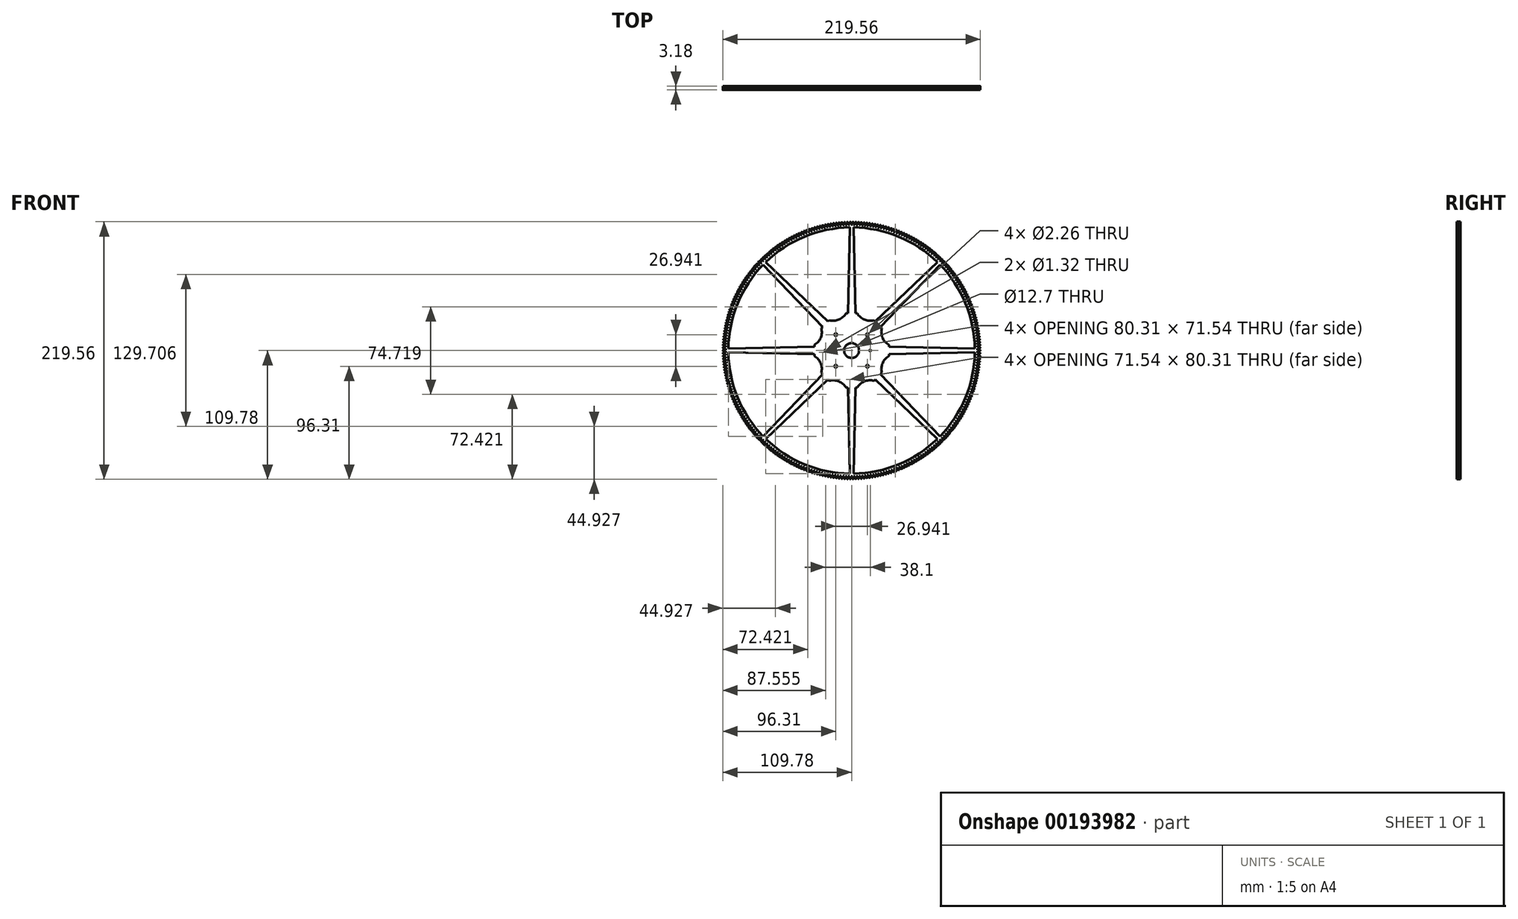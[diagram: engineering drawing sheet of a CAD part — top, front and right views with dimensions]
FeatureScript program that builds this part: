
annotation { "Feature Type Name" : "Feature", "Feature Type Description" : "" }
export const myFeature = defineFeature(function(context is Context, id is Id, definition is map)
    precondition{}
    {
        {
            var Q0;
            Q0=qCreatedBy(makeId("Front.planeOp"),FACE);
            var sketch = newSketch(context, id + "F0", { "sketchPlane" : qUnion([Q0])});
            skLineSegment(sketch, "E0", {"start": v(0, 0) * mm, "end": v(0, 109.78) * mm, "construction": true});
            skLineSegment(sketch, "E1", {"start": v(1.59, 105.01) * mm, "end": v(3.18, 31.75) * mm});
            skCircle(sketch, "E2.cCircle", {"center": v(0, 0) * mm, "radius": 31.75 * mm, "construction": true});
            skLineSegment(sketch, "E2.0", {"start": v(19.08, 25.82) * mm, "end": v(20.2, 24.7) * mm});
            skLineSegment(sketch, "E2.1", {"start": v(31.75, 4.76) * mm, "end": v(31.75, 3.18) * mm});
            skLineSegment(sketch, "E2.2", {"start": v(25.82, -19.08) * mm, "end": v(24.7, -20.2) * mm});
            skLineSegment(sketch, "E2.3", {"start": v(4.76, -31.75) * mm, "end": v(3.18, -31.75) * mm});
            skLineSegment(sketch, "E2.4", {"start": v(-19.08, -25.82) * mm, "end": v(-20.2, -24.7) * mm});
            skLineSegment(sketch, "E2.5", {"start": v(-31.75, -4.76) * mm, "end": v(-31.75, -3.18) * mm});
            skLineSegment(sketch, "E2.6", {"start": v(-25.82, 19.08) * mm, "end": v(-24.7, 20.2) * mm});
            skLineSegment(sketch, "E2.7", {"start": v(-4.76, 31.75) * mm, "end": v(-3.18, 31.75) * mm});
            skLineSegment(sketch, "E3", {"start": v(-1.59, 105.01) * mm, "end": v(-3.18, 31.75) * mm});
            skLineSegment(sketch, "E4", {"start": v(-1.59, 105.01) * mm, "end": v(1.59, 105.01) * mm, "construction": true});
            skLineSegment(sketch, "E5.1.0", {"start": v(73.13, 75.38) * mm, "end": v(75.38, 73.13) * mm, "construction": true});
            skLineSegment(sketch, "E5.1.1", {"start": v(73.13, 75.38) * mm, "end": v(20.2, 24.7) * mm});
            skLineSegment(sketch, "E5.1.2", {"start": v(0, 0) * mm, "end": v(74.25, 74.25) * mm, "construction": true});
            skLineSegment(sketch, "E5.1.3", {"start": v(75.38, 73.13) * mm, "end": v(24.7, 20.2) * mm});
            skLineSegment(sketch, "E5.2.0", {"start": v(105.01, 1.59) * mm, "end": v(105.01, -1.59) * mm, "construction": true});
            skLineSegment(sketch, "E5.2.1", {"start": v(105.01, 1.59) * mm, "end": v(31.75, 3.18) * mm});
            skLineSegment(sketch, "E5.2.2", {"start": v(0, 0) * mm, "end": v(105.01, 0) * mm, "construction": true});
            skLineSegment(sketch, "E5.2.3", {"start": v(105.01, -1.59) * mm, "end": v(31.75, -3.18) * mm});
            skLineSegment(sketch, "E5.3.0", {"start": v(75.38, -73.13) * mm, "end": v(73.13, -75.38) * mm, "construction": true});
            skLineSegment(sketch, "E5.3.1", {"start": v(75.38, -73.13) * mm, "end": v(24.7, -20.2) * mm});
            skLineSegment(sketch, "E5.3.2", {"start": v(0, 0) * mm, "end": v(74.25, -74.25) * mm, "construction": true});
            skLineSegment(sketch, "E5.3.3", {"start": v(73.13, -75.38) * mm, "end": v(20.2, -24.7) * mm});
            skLineSegment(sketch, "E5.4.0", {"start": v(1.59, -105.01) * mm, "end": v(-1.59, -105.01) * mm, "construction": true});
            skLineSegment(sketch, "E5.4.1", {"start": v(1.59, -105.01) * mm, "end": v(3.18, -31.75) * mm});
            skLineSegment(sketch, "E5.4.2", {"start": v(0, 0) * mm, "end": v(0, -105.01) * mm, "construction": true});
            skLineSegment(sketch, "E5.4.3", {"start": v(-1.59, -105.01) * mm, "end": v(-3.18, -31.75) * mm});
            skLineSegment(sketch, "E5.5.0", {"start": v(-73.13, -75.38) * mm, "end": v(-75.38, -73.13) * mm, "construction": true});
            skLineSegment(sketch, "E5.5.1", {"start": v(-73.13, -75.38) * mm, "end": v(-20.2, -24.7) * mm});
            skLineSegment(sketch, "E5.5.2", {"start": v(0, 0) * mm, "end": v(-74.25, -74.25) * mm, "construction": true});
            skLineSegment(sketch, "E5.5.3", {"start": v(-75.38, -73.13) * mm, "end": v(-24.7, -20.2) * mm});
            skLineSegment(sketch, "E5.6.0", {"start": v(-105.01, -1.59) * mm, "end": v(-105.01, 1.59) * mm, "construction": true});
            skLineSegment(sketch, "E5.6.1", {"start": v(-105.01, -1.59) * mm, "end": v(-31.75, -3.18) * mm});
            skLineSegment(sketch, "E5.6.2", {"start": v(0, 0) * mm, "end": v(-105.01, 0) * mm, "construction": true});
            skLineSegment(sketch, "E5.6.3", {"start": v(-105.01, 1.59) * mm, "end": v(-31.75, 3.18) * mm});
            skLineSegment(sketch, "E5.7.0", {"start": v(-75.38, 73.13) * mm, "end": v(-73.13, 75.38) * mm, "construction": true});
            skLineSegment(sketch, "E5.7.1", {"start": v(-75.38, 73.13) * mm, "end": v(-24.7, 20.2) * mm});
            skLineSegment(sketch, "E5.7.2", {"start": v(0, 0) * mm, "end": v(-74.25, 74.25) * mm, "construction": true});
            skLineSegment(sketch, "E5.7.3", {"start": v(-73.13, 75.38) * mm, "end": v(-20.2, 24.7) * mm});
            skArc(sketch, "E6", {"start": v(-31.75, 4.76) * mm, "mid": v(-26.35, 10.91) * mm, "end": v(-25.82, 19.08) * mm});
            skArc(sketch, "E7", {"start": v(-19.08, 25.82) * mm, "mid": v(-10.91, 26.35) * mm, "end": v(-4.76, 31.75) * mm});
            skArc(sketch, "E8", {"start": v(4.76, 31.75) * mm, "mid": v(10.91, 26.35) * mm, "end": v(19.08, 25.82) * mm});
            skArc(sketch, "E9", {"start": v(25.82, 19.08) * mm, "mid": v(26.35, 10.91) * mm, "end": v(31.75, 4.76) * mm});
            skArc(sketch, "E10", {"start": v(31.75, -4.76) * mm, "mid": v(26.35, -10.91) * mm, "end": v(25.82, -19.08) * mm});
            skArc(sketch, "E11", {"start": v(19.08, -25.82) * mm, "mid": v(10.91, -26.35) * mm, "end": v(4.76, -31.75) * mm});
            skArc(sketch, "E12", {"start": v(-4.76, -31.75) * mm, "mid": v(-10.91, -26.35) * mm, "end": v(-19.08, -25.82) * mm});
            skArc(sketch, "E13", {"start": v(-25.82, -19.08) * mm, "mid": v(-26.35, -10.91) * mm, "end": v(-31.75, -4.76) * mm});
            skArc(sketch, "E14", {"start": v(-105.01, -1.59) * mm, "mid": v(-97.03, -40.2) * mm, "end": v(-75.38, -73.13) * mm});
            skArc(sketch, "E15.trimOffspring", {"start": v(1.59, -105.01) * mm, "mid": v(40.2, -97.03) * mm, "end": v(73.13, -75.38) * mm});
            skArc(sketch, "E16.trimOffspring", {"start": v(-73.13, -75.38) * mm, "mid": v(-40.2, -97.03) * mm, "end": v(-1.59, -105.01) * mm});
            skArc(sketch, "E17.trimOffspring", {"start": v(75.38, -73.13) * mm, "mid": v(97.03, -40.2) * mm, "end": v(105.01, -1.59) * mm});
            skArc(sketch, "E18.trimOffspring", {"start": v(105.01, 1.59) * mm, "mid": v(97.03, 40.2) * mm, "end": v(75.38, 73.13) * mm});
            skArc(sketch, "E19.trimOffspring", {"start": v(73.13, 75.38) * mm, "mid": v(40.2, 97.03) * mm, "end": v(1.59, 105.01) * mm});
            skArc(sketch, "E20.trimOffspring", {"start": v(-1.59, 105.01) * mm, "mid": v(-40.2, 97.03) * mm, "end": v(-73.13, 75.38) * mm});
            skArc(sketch, "E21.trimOffspring", {"start": v(-75.38, 73.13) * mm, "mid": v(-97.03, 40.2) * mm, "end": v(-105.01, 1.59) * mm});
            skLineSegment(sketch, "E22.trimOffspring", {"start": v(3.18, 31.75) * mm, "end": v(4.76, 31.75) * mm});
            skLineSegment(sketch, "E23.trimOffspring", {"start": v(-20.2, 24.7) * mm, "end": v(-19.08, 25.82) * mm});
            skLineSegment(sketch, "E24.trimOffspring", {"start": v(-31.75, 3.18) * mm, "end": v(-31.75, 4.76) * mm});
            skLineSegment(sketch, "E25.trimOffspring", {"start": v(-24.7, -20.2) * mm, "end": v(-25.82, -19.08) * mm});
            skLineSegment(sketch, "E26.trimOffspring", {"start": v(-3.18, -31.75) * mm, "end": v(-4.76, -31.75) * mm});
            skLineSegment(sketch, "E27.trimOffspring", {"start": v(20.2, -24.7) * mm, "end": v(19.08, -25.82) * mm});
            skLineSegment(sketch, "E28.trimOffspring", {"start": v(31.75, -3.18) * mm, "end": v(31.75, -4.76) * mm});
            skLineSegment(sketch, "E29.trimOffspring", {"start": v(24.7, 20.2) * mm, "end": v(25.82, 19.08) * mm});
            skPoint(sketch, "E30", {"position": v(22.45, 22.45) * mm});
            skLineSegment(sketch, "E31", {"start": v(20.2, 24.7) * mm, "end": v(24.7, 20.2) * mm, "construction": true});
            skLineSegment(sketch, "E32", {"start": v(31.75, 3.18) * mm, "end": v(31.75, -3.18) * mm, "construction": true});
            skPoint(sketch, "E33", {"position": v(31.75, 0) * mm});
            skLineSegment(sketch, "E34", {"start": v(-3.18, 31.75) * mm, "end": v(3.18, 31.75) * mm, "construction": true});
            skPoint(sketch, "E35", {"position": v(0, 31.75) * mm});
            skLineSegment(sketch, "E36", {"start": v(20.2, -24.7) * mm, "end": v(24.7, -20.2) * mm, "construction": true});
            skPoint(sketch, "E37", {"position": v(22.45, -22.45) * mm});
            skLineSegment(sketch, "E38", {"start": v(-3.18, -31.75) * mm, "end": v(3.18, -31.75) * mm, "construction": true});
            skPoint(sketch, "E39", {"position": v(0, -31.75) * mm});
            skLineSegment(sketch, "E40", {"start": v(-24.7, -20.2) * mm, "end": v(-20.2, -24.7) * mm, "construction": true});
            skPoint(sketch, "E41", {"position": v(-22.45, -22.45) * mm});
            skLineSegment(sketch, "E42", {"start": v(-31.75, 3.18) * mm, "end": v(-31.75, -3.18) * mm, "construction": true});
            skPoint(sketch, "E43", {"position": v(-31.75, 0) * mm});
            skLineSegment(sketch, "E44", {"start": v(-24.7, 20.2) * mm, "end": v(-20.2, 24.7) * mm, "construction": true});
            skPoint(sketch, "E45", {"position": v(-22.45, 22.45) * mm});
            skCircle(sketch, "E46", {"center": v(0, 0) * mm, "radius": 6.35 * mm});
            skCircle(sketch, "E47", {"center": v(0, 0) * mm, "radius": 19.05 * mm, "construction": true});
            skCircle(sketch, "E48", {"center": v(-13.47, 13.47) * mm, "radius": 1.13 * mm});
            skCircle(sketch, "E49.1.0", {"center": v(-13.47, -13.47) * mm, "radius": 1.13 * mm});
            skCircle(sketch, "E49.2.0", {"center": v(13.47, -13.47) * mm, "radius": 1.13 * mm});
            skCircle(sketch, "E50.1.3.0", {"center": v(13.47, 13.47) * mm, "radius": 1.13 * mm});
            skCircle(sketch, "E51", {"center": v(0, 0) * mm, "radius": 107.25 * mm, "construction": true});
            skCircle(sketch, "E52", {"center": v(0, 0) * mm, "radius": 109.78 * mm, "construction": true});
            skCircle(sketch, "E53", {"center": v(0, 0) * mm, "radius": 108.75 * mm, "construction": true});
            skLineSegment(sketch, "E54", {"start": v(0, 0) * mm, "end": v(2.38, 109.76) * mm, "construction": true});
            skLineSegment(sketch, "E55", {"start": v(1.19, 109.78) * mm, "end": v(0, 0) * mm, "construction": true});
            skPoint(sketch, "E56.orphan", {"position": v(0, 105.01) * mm});
            skLineSegment(sketch, "E57", {"start": v(0.63, 107.25) * mm, "end": v(0.58, 108.55) * mm});
            skLineSegment(sketch, "E58", {"start": v(1.7, 107.24) * mm, "end": v(1.77, 108.54) * mm});
            skArc(sketch, "E59", {"start": v(1.19, 109.78) * mm, "mid": v(0.73, 109.24) * mm, "end": v(0.58, 108.55) * mm});
            skArc(sketch, "E60", {"start": v(1.77, 108.54) * mm, "mid": v(1.64, 109.23) * mm, "end": v(1.19, 109.78) * mm});
            skLineSegment(sketch, "E61", {"start": v(0.59, 108.75) * mm, "end": v(1.77, 108.74) * mm, "construction": true});
            skPoint(sketch, "E62", {"position": v(1.18, 108.74) * mm});
            skLineSegment(sketch, "E63", {"start": v(0.63, 107.25) * mm, "end": v(1.7, 107.24) * mm, "construction": true});
            skPoint(sketch, "E64", {"position": v(1.16, 107.24) * mm});
            skLineSegment(sketch, "E65.1.0", {"start": v(-1.7, 107.24) * mm, "end": v(-1.77, 108.54) * mm});
            skArc(sketch, "E65.1.1", {"start": v(-1.19, 109.78) * mm, "mid": v(-1.64, 109.23) * mm, "end": v(-1.77, 108.54) * mm});
            skArc(sketch, "E65.1.2", {"start": v(-0.58, 108.55) * mm, "mid": v(-0.73, 109.24) * mm, "end": v(-1.19, 109.78) * mm});
            skLineSegment(sketch, "E65.1.3", {"start": v(-0.63, 107.25) * mm, "end": v(-0.58, 108.55) * mm});
            skLineSegment(sketch, "E65.2.0", {"start": v(-4.02, 107.17) * mm, "end": v(-4.12, 108.47) * mm});
            skArc(sketch, "E65.2.1", {"start": v(-3.57, 109.73) * mm, "mid": v(-4, 109.17) * mm, "end": v(-4.12, 108.47) * mm});
            skArc(sketch, "E65.2.2", {"start": v(-2.93, 108.51) * mm, "mid": v(-3.1, 109.2) * mm, "end": v(-3.57, 109.73) * mm});
            skLineSegment(sketch, "E65.2.3", {"start": v(-2.95, 107.2) * mm, "end": v(-2.93, 108.51) * mm});
            skLineSegment(sketch, "E66.1.3.0", {"start": v(-6.34, 107.06) * mm, "end": v(-6.47, 108.36) * mm});
            skArc(sketch, "E66.3.3.0", {"start": v(-5.94, 109.62) * mm, "mid": v(-6.37, 109.06) * mm, "end": v(-6.47, 108.36) * mm});
            skArc(sketch, "E66.7.3.0", {"start": v(-5.28, 108.42) * mm, "mid": v(-5.46, 109.1) * mm, "end": v(-5.94, 109.62) * mm});
            skLineSegment(sketch, "E66.11.3.0", {"start": v(-5.27, 107.12) * mm, "end": v(-5.28, 108.42) * mm});
            skLineSegment(sketch, "E66.1.4.0", {"start": v(-8.66, 106.9) * mm, "end": v(-8.82, 108.2) * mm});
            skArc(sketch, "E66.3.4.0", {"start": v(-8.32, 109.47) * mm, "mid": v(-8.73, 108.9) * mm, "end": v(-8.82, 108.2) * mm});
            skArc(sketch, "E66.7.4.0", {"start": v(-7.63, 108.28) * mm, "mid": v(-7.83, 108.96) * mm, "end": v(-8.32, 109.47) * mm});
            skLineSegment(sketch, "E66.11.4.0", {"start": v(-7.6, 106.98) * mm, "end": v(-7.63, 108.28) * mm});
            skLineSegment(sketch, "E66.1.5.0", {"start": v(-10.97, 106.69) * mm, "end": v(-11.16, 107.98) * mm});
            skArc(sketch, "E66.3.5.0", {"start": v(-10.69, 109.26) * mm, "mid": v(-11.08, 108.68) * mm, "end": v(-11.16, 107.98) * mm});
            skArc(sketch, "E66.7.5.0", {"start": v(-9.98, 108.1) * mm, "mid": v(-10.18, 108.77) * mm, "end": v(-10.69, 109.26) * mm});
            skLineSegment(sketch, "E66.11.5.0", {"start": v(-9.9, 106.8) * mm, "end": v(-9.98, 108.1) * mm});
            skLineSegment(sketch, "E66.1.6.0", {"start": v(-13.28, 106.42) * mm, "end": v(-13.5, 107.7) * mm});
            skArc(sketch, "E66.3.6.0", {"start": v(-13.05, 109) * mm, "mid": v(-13.44, 108.41) * mm, "end": v(-13.5, 107.7) * mm});
            skArc(sketch, "E66.7.6.0", {"start": v(-12.32, 107.85) * mm, "mid": v(-12.54, 108.52) * mm, "end": v(-13.05, 109) * mm});
            skLineSegment(sketch, "E66.11.6.0", {"start": v(-12.22, 106.55) * mm, "end": v(-12.32, 107.85) * mm});
            skLineSegment(sketch, "E66.1.7.0", {"start": v(-15.58, 106.11) * mm, "end": v(-15.82, 107.4) * mm});
            skArc(sketch, "E66.3.7.0", {"start": v(-15.4, 108.7) * mm, "mid": v(-15.78, 108.1) * mm, "end": v(-15.82, 107.4) * mm});
            skArc(sketch, "E66.7.7.0", {"start": v(-14.65, 107.56) * mm, "mid": v(-14.89, 108.22) * mm, "end": v(-15.4, 108.7) * mm});
            skLineSegment(sketch, "E66.11.7.0", {"start": v(-14.53, 106.26) * mm, "end": v(-14.65, 107.56) * mm});
            skLineSegment(sketch, "E66.1.8.0", {"start": v(-17.88, 105.75) * mm, "end": v(-18.15, 107.02) * mm});
            skArc(sketch, "E66.3.8.0", {"start": v(-17.76, 108.34) * mm, "mid": v(-18.12, 107.73) * mm, "end": v(-18.15, 107.02) * mm});
            skArc(sketch, "E66.7.8.0", {"start": v(-16.98, 107.22) * mm, "mid": v(-17.23, 107.88) * mm, "end": v(-17.76, 108.34) * mm});
            skLineSegment(sketch, "E66.11.8.0", {"start": v(-16.82, 105.92) * mm, "end": v(-16.98, 107.22) * mm});
            skLineSegment(sketch, "E66.1.9.0", {"start": v(-20.16, 105.34) * mm, "end": v(-20.46, 106.6) * mm});
            skArc(sketch, "E66.3.9.0", {"start": v(-20.1, 107.93) * mm, "mid": v(-20.45, 107.31) * mm, "end": v(-20.46, 106.6) * mm});
            skArc(sketch, "E66.7.9.0", {"start": v(-19.3, 106.82) * mm, "mid": v(-19.56, 107.48) * mm, "end": v(-20.1, 107.93) * mm});
            skLineSegment(sketch, "E66.11.9.0", {"start": v(-19.11, 105.53) * mm, "end": v(-19.3, 106.82) * mm});
            skLineSegment(sketch, "E66.1.10.0", {"start": v(-22.44, 104.88) * mm, "end": v(-22.77, 106.14) * mm});
            skArc(sketch, "E66.3.10.0", {"start": v(-22.44, 107.47) * mm, "mid": v(-22.77, 106.84) * mm, "end": v(-22.77, 106.14) * mm});
            skArc(sketch, "E66.7.10.0", {"start": v(-21.6, 106.38) * mm, "mid": v(-21.88, 107.03) * mm, "end": v(-22.44, 107.47) * mm});
            skLineSegment(sketch, "E66.11.10.0", {"start": v(-21.4, 105.1) * mm, "end": v(-21.6, 106.38) * mm});
            skLineSegment(sketch, "E66.1.11.0", {"start": v(-24.7, 104.36) * mm, "end": v(-25.06, 105.62) * mm});
            skArc(sketch, "E66.3.11.0", {"start": v(-24.76, 106.96) * mm, "mid": v(-25.08, 106.33) * mm, "end": v(-25.06, 105.62) * mm});
            skArc(sketch, "E66.7.11.0", {"start": v(-23.9, 105.89) * mm, "mid": v(-24.2, 106.53) * mm, "end": v(-24.76, 106.96) * mm});
            skLineSegment(sketch, "E66.11.11.0", {"start": v(-23.67, 104.6) * mm, "end": v(-23.9, 105.89) * mm});
            skLineSegment(sketch, "E66.1.12.0", {"start": v(-26.96, 103.8) * mm, "end": v(-27.34, 105.05) * mm});
            skArc(sketch, "E66.3.12.0", {"start": v(-27.07, 106.4) * mm, "mid": v(-27.38, 105.76) * mm, "end": v(-27.34, 105.05) * mm});
            skArc(sketch, "E66.7.12.0", {"start": v(-26.2, 105.34) * mm, "mid": v(-26.5, 105.98) * mm, "end": v(-27.07, 106.4) * mm});
            skLineSegment(sketch, "E66.11.12.0", {"start": v(-25.93, 104.07) * mm, "end": v(-26.2, 105.34) * mm});
            skLineSegment(sketch, "E66.1.13.0", {"start": v(-29.2, 103.2) * mm, "end": v(-29.61, 104.43) * mm});
            skArc(sketch, "E66.3.13.0", {"start": v(-29.37, 105.78) * mm, "mid": v(-29.66, 105.14) * mm, "end": v(-29.61, 104.43) * mm});
            skArc(sketch, "E66.7.13.0", {"start": v(-28.47, 104.75) * mm, "mid": v(-28.79, 105.38) * mm, "end": v(-29.37, 105.78) * mm});
            skLineSegment(sketch, "E66.11.13.0", {"start": v(-28.18, 103.48) * mm, "end": v(-28.47, 104.75) * mm});
            skLineSegment(sketch, "E66.1.14.0", {"start": v(-31.44, 102.54) * mm, "end": v(-31.87, 103.77) * mm});
            skArc(sketch, "E66.3.14.0", {"start": v(-31.66, 105.12) * mm, "mid": v(-31.93, 104.47) * mm, "end": v(-31.87, 103.77) * mm});
            skArc(sketch, "E66.7.14.0", {"start": v(-30.73, 104.1) * mm, "mid": v(-31.07, 104.73) * mm, "end": v(-31.66, 105.12) * mm});
            skLineSegment(sketch, "E66.11.14.0", {"start": v(-30.41, 102.85) * mm, "end": v(-30.73, 104.1) * mm});
            skLineSegment(sketch, "E66.1.15.0", {"start": v(-33.65, 101.83) * mm, "end": v(-34.1, 103.05) * mm});
            skArc(sketch, "E66.3.15.0", {"start": v(-33.93, 104.41) * mm, "mid": v(-34.19, 103.76) * mm, "end": v(-34.1, 103.05) * mm});
            skArc(sketch, "E66.7.15.0", {"start": v(-32.98, 103.42) * mm, "mid": v(-33.33, 104.03) * mm, "end": v(-33.93, 104.41) * mm});
            skLineSegment(sketch, "E66.11.15.0", {"start": v(-32.63, 102.16) * mm, "end": v(-32.98, 103.42) * mm});
            skLineSegment(sketch, "E66.1.16.0", {"start": v(-35.85, 101.08) * mm, "end": v(-36.33, 102.29) * mm});
            skArc(sketch, "E66.3.16.0", {"start": v(-36.18, 103.65) * mm, "mid": v(-36.43, 103) * mm, "end": v(-36.33, 102.29) * mm});
            skArc(sketch, "E66.7.16.0", {"start": v(-35.21, 102.68) * mm, "mid": v(-35.57, 103.29) * mm, "end": v(-36.18, 103.65) * mm});
            skLineSegment(sketch, "E66.11.16.0", {"start": v(-34.84, 101.43) * mm, "end": v(-35.21, 102.68) * mm});
            skLineSegment(sketch, "E66.1.17.0", {"start": v(-38.03, 100.28) * mm, "end": v(-38.54, 101.48) * mm});
            skArc(sketch, "E66.3.17.0", {"start": v(-38.42, 102.84) * mm, "mid": v(-38.65, 102.18) * mm, "end": v(-38.54, 101.48) * mm});
            skArc(sketch, "E66.7.17.0", {"start": v(-37.43, 101.9) * mm, "mid": v(-37.8, 102.5) * mm, "end": v(-38.42, 102.84) * mm});
            skLineSegment(sketch, "E66.11.17.0", {"start": v(-37.03, 100.65) * mm, "end": v(-37.43, 101.9) * mm});
            skLineSegment(sketch, "E66.1.18.0", {"start": v(-40.2, 99.43) * mm, "end": v(-40.73, 100.62) * mm});
            skArc(sketch, "E66.3.18.0", {"start": v(-40.64, 101.99) * mm, "mid": v(-40.85, 101.32) * mm, "end": v(-40.73, 100.62) * mm});
            skArc(sketch, "E66.7.18.0", {"start": v(-39.63, 101.06) * mm, "mid": v(-40.01, 101.65) * mm, "end": v(-40.64, 101.99) * mm});
            skLineSegment(sketch, "E66.11.18.0", {"start": v(-39.2, 99.83) * mm, "end": v(-39.63, 101.06) * mm});
            skLineSegment(sketch, "E66.1.19.0", {"start": v(-42.34, 98.54) * mm, "end": v(-42.9, 99.71) * mm});
            skArc(sketch, "E66.3.19.0", {"start": v(-42.84, 101.08) * mm, "mid": v(-43.04, 100.4) * mm, "end": v(-42.9, 99.71) * mm});
            skArc(sketch, "E66.7.19.0", {"start": v(-41.8, 100.18) * mm, "mid": v(-42.2, 100.76) * mm, "end": v(-42.84, 101.08) * mm});
            skLineSegment(sketch, "E66.11.19.0", {"start": v(-41.35, 98.96) * mm, "end": v(-41.8, 100.18) * mm});
            skLineSegment(sketch, "E66.1.20.0", {"start": v(-44.46, 97.6) * mm, "end": v(-45.05, 98.76) * mm});
            skArc(sketch, "E66.3.20.0", {"start": v(-45.02, 100.13) * mm, "mid": v(-45.2, 99.45) * mm, "end": v(-45.05, 98.76) * mm});
            skArc(sketch, "E66.7.20.0", {"start": v(-43.97, 99.25) * mm, "mid": v(-44.38, 99.82) * mm, "end": v(-45.02, 100.13) * mm});
            skLineSegment(sketch, "E66.11.20.0", {"start": v(-43.49, 98.04) * mm, "end": v(-43.97, 99.25) * mm});
            skLineSegment(sketch, "E66.1.21.0", {"start": v(-46.57, 96.61) * mm, "end": v(-47.18, 97.76) * mm});
            skArc(sketch, "E66.3.21.0", {"start": v(-47.17, 99.13) * mm, "mid": v(-47.35, 98.45) * mm, "end": v(-47.18, 97.76) * mm});
            skArc(sketch, "E66.7.21.0", {"start": v(-46.1, 98.27) * mm, "mid": v(-46.53, 98.84) * mm, "end": v(-47.17, 99.13) * mm});
            skLineSegment(sketch, "E66.11.21.0", {"start": v(-45.6, 97.07) * mm, "end": v(-46.1, 98.27) * mm});
            skLineSegment(sketch, "E66.1.22.0", {"start": v(-48.65, 95.58) * mm, "end": v(-49.29, 96.72) * mm});
            skArc(sketch, "E66.3.22.0", {"start": v(-49.31, 98.09) * mm, "mid": v(-49.47, 97.4) * mm, "end": v(-49.29, 96.72) * mm});
            skArc(sketch, "E66.7.22.0", {"start": v(-48.23, 97.25) * mm, "mid": v(-48.66, 97.8) * mm, "end": v(-49.31, 98.09) * mm});
            skLineSegment(sketch, "E66.11.22.0", {"start": v(-47.7, 96.06) * mm, "end": v(-48.23, 97.25) * mm});
            skLineSegment(sketch, "E66.1.23.0", {"start": v(-50.7, 94.5) * mm, "end": v(-51.37, 95.63) * mm});
            skArc(sketch, "E66.3.23.0", {"start": v(-51.42, 97) * mm, "mid": v(-51.57, 96.3) * mm, "end": v(-51.37, 95.63) * mm});
            skArc(sketch, "E66.7.23.0", {"start": v(-50.32, 96.18) * mm, "mid": v(-50.77, 96.73) * mm, "end": v(-51.42, 97) * mm});
            skLineSegment(sketch, "E66.11.23.0", {"start": v(-49.76, 95) * mm, "end": v(-50.32, 96.18) * mm});
            skLineSegment(sketch, "E66.1.24.0", {"start": v(-52.74, 93.38) * mm, "end": v(-53.43, 94.5) * mm});
            skArc(sketch, "E66.3.24.0", {"start": v(-53.51, 95.86) * mm, "mid": v(-53.64, 95.16) * mm, "end": v(-53.43, 94.5) * mm});
            skArc(sketch, "E66.7.24.0", {"start": v(-52.4, 95.07) * mm, "mid": v(-52.85, 95.6) * mm, "end": v(-53.51, 95.86) * mm});
            skLineSegment(sketch, "E66.11.24.0", {"start": v(-51.81, 93.9) * mm, "end": v(-52.4, 95.07) * mm});
            skLineSegment(sketch, "E66.1.25.0", {"start": v(-54.75, 92.22) * mm, "end": v(-55.46, 93.31) * mm});
            skArc(sketch, "E66.3.25.0", {"start": v(-55.58, 94.68) * mm, "mid": v(-55.7, 93.98) * mm, "end": v(-55.46, 93.31) * mm});
            skArc(sketch, "E66.7.25.0", {"start": v(-54.44, 93.91) * mm, "mid": v(-54.91, 94.44) * mm, "end": v(-55.58, 94.68) * mm});
            skLineSegment(sketch, "E66.11.25.0", {"start": v(-53.83, 92.76) * mm, "end": v(-54.44, 93.91) * mm});
            skLineSegment(sketch, "E66.1.26.0", {"start": v(-56.74, 91.01) * mm, "end": v(-57.47, 92.09) * mm});
            skArc(sketch, "E66.3.26.0", {"start": v(-57.62, 93.45) * mm, "mid": v(-57.72, 92.75) * mm, "end": v(-57.47, 92.09) * mm});
            skArc(sketch, "E66.7.26.0", {"start": v(-56.46, 92.71) * mm, "mid": v(-56.95, 93.23) * mm, "end": v(-57.62, 93.45) * mm});
            skLineSegment(sketch, "E66.11.26.0", {"start": v(-55.83, 91.57) * mm, "end": v(-56.46, 92.71) * mm});
            skLineSegment(sketch, "E66.1.27.0", {"start": v(-58.7, 89.76) * mm, "end": v(-59.45, 90.82) * mm});
            skArc(sketch, "E66.3.27.0", {"start": v(-59.63, 92.18) * mm, "mid": v(-59.71, 91.48) * mm, "end": v(-59.45, 90.82) * mm});
            skArc(sketch, "E66.7.27.0", {"start": v(-58.46, 91.47) * mm, "mid": v(-58.95, 91.97) * mm, "end": v(-59.63, 92.18) * mm});
            skLineSegment(sketch, "E66.11.27.0", {"start": v(-57.8, 90.34) * mm, "end": v(-58.46, 91.47) * mm});
            skLineSegment(sketch, "E66.1.28.0", {"start": v(-60.63, 88.47) * mm, "end": v(-61.4, 89.51) * mm});
            skArc(sketch, "E66.3.28.0", {"start": v(-61.6, 90.87) * mm, "mid": v(-61.68, 90.16) * mm, "end": v(-61.4, 89.51) * mm});
            skArc(sketch, "E66.7.28.0", {"start": v(-60.43, 90.18) * mm, "mid": v(-60.93, 90.67) * mm, "end": v(-61.6, 90.87) * mm});
            skLineSegment(sketch, "E66.11.28.0", {"start": v(-59.74, 89.07) * mm, "end": v(-60.43, 90.18) * mm});
            skLineSegment(sketch, "E66.1.29.0", {"start": v(-62.53, 87.13) * mm, "end": v(-63.33, 88.16) * mm});
            skArc(sketch, "E66.3.29.0", {"start": v(-63.56, 89.51) * mm, "mid": v(-63.62, 88.8) * mm, "end": v(-63.33, 88.16) * mm});
            skArc(sketch, "E66.7.29.0", {"start": v(-62.36, 88.85) * mm, "mid": v(-62.88, 89.33) * mm, "end": v(-63.56, 89.51) * mm});
            skLineSegment(sketch, "E66.11.29.0", {"start": v(-61.66, 87.75) * mm, "end": v(-62.36, 88.85) * mm});
            skLineSegment(sketch, "E66.1.30.0", {"start": v(-64.4, 85.76) * mm, "end": v(-65.23, 86.77) * mm});
            skArc(sketch, "E66.3.30.0", {"start": v(-65.49, 88.11) * mm, "mid": v(-65.53, 87.4) * mm, "end": v(-65.23, 86.77) * mm});
            skArc(sketch, "E66.7.30.0", {"start": v(-64.27, 87.48) * mm, "mid": v(-64.8, 87.95) * mm, "end": v(-65.49, 88.11) * mm});
            skLineSegment(sketch, "E66.11.30.0", {"start": v(-63.55, 86.4) * mm, "end": v(-64.27, 87.48) * mm});
            skLineSegment(sketch, "E66.1.31.0", {"start": v(-66.25, 84.34) * mm, "end": v(-67.1, 85.33) * mm});
            skArc(sketch, "E66.3.31.0", {"start": v(-67.38, 86.67) * mm, "mid": v(-67.4, 85.97) * mm, "end": v(-67.1, 85.33) * mm});
            skArc(sketch, "E66.7.31.0", {"start": v(-66.15, 86.06) * mm, "mid": v(-66.7, 86.52) * mm, "end": v(-67.38, 86.67) * mm});
            skLineSegment(sketch, "E66.11.31.0", {"start": v(-65.4, 85) * mm, "end": v(-66.15, 86.06) * mm});
            skLineSegment(sketch, "E66.1.32.0", {"start": v(-68.06, 82.89) * mm, "end": v(-68.92, 83.86) * mm});
            skArc(sketch, "E66.3.32.0", {"start": v(-69.24, 85.2) * mm, "mid": v(-69.25, 84.49) * mm, "end": v(-68.92, 83.86) * mm});
            skArc(sketch, "E66.7.32.0", {"start": v(-68, 84.6) * mm, "mid": v(-68.55, 85.06) * mm, "end": v(-69.24, 85.2) * mm});
            skLineSegment(sketch, "E66.11.32.0", {"start": v(-67.23, 83.56) * mm, "end": v(-68, 84.6) * mm});
            skLineSegment(sketch, "E66.1.33.0", {"start": v(-69.84, 81.4) * mm, "end": v(-70.73, 82.35) * mm});
            skArc(sketch, "E66.3.33.0", {"start": v(-71.07, 83.67) * mm, "mid": v(-71.07, 82.97) * mm, "end": v(-70.73, 82.35) * mm});
            skArc(sketch, "E66.7.33.0", {"start": v(-69.82, 83.12) * mm, "mid": v(-70.38, 83.55) * mm, "end": v(-71.07, 83.67) * mm});
            skLineSegment(sketch, "E66.11.33.0", {"start": v(-69.02, 82.09) * mm, "end": v(-69.82, 83.12) * mm});
            skLineSegment(sketch, "E66.1.34.0", {"start": v(-71.59, 79.86) * mm, "end": v(-72.5, 80.8) * mm});
            skArc(sketch, "E66.3.34.0", {"start": v(-72.87, 82.11) * mm, "mid": v(-72.85, 81.4) * mm, "end": v(-72.5, 80.8) * mm});
            skArc(sketch, "E66.7.34.0", {"start": v(-71.6, 81.58) * mm, "mid": v(-72.17, 82) * mm, "end": v(-72.87, 82.11) * mm});
            skLineSegment(sketch, "E66.11.34.0", {"start": v(-70.79, 80.57) * mm, "end": v(-71.6, 81.58) * mm});
            skLineSegment(sketch, "E66.1.35.0", {"start": v(-73.3, 78.3) * mm, "end": v(-74.23, 79.2) * mm});
            skArc(sketch, "E66.3.35.0", {"start": v(-74.63, 80.52) * mm, "mid": v(-74.6, 79.81) * mm, "end": v(-74.23, 79.2) * mm});
            skArc(sketch, "E66.7.35.0", {"start": v(-73.36, 80.01) * mm, "mid": v(-73.93, 80.43) * mm, "end": v(-74.63, 80.52) * mm});
            skLineSegment(sketch, "E66.11.35.0", {"start": v(-72.52, 79.02) * mm, "end": v(-73.36, 80.01) * mm});
            skLineSegment(sketch, "E66.1.36.0", {"start": v(-74.98, 76.69) * mm, "end": v(-75.92, 77.58) * mm});
            skArc(sketch, "E66.3.36.0", {"start": v(-76.36, 78.88) * mm, "mid": v(-76.3, 78.18) * mm, "end": v(-75.92, 77.58) * mm});
            skArc(sketch, "E66.7.36.0", {"start": v(-75.07, 78.4) * mm, "mid": v(-75.66, 78.8) * mm, "end": v(-76.36, 78.88) * mm});
            skLineSegment(sketch, "E66.11.36.0", {"start": v(-74.21, 77.43) * mm, "end": v(-75.07, 78.4) * mm});
            skLineSegment(sketch, "E66.1.37.0", {"start": v(-76.62, 75.04) * mm, "end": v(-77.59, 75.92) * mm});
            skArc(sketch, "E66.3.37.0", {"start": v(-78.05, 77.2) * mm, "mid": v(-77.98, 76.5) * mm, "end": v(-77.59, 75.92) * mm});
            skArc(sketch, "E66.7.37.0", {"start": v(-76.75, 76.76) * mm, "mid": v(-77.34, 77.15) * mm, "end": v(-78.05, 77.2) * mm});
            skLineSegment(sketch, "E66.11.37.0", {"start": v(-75.87, 75.8) * mm, "end": v(-76.75, 76.76) * mm});
            skLineSegment(sketch, "E66.1.38.0", {"start": v(-78.23, 73.37) * mm, "end": v(-79.21, 74.22) * mm});
            skArc(sketch, "E66.3.38.0", {"start": v(-79.7, 75.5) * mm, "mid": v(-79.62, 74.8) * mm, "end": v(-79.21, 74.22) * mm});
            skArc(sketch, "E66.7.38.0", {"start": v(-78.4, 75.08) * mm, "mid": v(-79, 75.45) * mm, "end": v(-79.7, 75.5) * mm});
            skLineSegment(sketch, "E66.11.38.0", {"start": v(-77.5, 74.14) * mm, "end": v(-78.4, 75.08) * mm});
            skLineSegment(sketch, "E66.1.39.0", {"start": v(-79.8, 71.66) * mm, "end": v(-80.8, 72.48) * mm});
            skArc(sketch, "E66.3.39.0", {"start": v(-81.32, 73.75) * mm, "mid": v(-81.22, 73.05) * mm, "end": v(-80.8, 72.48) * mm});
            skArc(sketch, "E66.7.39.0", {"start": v(-80, 73.36) * mm, "mid": v(-80.61, 73.72) * mm, "end": v(-81.32, 73.75) * mm});
            skLineSegment(sketch, "E66.11.39.0", {"start": v(-79.08, 72.45) * mm, "end": v(-80, 73.36) * mm});
            skLineSegment(sketch, "E66.1.40.0", {"start": v(-81.33, 69.9) * mm, "end": v(-82.35, 70.72) * mm});
            skArc(sketch, "E66.3.40.0", {"start": v(-82.9, 71.98) * mm, "mid": v(-82.79, 71.28) * mm, "end": v(-82.35, 70.72) * mm});
            skArc(sketch, "E66.7.40.0", {"start": v(-81.58, 71.61) * mm, "mid": v(-82.2, 71.96) * mm, "end": v(-82.9, 71.98) * mm});
            skLineSegment(sketch, "E66.11.40.0", {"start": v(-80.63, 70.72) * mm, "end": v(-81.58, 71.61) * mm});
            skLineSegment(sketch, "E66.1.41.0", {"start": v(-82.83, 68.13) * mm, "end": v(-83.87, 68.92) * mm});
            skArc(sketch, "E66.3.41.0", {"start": v(-84.44, 70.16) * mm, "mid": v(-84.31, 69.47) * mm, "end": v(-83.87, 68.92) * mm});
            skArc(sketch, "E66.7.41.0", {"start": v(-83.1, 69.83) * mm, "mid": v(-83.73, 70.16) * mm, "end": v(-84.44, 70.16) * mm});
            skLineSegment(sketch, "E66.11.41.0", {"start": v(-82.15, 68.95) * mm, "end": v(-83.1, 69.83) * mm});
            skLineSegment(sketch, "E66.1.42.0", {"start": v(-84.29, 66.32) * mm, "end": v(-85.34, 67.08) * mm});
            skArc(sketch, "E66.3.42.0", {"start": v(-85.94, 68.32) * mm, "mid": v(-85.8, 67.62) * mm, "end": v(-85.34, 67.08) * mm});
            skArc(sketch, "E66.7.42.0", {"start": v(-84.6, 68.01) * mm, "mid": v(-85.23, 68.33) * mm, "end": v(-85.94, 68.32) * mm});
            skLineSegment(sketch, "E66.11.42.0", {"start": v(-83.62, 67.16) * mm, "end": v(-84.6, 68.01) * mm});
            skLineSegment(sketch, "E66.1.43.0", {"start": v(-85.7, 64.48) * mm, "end": v(-86.77, 65.22) * mm});
            skArc(sketch, "E66.3.43.0", {"start": v(-87.4, 66.44) * mm, "mid": v(-87.24, 65.75) * mm, "end": v(-86.77, 65.22) * mm});
            skArc(sketch, "E66.7.43.0", {"start": v(-86.06, 66.16) * mm, "mid": v(-86.7, 66.47) * mm, "end": v(-87.4, 66.44) * mm});
            skLineSegment(sketch, "E66.11.43.0", {"start": v(-85.06, 65.33) * mm, "end": v(-86.06, 66.16) * mm});
            skLineSegment(sketch, "E66.1.44.0", {"start": v(-87.08, 62.6) * mm, "end": v(-88.17, 63.32) * mm});
            skArc(sketch, "E66.3.44.0", {"start": v(-88.82, 64.53) * mm, "mid": v(-88.64, 63.84) * mm, "end": v(-88.17, 63.32) * mm});
            skArc(sketch, "E66.7.44.0", {"start": v(-87.47, 64.28) * mm, "mid": v(-88.11, 64.58) * mm, "end": v(-88.82, 64.53) * mm});
            skLineSegment(sketch, "E66.11.44.0", {"start": v(-86.45, 63.47) * mm, "end": v(-87.47, 64.28) * mm});
            skLineSegment(sketch, "E66.1.45.0", {"start": v(-88.42, 60.7) * mm, "end": v(-89.52, 61.4) * mm});
            skArc(sketch, "E66.3.45.0", {"start": v(-90.2, 62.6) * mm, "mid": v(-90, 61.9) * mm, "end": v(-89.52, 61.4) * mm});
            skArc(sketch, "E66.7.45.0", {"start": v(-88.84, 62.37) * mm, "mid": v(-89.5, 62.65) * mm, "end": v(-90.2, 62.6) * mm});
            skLineSegment(sketch, "E66.11.45.0", {"start": v(-87.8, 61.58) * mm, "end": v(-88.84, 62.37) * mm});
            skLineSegment(sketch, "E66.1.46.0", {"start": v(-89.71, 58.78) * mm, "end": v(-90.83, 59.44) * mm});
            skArc(sketch, "E66.3.46.0", {"start": v(-91.53, 60.62) * mm, "mid": v(-91.33, 59.94) * mm, "end": v(-90.83, 59.44) * mm});
            skArc(sketch, "E66.7.46.0", {"start": v(-90.17, 60.43) * mm, "mid": v(-90.83, 60.7) * mm, "end": v(-91.53, 60.62) * mm});
            skLineSegment(sketch, "E66.11.46.0", {"start": v(-89.12, 59.67) * mm, "end": v(-90.17, 60.43) * mm});
            skLineSegment(sketch, "E66.1.47.0", {"start": v(-90.96, 56.82) * mm, "end": v(-92.1, 57.46) * mm});
            skArc(sketch, "E66.3.47.0", {"start": v(-92.82, 58.62) * mm, "mid": v(-92.6, 57.95) * mm, "end": v(-92.1, 57.46) * mm});
            skArc(sketch, "E66.7.47.0", {"start": v(-91.46, 58.47) * mm, "mid": v(-92.12, 58.72) * mm, "end": v(-92.82, 58.62) * mm});
            skLineSegment(sketch, "E66.11.47.0", {"start": v(-90.4, 57.72) * mm, "end": v(-91.46, 58.47) * mm});
            skLineSegment(sketch, "E66.1.48.0", {"start": v(-92.17, 54.84) * mm, "end": v(-93.32, 55.45) * mm});
            skArc(sketch, "E66.3.48.0", {"start": v(-94.07, 56.6) * mm, "mid": v(-93.84, 55.93) * mm, "end": v(-93.32, 55.45) * mm});
            skArc(sketch, "E66.7.48.0", {"start": v(-92.7, 56.47) * mm, "mid": v(-93.37, 56.7) * mm, "end": v(-94.07, 56.6) * mm});
            skLineSegment(sketch, "E66.11.48.0", {"start": v(-91.62, 55.75) * mm, "end": v(-92.7, 56.47) * mm});
            skLineSegment(sketch, "E66.1.49.0", {"start": v(-93.34, 52.83) * mm, "end": v(-94.5, 53.42) * mm});
            skArc(sketch, "E66.3.49.0", {"start": v(-95.27, 54.55) * mm, "mid": v(-95.03, 53.89) * mm, "end": v(-94.5, 53.42) * mm});
            skArc(sketch, "E66.7.49.0", {"start": v(-93.9, 54.45) * mm, "mid": v(-94.58, 54.67) * mm, "end": v(-95.27, 54.55) * mm});
            skLineSegment(sketch, "E66.11.49.0", {"start": v(-92.8, 53.75) * mm, "end": v(-93.9, 54.45) * mm});
            skLineSegment(sketch, "E66.1.50.0", {"start": v(-94.46, 50.8) * mm, "end": v(-95.63, 51.36) * mm});
            skArc(sketch, "E66.3.50.0", {"start": v(-96.43, 52.47) * mm, "mid": v(-96.17, 51.82) * mm, "end": v(-95.63, 51.36) * mm});
            skArc(sketch, "E66.7.50.0", {"start": v(-95.06, 52.4) * mm, "mid": v(-95.74, 52.6) * mm, "end": v(-96.43, 52.47) * mm});
            skLineSegment(sketch, "E66.11.50.0", {"start": v(-93.95, 51.73) * mm, "end": v(-95.06, 52.4) * mm});
            skLineSegment(sketch, "E66.1.51.0", {"start": v(-95.54, 48.73) * mm, "end": v(-96.72, 49.28) * mm});
            skArc(sketch, "E66.3.51.0", {"start": v(-97.55, 50.37) * mm, "mid": v(-97.27, 49.72) * mm, "end": v(-96.72, 49.28) * mm});
            skArc(sketch, "E66.7.51.0", {"start": v(-96.18, 50.33) * mm, "mid": v(-96.86, 50.52) * mm, "end": v(-97.55, 50.37) * mm});
            skLineSegment(sketch, "E66.11.51.0", {"start": v(-95.05, 49.68) * mm, "end": v(-96.18, 50.33) * mm});
            skLineSegment(sketch, "E66.1.52.0", {"start": v(-96.57, 46.65) * mm, "end": v(-97.77, 47.17) * mm});
            skArc(sketch, "E66.3.52.0", {"start": v(-98.62, 48.25) * mm, "mid": v(-98.33, 47.6) * mm, "end": v(-97.77, 47.17) * mm});
            skArc(sketch, "E66.7.52.0", {"start": v(-97.25, 48.24) * mm, "mid": v(-97.93, 48.41) * mm, "end": v(-98.62, 48.25) * mm});
            skLineSegment(sketch, "E66.11.52.0", {"start": v(-96.1, 47.61) * mm, "end": v(-97.25, 48.24) * mm});
            skLineSegment(sketch, "E66.1.53.0", {"start": v(-97.56, 44.55) * mm, "end": v(-98.77, 45.04) * mm});
            skArc(sketch, "E66.3.53.0", {"start": v(-99.64, 46.1) * mm, "mid": v(-99.34, 45.46) * mm, "end": v(-98.77, 45.04) * mm});
            skArc(sketch, "E66.7.53.0", {"start": v(-98.27, 46.12) * mm, "mid": v(-98.96, 46.28) * mm, "end": v(-99.64, 46.1) * mm});
            skLineSegment(sketch, "E66.11.53.0", {"start": v(-97.11, 45.52) * mm, "end": v(-98.27, 46.12) * mm});
            skLineSegment(sketch, "E66.1.54.0", {"start": v(-98.5, 42.42) * mm, "end": v(-99.72, 42.89) * mm});
            skArc(sketch, "E66.3.54.0", {"start": v(-100.61, 43.93) * mm, "mid": v(-100.3, 43.3) * mm, "end": v(-99.72, 42.89) * mm});
            skArc(sketch, "E66.7.54.0", {"start": v(-99.24, 43.98) * mm, "mid": v(-99.93, 44.13) * mm, "end": v(-100.61, 43.93) * mm});
            skLineSegment(sketch, "E66.11.54.0", {"start": v(-98.08, 43.4) * mm, "end": v(-99.24, 43.98) * mm});
            skLineSegment(sketch, "E66.1.55.0", {"start": v(-99.4, 40.28) * mm, "end": v(-100.62, 40.72) * mm});
            skArc(sketch, "E66.3.55.0", {"start": v(-101.54, 41.74) * mm, "mid": v(-101.21, 41.11) * mm, "end": v(-100.62, 40.72) * mm});
            skArc(sketch, "E66.7.55.0", {"start": v(-100.17, 41.82) * mm, "mid": v(-100.87, 41.95) * mm, "end": v(-101.54, 41.74) * mm});
            skLineSegment(sketch, "E66.11.55.0", {"start": v(-99, 41.27) * mm, "end": v(-100.17, 41.82) * mm});
            skLineSegment(sketch, "E66.1.56.0", {"start": v(-100.25, 38.12) * mm, "end": v(-101.48, 38.53) * mm});
            skArc(sketch, "E66.3.56.0", {"start": v(-102.42, 39.53) * mm, "mid": v(-102.08, 38.91) * mm, "end": v(-101.48, 38.53) * mm});
            skArc(sketch, "E66.7.56.0", {"start": v(-101.06, 39.64) * mm, "mid": v(-101.75, 39.75) * mm, "end": v(-102.42, 39.53) * mm});
            skLineSegment(sketch, "E66.11.56.0", {"start": v(-99.86, 39.11) * mm, "end": v(-101.06, 39.64) * mm});
            skLineSegment(sketch, "E66.1.57.0", {"start": v(-101.05, 35.94) * mm, "end": v(-102.3, 36.32) * mm});
            skArc(sketch, "E66.3.57.0", {"start": v(-103.25, 37.3) * mm, "mid": v(-102.9, 36.7) * mm, "end": v(-102.3, 36.32) * mm});
            skArc(sketch, "E66.7.57.0", {"start": v(-101.9, 37.44) * mm, "mid": v(-102.59, 37.54) * mm, "end": v(-103.25, 37.3) * mm});
            skLineSegment(sketch, "E66.11.57.0", {"start": v(-100.69, 36.94) * mm, "end": v(-101.9, 37.44) * mm});
            skLineSegment(sketch, "E66.1.58.0", {"start": v(-101.8, 33.74) * mm, "end": v(-103.06, 34.1) * mm});
            skArc(sketch, "E66.3.58.0", {"start": v(-104.04, 35.05) * mm, "mid": v(-103.67, 34.45) * mm, "end": v(-103.06, 34.1) * mm});
            skArc(sketch, "E66.7.58.0", {"start": v(-102.68, 35.22) * mm, "mid": v(-103.38, 35.3) * mm, "end": v(-104.04, 35.05) * mm});
            skLineSegment(sketch, "E66.11.58.0", {"start": v(-101.46, 34.75) * mm, "end": v(-102.68, 35.22) * mm});
            skLineSegment(sketch, "E66.1.59.0", {"start": v(-102.51, 31.53) * mm, "end": v(-103.77, 31.86) * mm});
            skArc(sketch, "E66.3.59.0", {"start": v(-104.77, 32.8) * mm, "mid": v(-104.39, 32.2) * mm, "end": v(-103.77, 31.86) * mm});
            skArc(sketch, "E66.7.59.0", {"start": v(-103.42, 32.99) * mm, "mid": v(-104.12, 33.06) * mm, "end": v(-104.77, 32.8) * mm});
            skLineSegment(sketch, "E66.11.59.0", {"start": v(-102.2, 32.54) * mm, "end": v(-103.42, 32.99) * mm});
            skLineSegment(sketch, "E66.1.60.0", {"start": v(-103.17, 29.3) * mm, "end": v(-104.44, 29.6) * mm});
            skArc(sketch, "E66.3.60.0", {"start": v(-105.46, 30.51) * mm, "mid": v(-105.06, 29.93) * mm, "end": v(-104.44, 29.6) * mm});
            skArc(sketch, "E66.7.60.0", {"start": v(-104.1, 30.74) * mm, "mid": v(-104.81, 30.8) * mm, "end": v(-105.46, 30.51) * mm});
            skLineSegment(sketch, "E66.11.60.0", {"start": v(-102.87, 30.32) * mm, "end": v(-104.1, 30.74) * mm});
            skLineSegment(sketch, "E66.1.61.0", {"start": v(-103.78, 27.06) * mm, "end": v(-105.05, 27.33) * mm});
            skArc(sketch, "E66.3.61.0", {"start": v(-106.1, 28.22) * mm, "mid": v(-105.69, 27.65) * mm, "end": v(-105.05, 27.33) * mm});
            skArc(sketch, "E66.7.61.0", {"start": v(-104.75, 28.48) * mm, "mid": v(-105.45, 28.52) * mm, "end": v(-106.1, 28.22) * mm});
            skLineSegment(sketch, "E66.11.61.0", {"start": v(-103.5, 28.09) * mm, "end": v(-104.75, 28.48) * mm});
            skLineSegment(sketch, "E66.1.62.0", {"start": v(-104.34, 24.8) * mm, "end": v(-105.62, 25.05) * mm});
            skArc(sketch, "E66.3.62.0", {"start": v(-106.68, 25.92) * mm, "mid": v(-106.26, 25.35) * mm, "end": v(-105.62, 25.05) * mm});
            skArc(sketch, "E66.7.62.0", {"start": v(-105.34, 26.2) * mm, "mid": v(-106.05, 26.23) * mm, "end": v(-106.68, 25.92) * mm});
            skLineSegment(sketch, "E66.11.62.0", {"start": v(-104.1, 25.84) * mm, "end": v(-105.34, 26.2) * mm});
            skLineSegment(sketch, "E66.1.63.0", {"start": v(-104.86, 22.53) * mm, "end": v(-106.14, 22.76) * mm});
            skArc(sketch, "E66.3.63.0", {"start": v(-107.22, 23.6) * mm, "mid": v(-106.78, 23.04) * mm, "end": v(-106.14, 22.76) * mm});
            skArc(sketch, "E66.7.63.0", {"start": v(-105.88, 23.91) * mm, "mid": v(-106.6, 23.93) * mm, "end": v(-107.22, 23.6) * mm});
            skLineSegment(sketch, "E66.11.63.0", {"start": v(-104.63, 23.58) * mm, "end": v(-105.88, 23.91) * mm});
            skLineSegment(sketch, "E66.1.64.0", {"start": v(-105.32, 20.26) * mm, "end": v(-106.6, 20.45) * mm});
            skArc(sketch, "E66.3.64.0", {"start": v(-107.7, 21.27) * mm, "mid": v(-107.26, 20.72) * mm, "end": v(-106.6, 20.45) * mm});
            skArc(sketch, "E66.7.64.0", {"start": v(-106.38, 21.61) * mm, "mid": v(-107.08, 21.61) * mm, "end": v(-107.7, 21.27) * mm});
            skLineSegment(sketch, "E66.11.64.0", {"start": v(-105.11, 21.3) * mm, "end": v(-106.38, 21.61) * mm});
            skLineSegment(sketch, "E66.1.65.0", {"start": v(-105.73, 17.97) * mm, "end": v(-107.02, 18.14) * mm});
            skArc(sketch, "E66.3.65.0", {"start": v(-108.14, 18.93) * mm, "mid": v(-107.68, 18.4) * mm, "end": v(-107.02, 18.14) * mm});
            skArc(sketch, "E66.7.65.0", {"start": v(-106.82, 19.3) * mm, "mid": v(-107.53, 19.29) * mm, "end": v(-108.14, 18.93) * mm});
            skLineSegment(sketch, "E66.11.65.0", {"start": v(-105.55, 19.02) * mm, "end": v(-106.82, 19.3) * mm});
            skLineSegment(sketch, "E66.1.66.0", {"start": v(-106.1, 15.68) * mm, "end": v(-107.4, 15.81) * mm});
            skArc(sketch, "E66.3.66.0", {"start": v(-108.52, 16.59) * mm, "mid": v(-108.06, 16.06) * mm, "end": v(-107.4, 15.81) * mm});
            skArc(sketch, "E66.7.66.0", {"start": v(-107.21, 16.99) * mm, "mid": v(-107.92, 16.95) * mm, "end": v(-108.52, 16.59) * mm});
            skLineSegment(sketch, "E66.11.66.0", {"start": v(-105.94, 16.73) * mm, "end": v(-107.21, 16.99) * mm});
            skLineSegment(sketch, "E66.1.67.0", {"start": v(-106.41, 13.37) * mm, "end": v(-107.71, 13.48) * mm});
            skArc(sketch, "E66.3.67.0", {"start": v(-108.86, 14.23) * mm, "mid": v(-108.38, 13.71) * mm, "end": v(-107.71, 13.48) * mm});
            skArc(sketch, "E66.7.67.0", {"start": v(-107.56, 14.66) * mm, "mid": v(-108.26, 14.6) * mm, "end": v(-108.86, 14.23) * mm});
            skLineSegment(sketch, "E66.11.67.0", {"start": v(-106.27, 14.43) * mm, "end": v(-107.56, 14.66) * mm});
            skLineSegment(sketch, "E66.1.68.0", {"start": v(-106.68, 11.06) * mm, "end": v(-107.98, 11.15) * mm});
            skArc(sketch, "E66.3.68.0", {"start": v(-109.14, 11.87) * mm, "mid": v(-108.65, 11.36) * mm, "end": v(-107.98, 11.15) * mm});
            skArc(sketch, "E66.7.68.0", {"start": v(-107.85, 12.33) * mm, "mid": v(-108.55, 12.26) * mm, "end": v(-109.14, 11.87) * mm});
            skLineSegment(sketch, "E66.11.68.0", {"start": v(-106.56, 12.13) * mm, "end": v(-107.85, 12.33) * mm});
            skLineSegment(sketch, "E66.1.69.0", {"start": v(-106.9, 8.75) * mm, "end": v(-108.2, 8.8) * mm});
            skArc(sketch, "E66.3.69.0", {"start": v(-109.37, 9.5) * mm, "mid": v(-108.87, 9) * mm, "end": v(-108.2, 8.8) * mm});
            skArc(sketch, "E66.7.69.0", {"start": v(-108.1, 9.99) * mm, "mid": v(-108.8, 9.9) * mm, "end": v(-109.37, 9.5) * mm});
            skLineSegment(sketch, "E66.11.69.0", {"start": v(-106.8, 9.81) * mm, "end": v(-108.1, 9.99) * mm});
            skLineSegment(sketch, "E66.1.70.0", {"start": v(-107.06, 6.43) * mm, "end": v(-108.36, 6.46) * mm});
            skArc(sketch, "E66.3.70.0", {"start": v(-109.55, 7.13) * mm, "mid": v(-109.04, 6.64) * mm, "end": v(-108.36, 6.46) * mm});
            skArc(sketch, "E66.7.70.0", {"start": v(-108.28, 7.64) * mm, "mid": v(-108.98, 7.55) * mm, "end": v(-109.55, 7.13) * mm});
            skLineSegment(sketch, "E66.11.70.0", {"start": v(-106.99, 7.5) * mm, "end": v(-108.28, 7.64) * mm});
            skLineSegment(sketch, "E66.1.71.0", {"start": v(-107.17, 4.11) * mm, "end": v(-108.47, 4.1) * mm});
            skArc(sketch, "E66.3.71.0", {"start": v(-109.68, 4.76) * mm, "mid": v(-109.16, 4.28) * mm, "end": v(-108.47, 4.1) * mm});
            skArc(sketch, "E66.7.71.0", {"start": v(-108.42, 5.3) * mm, "mid": v(-109.12, 5.18) * mm, "end": v(-109.68, 4.76) * mm});
            skLineSegment(sketch, "E66.11.71.0", {"start": v(-107.12, 5.18) * mm, "end": v(-108.42, 5.3) * mm});
            skLineSegment(sketch, "E66.1.72.0", {"start": v(-107.24, 1.79) * mm, "end": v(-108.54, 1.76) * mm});
            skArc(sketch, "E66.3.72.0", {"start": v(-109.76, 2.38) * mm, "mid": v(-109.23, 1.91) * mm, "end": v(-108.54, 1.76) * mm});
            skArc(sketch, "E66.7.72.0", {"start": v(-108.51, 2.94) * mm, "mid": v(-109.2, 2.82) * mm, "end": v(-109.76, 2.38) * mm});
            skLineSegment(sketch, "E66.11.72.0", {"start": v(-107.21, 2.86) * mm, "end": v(-108.51, 2.94) * mm});
            skLineSegment(sketch, "E66.1.73.0", {"start": v(-107.25, -0.53) * mm, "end": v(-108.55, -0.6) * mm});
            skArc(sketch, "E66.3.73.0", {"start": v(-109.78, 0) * mm, "mid": v(-109.24, -0.45) * mm, "end": v(-108.55, -0.6) * mm});
            skArc(sketch, "E66.7.73.0", {"start": v(-108.55, 0.6) * mm, "mid": v(-109.24, 0.45) * mm, "end": v(-109.79, 0) * mm});
            skLineSegment(sketch, "E66.11.73.0", {"start": v(-107.25, 0.53) * mm, "end": v(-108.55, 0.6) * mm});
            skLineSegment(sketch, "E66.1.74.0", {"start": v(-107.21, -2.86) * mm, "end": v(-108.51, -2.94) * mm});
            skArc(sketch, "E66.3.74.0", {"start": v(-109.76, -2.38) * mm, "mid": v(-109.2, -2.82) * mm, "end": v(-108.51, -2.94) * mm});
            skArc(sketch, "E66.7.74.0", {"start": v(-108.54, -1.76) * mm, "mid": v(-109.23, -1.91) * mm, "end": v(-109.76, -2.38) * mm});
            skLineSegment(sketch, "E66.11.74.0", {"start": v(-107.24, -1.79) * mm, "end": v(-108.54, -1.76) * mm});
            skLineSegment(sketch, "E66.1.75.0", {"start": v(-107.12, -5.18) * mm, "end": v(-108.42, -5.3) * mm});
            skArc(sketch, "E66.3.75.0", {"start": v(-109.68, -4.76) * mm, "mid": v(-109.12, -5.18) * mm, "end": v(-108.42, -5.3) * mm});
            skArc(sketch, "E66.7.75.0", {"start": v(-108.47, -4.1) * mm, "mid": v(-109.16, -4.28) * mm, "end": v(-109.68, -4.76) * mm});
            skLineSegment(sketch, "E66.11.75.0", {"start": v(-107.17, -4.11) * mm, "end": v(-108.47, -4.1) * mm});
            skLineSegment(sketch, "E66.1.76.0", {"start": v(-106.99, -7.5) * mm, "end": v(-108.28, -7.64) * mm});
            skArc(sketch, "E66.3.76.0", {"start": v(-109.55, -7.13) * mm, "mid": v(-108.98, -7.55) * mm, "end": v(-108.28, -7.64) * mm});
            skArc(sketch, "E66.7.76.0", {"start": v(-108.36, -6.46) * mm, "mid": v(-109.04, -6.64) * mm, "end": v(-109.55, -7.13) * mm});
            skLineSegment(sketch, "E66.11.76.0", {"start": v(-107.06, -6.43) * mm, "end": v(-108.36, -6.46) * mm});
            skLineSegment(sketch, "E66.1.77.0", {"start": v(-106.8, -9.81) * mm, "end": v(-108.1, -9.99) * mm});
            skArc(sketch, "E66.3.77.0", {"start": v(-109.37, -9.5) * mm, "mid": v(-108.8, -9.9) * mm, "end": v(-108.1, -9.99) * mm});
            skArc(sketch, "E66.7.77.0", {"start": v(-108.2, -8.8) * mm, "mid": v(-108.87, -9) * mm, "end": v(-109.37, -9.5) * mm});
            skLineSegment(sketch, "E66.11.77.0", {"start": v(-106.9, -8.75) * mm, "end": v(-108.2, -8.8) * mm});
            skLineSegment(sketch, "E66.1.78.0", {"start": v(-106.56, -12.13) * mm, "end": v(-107.85, -12.33) * mm});
            skArc(sketch, "E66.3.78.0", {"start": v(-109.14, -11.87) * mm, "mid": v(-108.55, -12.26) * mm, "end": v(-107.85, -12.33) * mm});
            skArc(sketch, "E66.7.78.0", {"start": v(-107.98, -11.15) * mm, "mid": v(-108.65, -11.36) * mm, "end": v(-109.14, -11.87) * mm});
            skLineSegment(sketch, "E66.11.78.0", {"start": v(-106.68, -11.06) * mm, "end": v(-107.98, -11.15) * mm});
            skLineSegment(sketch, "E66.1.79.0", {"start": v(-106.27, -14.43) * mm, "end": v(-107.56, -14.66) * mm});
            skArc(sketch, "E66.3.79.0", {"start": v(-108.86, -14.23) * mm, "mid": v(-108.26, -14.6) * mm, "end": v(-107.56, -14.66) * mm});
            skArc(sketch, "E66.7.79.0", {"start": v(-107.71, -13.48) * mm, "mid": v(-108.38, -13.71) * mm, "end": v(-108.86, -14.23) * mm});
            skLineSegment(sketch, "E66.11.79.0", {"start": v(-106.41, -13.37) * mm, "end": v(-107.71, -13.48) * mm});
            skLineSegment(sketch, "E66.1.80.0", {"start": v(-105.94, -16.73) * mm, "end": v(-107.21, -16.99) * mm});
            skArc(sketch, "E66.3.80.0", {"start": v(-108.52, -16.59) * mm, "mid": v(-107.92, -16.95) * mm, "end": v(-107.21, -16.99) * mm});
            skArc(sketch, "E66.7.80.0", {"start": v(-107.4, -15.81) * mm, "mid": v(-108.06, -16.06) * mm, "end": v(-108.52, -16.59) * mm});
            skLineSegment(sketch, "E66.11.80.0", {"start": v(-106.1, -15.68) * mm, "end": v(-107.4, -15.81) * mm});
            skLineSegment(sketch, "E66.1.81.0", {"start": v(-105.55, -19.02) * mm, "end": v(-106.82, -19.3) * mm});
            skArc(sketch, "E66.3.81.0", {"start": v(-108.14, -18.93) * mm, "mid": v(-107.53, -19.29) * mm, "end": v(-106.82, -19.3) * mm});
            skArc(sketch, "E66.7.81.0", {"start": v(-107.02, -18.14) * mm, "mid": v(-107.68, -18.4) * mm, "end": v(-108.14, -18.93) * mm});
            skLineSegment(sketch, "E66.11.81.0", {"start": v(-105.73, -17.97) * mm, "end": v(-107.02, -18.14) * mm});
            skLineSegment(sketch, "E66.1.82.0", {"start": v(-105.11, -21.3) * mm, "end": v(-106.38, -21.61) * mm});
            skArc(sketch, "E66.3.82.0", {"start": v(-107.7, -21.27) * mm, "mid": v(-107.08, -21.61) * mm, "end": v(-106.38, -21.61) * mm});
            skArc(sketch, "E66.7.82.0", {"start": v(-106.6, -20.45) * mm, "mid": v(-107.26, -20.72) * mm, "end": v(-107.7, -21.27) * mm});
            skLineSegment(sketch, "E66.11.82.0", {"start": v(-105.32, -20.26) * mm, "end": v(-106.6, -20.45) * mm});
            skLineSegment(sketch, "E66.1.83.0", {"start": v(-104.63, -23.58) * mm, "end": v(-105.88, -23.91) * mm});
            skArc(sketch, "E66.3.83.0", {"start": v(-107.22, -23.6) * mm, "mid": v(-106.6, -23.93) * mm, "end": v(-105.88, -23.91) * mm});
            skArc(sketch, "E66.7.83.0", {"start": v(-106.14, -22.76) * mm, "mid": v(-106.78, -23.04) * mm, "end": v(-107.22, -23.6) * mm});
            skLineSegment(sketch, "E66.11.83.0", {"start": v(-104.86, -22.53) * mm, "end": v(-106.14, -22.76) * mm});
            skLineSegment(sketch, "E66.1.84.0", {"start": v(-104.1, -25.84) * mm, "end": v(-105.34, -26.2) * mm});
            skArc(sketch, "E66.3.84.0", {"start": v(-106.68, -25.92) * mm, "mid": v(-106.05, -26.23) * mm, "end": v(-105.34, -26.2) * mm});
            skArc(sketch, "E66.7.84.0", {"start": v(-105.62, -25.05) * mm, "mid": v(-106.26, -25.35) * mm, "end": v(-106.68, -25.92) * mm});
            skLineSegment(sketch, "E66.11.84.0", {"start": v(-104.34, -24.8) * mm, "end": v(-105.62, -25.05) * mm});
            skLineSegment(sketch, "E66.1.85.0", {"start": v(-103.5, -28.09) * mm, "end": v(-104.75, -28.48) * mm});
            skArc(sketch, "E66.3.85.0", {"start": v(-106.1, -28.22) * mm, "mid": v(-105.45, -28.52) * mm, "end": v(-104.75, -28.48) * mm});
            skArc(sketch, "E66.7.85.0", {"start": v(-105.05, -27.33) * mm, "mid": v(-105.69, -27.65) * mm, "end": v(-106.1, -28.22) * mm});
            skLineSegment(sketch, "E66.11.85.0", {"start": v(-103.78, -27.06) * mm, "end": v(-105.05, -27.33) * mm});
            skLineSegment(sketch, "E66.1.86.0", {"start": v(-102.87, -30.32) * mm, "end": v(-104.1, -30.74) * mm});
            skArc(sketch, "E66.3.86.0", {"start": v(-105.46, -30.51) * mm, "mid": v(-104.81, -30.8) * mm, "end": v(-104.1, -30.74) * mm});
            skArc(sketch, "E66.7.86.0", {"start": v(-104.44, -29.6) * mm, "mid": v(-105.06, -29.93) * mm, "end": v(-105.46, -30.51) * mm});
            skLineSegment(sketch, "E66.11.86.0", {"start": v(-103.17, -29.3) * mm, "end": v(-104.44, -29.6) * mm});
            skLineSegment(sketch, "E66.1.87.0", {"start": v(-102.2, -32.54) * mm, "end": v(-103.42, -32.99) * mm});
            skArc(sketch, "E66.3.87.0", {"start": v(-104.77, -32.8) * mm, "mid": v(-104.12, -33.06) * mm, "end": v(-103.42, -32.99) * mm});
            skArc(sketch, "E66.7.87.0", {"start": v(-103.77, -31.86) * mm, "mid": v(-104.39, -32.2) * mm, "end": v(-104.77, -32.8) * mm});
            skLineSegment(sketch, "E66.11.87.0", {"start": v(-102.51, -31.53) * mm, "end": v(-103.77, -31.86) * mm});
            skLineSegment(sketch, "E66.1.88.0", {"start": v(-101.46, -34.75) * mm, "end": v(-102.68, -35.22) * mm});
            skArc(sketch, "E66.3.88.0", {"start": v(-104.04, -35.05) * mm, "mid": v(-103.38, -35.3) * mm, "end": v(-102.68, -35.22) * mm});
            skArc(sketch, "E66.7.88.0", {"start": v(-103.06, -34.1) * mm, "mid": v(-103.67, -34.45) * mm, "end": v(-104.04, -35.05) * mm});
            skLineSegment(sketch, "E66.11.88.0", {"start": v(-101.8, -33.74) * mm, "end": v(-103.06, -34.1) * mm});
            skLineSegment(sketch, "E66.1.89.0", {"start": v(-100.69, -36.94) * mm, "end": v(-101.9, -37.44) * mm});
            skArc(sketch, "E66.3.89.0", {"start": v(-103.25, -37.3) * mm, "mid": v(-102.59, -37.54) * mm, "end": v(-101.9, -37.44) * mm});
            skArc(sketch, "E66.7.89.0", {"start": v(-102.3, -36.32) * mm, "mid": v(-102.9, -36.7) * mm, "end": v(-103.25, -37.3) * mm});
            skLineSegment(sketch, "E66.11.89.0", {"start": v(-101.05, -35.94) * mm, "end": v(-102.3, -36.32) * mm});
            skLineSegment(sketch, "E66.1.90.0", {"start": v(-99.86, -39.11) * mm, "end": v(-101.06, -39.64) * mm});
            skArc(sketch, "E66.3.90.0", {"start": v(-102.42, -39.53) * mm, "mid": v(-101.75, -39.75) * mm, "end": v(-101.06, -39.64) * mm});
            skArc(sketch, "E66.7.90.0", {"start": v(-101.48, -38.53) * mm, "mid": v(-102.08, -38.91) * mm, "end": v(-102.42, -39.53) * mm});
            skLineSegment(sketch, "E66.11.90.0", {"start": v(-100.25, -38.12) * mm, "end": v(-101.48, -38.53) * mm});
            skLineSegment(sketch, "E66.1.91.0", {"start": v(-99, -41.27) * mm, "end": v(-100.17, -41.82) * mm});
            skArc(sketch, "E66.3.91.0", {"start": v(-101.54, -41.74) * mm, "mid": v(-100.87, -41.95) * mm, "end": v(-100.17, -41.82) * mm});
            skArc(sketch, "E66.7.91.0", {"start": v(-100.62, -40.72) * mm, "mid": v(-101.21, -41.11) * mm, "end": v(-101.54, -41.74) * mm});
            skLineSegment(sketch, "E66.11.91.0", {"start": v(-99.4, -40.28) * mm, "end": v(-100.62, -40.72) * mm});
            skLineSegment(sketch, "E66.1.92.0", {"start": v(-98.08, -43.4) * mm, "end": v(-99.24, -43.98) * mm});
            skArc(sketch, "E66.3.92.0", {"start": v(-100.61, -43.93) * mm, "mid": v(-99.93, -44.13) * mm, "end": v(-99.24, -43.98) * mm});
            skArc(sketch, "E66.7.92.0", {"start": v(-99.72, -42.89) * mm, "mid": v(-100.3, -43.3) * mm, "end": v(-100.61, -43.93) * mm});
            skLineSegment(sketch, "E66.11.92.0", {"start": v(-98.5, -42.42) * mm, "end": v(-99.72, -42.89) * mm});
            skLineSegment(sketch, "E66.1.93.0", {"start": v(-97.11, -45.52) * mm, "end": v(-98.27, -46.12) * mm});
            skArc(sketch, "E66.3.93.0", {"start": v(-99.64, -46.1) * mm, "mid": v(-98.96, -46.28) * mm, "end": v(-98.27, -46.12) * mm});
            skArc(sketch, "E66.7.93.0", {"start": v(-98.77, -45.04) * mm, "mid": v(-99.34, -45.46) * mm, "end": v(-99.64, -46.1) * mm});
            skLineSegment(sketch, "E66.11.93.0", {"start": v(-97.56, -44.55) * mm, "end": v(-98.77, -45.04) * mm});
            skLineSegment(sketch, "E66.1.94.0", {"start": v(-96.1, -47.61) * mm, "end": v(-97.25, -48.24) * mm});
            skArc(sketch, "E66.3.94.0", {"start": v(-98.62, -48.25) * mm, "mid": v(-97.93, -48.41) * mm, "end": v(-97.25, -48.24) * mm});
            skArc(sketch, "E66.7.94.0", {"start": v(-97.77, -47.17) * mm, "mid": v(-98.33, -47.6) * mm, "end": v(-98.62, -48.25) * mm});
            skLineSegment(sketch, "E66.11.94.0", {"start": v(-96.57, -46.65) * mm, "end": v(-97.77, -47.17) * mm});
            skLineSegment(sketch, "E66.1.95.0", {"start": v(-95.05, -49.68) * mm, "end": v(-96.18, -50.33) * mm});
            skArc(sketch, "E66.3.95.0", {"start": v(-97.55, -50.37) * mm, "mid": v(-96.86, -50.52) * mm, "end": v(-96.18, -50.33) * mm});
            skArc(sketch, "E66.7.95.0", {"start": v(-96.72, -49.28) * mm, "mid": v(-97.27, -49.72) * mm, "end": v(-97.55, -50.37) * mm});
            skLineSegment(sketch, "E66.11.95.0", {"start": v(-95.54, -48.73) * mm, "end": v(-96.72, -49.28) * mm});
            skLineSegment(sketch, "E66.1.96.0", {"start": v(-93.95, -51.73) * mm, "end": v(-95.06, -52.4) * mm});
            skArc(sketch, "E66.3.96.0", {"start": v(-96.43, -52.47) * mm, "mid": v(-95.74, -52.6) * mm, "end": v(-95.06, -52.4) * mm});
            skArc(sketch, "E66.7.96.0", {"start": v(-95.63, -51.36) * mm, "mid": v(-96.17, -51.82) * mm, "end": v(-96.43, -52.47) * mm});
            skLineSegment(sketch, "E66.11.96.0", {"start": v(-94.46, -50.8) * mm, "end": v(-95.63, -51.36) * mm});
            skLineSegment(sketch, "E66.1.97.0", {"start": v(-92.8, -53.75) * mm, "end": v(-93.9, -54.45) * mm});
            skArc(sketch, "E66.3.97.0", {"start": v(-95.27, -54.55) * mm, "mid": v(-94.58, -54.67) * mm, "end": v(-93.9, -54.45) * mm});
            skArc(sketch, "E66.7.97.0", {"start": v(-94.5, -53.42) * mm, "mid": v(-95.03, -53.89) * mm, "end": v(-95.27, -54.55) * mm});
            skLineSegment(sketch, "E66.11.97.0", {"start": v(-93.34, -52.83) * mm, "end": v(-94.5, -53.42) * mm});
            skLineSegment(sketch, "E66.1.98.0", {"start": v(-91.62, -55.75) * mm, "end": v(-92.7, -56.47) * mm});
            skArc(sketch, "E66.3.98.0", {"start": v(-94.07, -56.6) * mm, "mid": v(-93.37, -56.7) * mm, "end": v(-92.7, -56.47) * mm});
            skArc(sketch, "E66.7.98.0", {"start": v(-93.32, -55.45) * mm, "mid": v(-93.84, -55.93) * mm, "end": v(-94.07, -56.6) * mm});
            skLineSegment(sketch, "E66.11.98.0", {"start": v(-92.17, -54.84) * mm, "end": v(-93.32, -55.45) * mm});
            skLineSegment(sketch, "E66.1.99.0", {"start": v(-90.4, -57.72) * mm, "end": v(-91.46, -58.47) * mm});
            skArc(sketch, "E66.3.99.0", {"start": v(-92.82, -58.62) * mm, "mid": v(-92.12, -58.72) * mm, "end": v(-91.46, -58.47) * mm});
            skArc(sketch, "E66.7.99.0", {"start": v(-92.1, -57.46) * mm, "mid": v(-92.6, -57.95) * mm, "end": v(-92.82, -58.62) * mm});
            skLineSegment(sketch, "E66.11.99.0", {"start": v(-90.96, -56.82) * mm, "end": v(-92.1, -57.46) * mm});
            skLineSegment(sketch, "E66.1.100.0", {"start": v(-89.12, -59.67) * mm, "end": v(-90.17, -60.43) * mm});
            skArc(sketch, "E66.3.100.0", {"start": v(-91.53, -60.62) * mm, "mid": v(-90.83, -60.7) * mm, "end": v(-90.17, -60.43) * mm});
            skArc(sketch, "E66.7.100.0", {"start": v(-90.83, -59.44) * mm, "mid": v(-91.33, -59.94) * mm, "end": v(-91.53, -60.62) * mm});
            skLineSegment(sketch, "E66.11.100.0", {"start": v(-89.71, -58.78) * mm, "end": v(-90.83, -59.44) * mm});
            skLineSegment(sketch, "E66.1.101.0", {"start": v(-87.8, -61.58) * mm, "end": v(-88.84, -62.37) * mm});
            skArc(sketch, "E66.3.101.0", {"start": v(-90.2, -62.6) * mm, "mid": v(-89.5, -62.65) * mm, "end": v(-88.84, -62.37) * mm});
            skArc(sketch, "E66.7.101.0", {"start": v(-89.52, -61.4) * mm, "mid": v(-90, -61.9) * mm, "end": v(-90.2, -62.6) * mm});
            skLineSegment(sketch, "E66.11.101.0", {"start": v(-88.42, -60.7) * mm, "end": v(-89.52, -61.4) * mm});
            skLineSegment(sketch, "E66.1.102.0", {"start": v(-86.45, -63.47) * mm, "end": v(-87.47, -64.28) * mm});
            skArc(sketch, "E66.3.102.0", {"start": v(-88.82, -64.53) * mm, "mid": v(-88.11, -64.58) * mm, "end": v(-87.47, -64.28) * mm});
            skArc(sketch, "E66.7.102.0", {"start": v(-88.17, -63.32) * mm, "mid": v(-88.64, -63.84) * mm, "end": v(-88.82, -64.53) * mm});
            skLineSegment(sketch, "E66.11.102.0", {"start": v(-87.08, -62.6) * mm, "end": v(-88.17, -63.32) * mm});
            skLineSegment(sketch, "E66.1.103.0", {"start": v(-85.06, -65.33) * mm, "end": v(-86.06, -66.16) * mm});
            skArc(sketch, "E66.3.103.0", {"start": v(-87.4, -66.44) * mm, "mid": v(-86.7, -66.47) * mm, "end": v(-86.06, -66.16) * mm});
            skArc(sketch, "E66.7.103.0", {"start": v(-86.77, -65.22) * mm, "mid": v(-87.24, -65.75) * mm, "end": v(-87.4, -66.44) * mm});
            skLineSegment(sketch, "E66.11.103.0", {"start": v(-85.7, -64.48) * mm, "end": v(-86.77, -65.22) * mm});
            skLineSegment(sketch, "E66.1.104.0", {"start": v(-83.62, -67.16) * mm, "end": v(-84.6, -68.01) * mm});
            skArc(sketch, "E66.3.104.0", {"start": v(-85.94, -68.32) * mm, "mid": v(-85.23, -68.33) * mm, "end": v(-84.6, -68.01) * mm});
            skArc(sketch, "E66.7.104.0", {"start": v(-85.34, -67.08) * mm, "mid": v(-85.8, -67.62) * mm, "end": v(-85.94, -68.32) * mm});
            skLineSegment(sketch, "E66.11.104.0", {"start": v(-84.29, -66.32) * mm, "end": v(-85.34, -67.08) * mm});
            skLineSegment(sketch, "E66.1.105.0", {"start": v(-82.15, -68.95) * mm, "end": v(-83.1, -69.83) * mm});
            skArc(sketch, "E66.3.105.0", {"start": v(-84.44, -70.16) * mm, "mid": v(-83.73, -70.16) * mm, "end": v(-83.1, -69.83) * mm});
            skArc(sketch, "E66.7.105.0", {"start": v(-83.87, -68.92) * mm, "mid": v(-84.31, -69.47) * mm, "end": v(-84.44, -70.16) * mm});
            skLineSegment(sketch, "E66.11.105.0", {"start": v(-82.83, -68.13) * mm, "end": v(-83.87, -68.92) * mm});
            skLineSegment(sketch, "E66.1.106.0", {"start": v(-80.63, -70.72) * mm, "end": v(-81.58, -71.61) * mm});
            skArc(sketch, "E66.3.106.0", {"start": v(-82.9, -71.98) * mm, "mid": v(-82.2, -71.96) * mm, "end": v(-81.58, -71.61) * mm});
            skArc(sketch, "E66.7.106.0", {"start": v(-82.35, -70.72) * mm, "mid": v(-82.79, -71.28) * mm, "end": v(-82.9, -71.98) * mm});
            skLineSegment(sketch, "E66.11.106.0", {"start": v(-81.33, -69.9) * mm, "end": v(-82.35, -70.72) * mm});
            skLineSegment(sketch, "E66.1.107.0", {"start": v(-79.08, -72.45) * mm, "end": v(-80, -73.36) * mm});
            skArc(sketch, "E66.3.107.0", {"start": v(-81.32, -73.75) * mm, "mid": v(-80.61, -73.72) * mm, "end": v(-80, -73.36) * mm});
            skArc(sketch, "E66.7.107.0", {"start": v(-80.8, -72.48) * mm, "mid": v(-81.22, -73.05) * mm, "end": v(-81.32, -73.75) * mm});
            skLineSegment(sketch, "E66.11.107.0", {"start": v(-79.8, -71.66) * mm, "end": v(-80.8, -72.48) * mm});
            skLineSegment(sketch, "E66.1.108.0", {"start": v(-77.5, -74.14) * mm, "end": v(-78.4, -75.08) * mm});
            skArc(sketch, "E66.3.108.0", {"start": v(-79.7, -75.5) * mm, "mid": v(-79, -75.45) * mm, "end": v(-78.4, -75.08) * mm});
            skArc(sketch, "E66.7.108.0", {"start": v(-79.21, -74.22) * mm, "mid": v(-79.62, -74.8) * mm, "end": v(-79.7, -75.5) * mm});
            skLineSegment(sketch, "E66.11.108.0", {"start": v(-78.23, -73.37) * mm, "end": v(-79.21, -74.22) * mm});
            skLineSegment(sketch, "E66.1.109.0", {"start": v(-75.87, -75.8) * mm, "end": v(-76.75, -76.76) * mm});
            skArc(sketch, "E66.3.109.0", {"start": v(-78.05, -77.2) * mm, "mid": v(-77.34, -77.15) * mm, "end": v(-76.75, -76.76) * mm});
            skArc(sketch, "E66.7.109.0", {"start": v(-77.59, -75.92) * mm, "mid": v(-77.98, -76.5) * mm, "end": v(-78.05, -77.2) * mm});
            skLineSegment(sketch, "E66.11.109.0", {"start": v(-76.62, -75.04) * mm, "end": v(-77.59, -75.92) * mm});
            skLineSegment(sketch, "E66.1.110.0", {"start": v(-74.21, -77.43) * mm, "end": v(-75.07, -78.4) * mm});
            skArc(sketch, "E66.3.110.0", {"start": v(-76.36, -78.88) * mm, "mid": v(-75.66, -78.8) * mm, "end": v(-75.07, -78.4) * mm});
            skArc(sketch, "E66.7.110.0", {"start": v(-75.92, -77.58) * mm, "mid": v(-76.3, -78.18) * mm, "end": v(-76.36, -78.88) * mm});
            skLineSegment(sketch, "E66.11.110.0", {"start": v(-74.98, -76.69) * mm, "end": v(-75.92, -77.58) * mm});
            skLineSegment(sketch, "E66.1.111.0", {"start": v(-72.52, -79.02) * mm, "end": v(-73.36, -80.01) * mm});
            skArc(sketch, "E66.3.111.0", {"start": v(-74.63, -80.52) * mm, "mid": v(-73.93, -80.43) * mm, "end": v(-73.36, -80.01) * mm});
            skArc(sketch, "E66.7.111.0", {"start": v(-74.23, -79.2) * mm, "mid": v(-74.6, -79.81) * mm, "end": v(-74.63, -80.52) * mm});
            skLineSegment(sketch, "E66.11.111.0", {"start": v(-73.3, -78.3) * mm, "end": v(-74.23, -79.2) * mm});
            skLineSegment(sketch, "E66.1.112.0", {"start": v(-70.79, -80.57) * mm, "end": v(-71.6, -81.58) * mm});
            skArc(sketch, "E66.3.112.0", {"start": v(-72.87, -82.11) * mm, "mid": v(-72.17, -82) * mm, "end": v(-71.6, -81.58) * mm});
            skArc(sketch, "E66.7.112.0", {"start": v(-72.5, -80.8) * mm, "mid": v(-72.85, -81.4) * mm, "end": v(-72.87, -82.11) * mm});
            skLineSegment(sketch, "E66.11.112.0", {"start": v(-71.59, -79.86) * mm, "end": v(-72.5, -80.8) * mm});
            skLineSegment(sketch, "E66.1.113.0", {"start": v(-69.02, -82.09) * mm, "end": v(-69.82, -83.12) * mm});
            skArc(sketch, "E66.3.113.0", {"start": v(-71.07, -83.67) * mm, "mid": v(-70.38, -83.55) * mm, "end": v(-69.82, -83.12) * mm});
            skArc(sketch, "E66.7.113.0", {"start": v(-70.73, -82.35) * mm, "mid": v(-71.07, -82.97) * mm, "end": v(-71.07, -83.67) * mm});
            skLineSegment(sketch, "E66.11.113.0", {"start": v(-69.84, -81.4) * mm, "end": v(-70.73, -82.35) * mm});
            skLineSegment(sketch, "E66.1.114.0", {"start": v(-67.23, -83.56) * mm, "end": v(-68, -84.6) * mm});
            skArc(sketch, "E66.3.114.0", {"start": v(-69.24, -85.2) * mm, "mid": v(-68.55, -85.06) * mm, "end": v(-68, -84.6) * mm});
            skArc(sketch, "E66.7.114.0", {"start": v(-68.92, -83.86) * mm, "mid": v(-69.25, -84.49) * mm, "end": v(-69.24, -85.2) * mm});
            skLineSegment(sketch, "E66.11.114.0", {"start": v(-68.06, -82.89) * mm, "end": v(-68.92, -83.86) * mm});
            skLineSegment(sketch, "E66.1.115.0", {"start": v(-65.4, -85) * mm, "end": v(-66.15, -86.06) * mm});
            skArc(sketch, "E66.3.115.0", {"start": v(-67.38, -86.67) * mm, "mid": v(-66.7, -86.52) * mm, "end": v(-66.15, -86.06) * mm});
            skArc(sketch, "E66.7.115.0", {"start": v(-67.1, -85.33) * mm, "mid": v(-67.4, -85.97) * mm, "end": v(-67.38, -86.67) * mm});
            skLineSegment(sketch, "E66.11.115.0", {"start": v(-66.25, -84.34) * mm, "end": v(-67.1, -85.33) * mm});
            skLineSegment(sketch, "E66.1.116.0", {"start": v(-63.55, -86.4) * mm, "end": v(-64.27, -87.48) * mm});
            skArc(sketch, "E66.3.116.0", {"start": v(-65.49, -88.11) * mm, "mid": v(-64.8, -87.95) * mm, "end": v(-64.27, -87.48) * mm});
            skArc(sketch, "E66.7.116.0", {"start": v(-65.23, -86.77) * mm, "mid": v(-65.53, -87.4) * mm, "end": v(-65.49, -88.11) * mm});
            skLineSegment(sketch, "E66.11.116.0", {"start": v(-64.4, -85.76) * mm, "end": v(-65.23, -86.77) * mm});
            skLineSegment(sketch, "E66.1.117.0", {"start": v(-61.66, -87.75) * mm, "end": v(-62.36, -88.85) * mm});
            skArc(sketch, "E66.3.117.0", {"start": v(-63.56, -89.51) * mm, "mid": v(-62.88, -89.33) * mm, "end": v(-62.36, -88.85) * mm});
            skArc(sketch, "E66.7.117.0", {"start": v(-63.33, -88.16) * mm, "mid": v(-63.62, -88.8) * mm, "end": v(-63.56, -89.51) * mm});
            skLineSegment(sketch, "E66.11.117.0", {"start": v(-62.53, -87.13) * mm, "end": v(-63.33, -88.16) * mm});
            skLineSegment(sketch, "E66.1.118.0", {"start": v(-59.74, -89.07) * mm, "end": v(-60.43, -90.18) * mm});
            skArc(sketch, "E66.3.118.0", {"start": v(-61.6, -90.87) * mm, "mid": v(-60.93, -90.67) * mm, "end": v(-60.43, -90.18) * mm});
            skArc(sketch, "E66.7.118.0", {"start": v(-61.4, -89.51) * mm, "mid": v(-61.68, -90.16) * mm, "end": v(-61.6, -90.87) * mm});
            skLineSegment(sketch, "E66.11.118.0", {"start": v(-60.63, -88.47) * mm, "end": v(-61.4, -89.51) * mm});
            skLineSegment(sketch, "E66.1.119.0", {"start": v(-57.8, -90.34) * mm, "end": v(-58.46, -91.47) * mm});
            skArc(sketch, "E66.3.119.0", {"start": v(-59.63, -92.18) * mm, "mid": v(-58.95, -91.97) * mm, "end": v(-58.46, -91.47) * mm});
            skArc(sketch, "E66.7.119.0", {"start": v(-59.45, -90.82) * mm, "mid": v(-59.71, -91.48) * mm, "end": v(-59.63, -92.18) * mm});
            skLineSegment(sketch, "E66.11.119.0", {"start": v(-58.7, -89.76) * mm, "end": v(-59.45, -90.82) * mm});
            skLineSegment(sketch, "E66.1.120.0", {"start": v(-55.83, -91.57) * mm, "end": v(-56.46, -92.71) * mm});
            skArc(sketch, "E66.3.120.0", {"start": v(-57.62, -93.45) * mm, "mid": v(-56.95, -93.23) * mm, "end": v(-56.46, -92.71) * mm});
            skArc(sketch, "E66.7.120.0", {"start": v(-57.47, -92.09) * mm, "mid": v(-57.72, -92.75) * mm, "end": v(-57.62, -93.45) * mm});
            skLineSegment(sketch, "E66.11.120.0", {"start": v(-56.74, -91.01) * mm, "end": v(-57.47, -92.09) * mm});
            skLineSegment(sketch, "E66.1.121.0", {"start": v(-53.83, -92.76) * mm, "end": v(-54.44, -93.91) * mm});
            skArc(sketch, "E66.3.121.0", {"start": v(-55.58, -94.68) * mm, "mid": v(-54.91, -94.44) * mm, "end": v(-54.44, -93.91) * mm});
            skArc(sketch, "E66.7.121.0", {"start": v(-55.46, -93.31) * mm, "mid": v(-55.7, -93.98) * mm, "end": v(-55.58, -94.68) * mm});
            skLineSegment(sketch, "E66.11.121.0", {"start": v(-54.75, -92.22) * mm, "end": v(-55.46, -93.31) * mm});
            skLineSegment(sketch, "E66.1.122.0", {"start": v(-51.81, -93.9) * mm, "end": v(-52.4, -95.07) * mm});
            skArc(sketch, "E66.3.122.0", {"start": v(-53.51, -95.86) * mm, "mid": v(-52.85, -95.6) * mm, "end": v(-52.4, -95.07) * mm});
            skArc(sketch, "E66.7.122.0", {"start": v(-53.43, -94.5) * mm, "mid": v(-53.64, -95.16) * mm, "end": v(-53.51, -95.86) * mm});
            skLineSegment(sketch, "E66.11.122.0", {"start": v(-52.74, -93.38) * mm, "end": v(-53.43, -94.5) * mm});
            skLineSegment(sketch, "E66.1.123.0", {"start": v(-49.76, -95) * mm, "end": v(-50.32, -96.18) * mm});
            skArc(sketch, "E66.3.123.0", {"start": v(-51.42, -97) * mm, "mid": v(-50.77, -96.73) * mm, "end": v(-50.32, -96.18) * mm});
            skArc(sketch, "E66.7.123.0", {"start": v(-51.37, -95.63) * mm, "mid": v(-51.57, -96.3) * mm, "end": v(-51.42, -97) * mm});
            skLineSegment(sketch, "E66.11.123.0", {"start": v(-50.7, -94.5) * mm, "end": v(-51.37, -95.63) * mm});
            skLineSegment(sketch, "E66.1.124.0", {"start": v(-47.7, -96.06) * mm, "end": v(-48.23, -97.25) * mm});
            skArc(sketch, "E66.3.124.0", {"start": v(-49.31, -98.09) * mm, "mid": v(-48.66, -97.8) * mm, "end": v(-48.23, -97.25) * mm});
            skArc(sketch, "E66.7.124.0", {"start": v(-49.29, -96.72) * mm, "mid": v(-49.47, -97.4) * mm, "end": v(-49.31, -98.09) * mm});
            skLineSegment(sketch, "E66.11.124.0", {"start": v(-48.65, -95.58) * mm, "end": v(-49.29, -96.72) * mm});
            skLineSegment(sketch, "E66.1.125.0", {"start": v(-45.6, -97.07) * mm, "end": v(-46.1, -98.27) * mm});
            skArc(sketch, "E66.3.125.0", {"start": v(-47.17, -99.13) * mm, "mid": v(-46.53, -98.84) * mm, "end": v(-46.1, -98.27) * mm});
            skArc(sketch, "E66.7.125.0", {"start": v(-47.18, -97.76) * mm, "mid": v(-47.35, -98.45) * mm, "end": v(-47.17, -99.13) * mm});
            skLineSegment(sketch, "E66.11.125.0", {"start": v(-46.57, -96.61) * mm, "end": v(-47.18, -97.76) * mm});
            skLineSegment(sketch, "E66.1.126.0", {"start": v(-43.49, -98.04) * mm, "end": v(-43.97, -99.25) * mm});
            skArc(sketch, "E66.3.126.0", {"start": v(-45.02, -100.13) * mm, "mid": v(-44.38, -99.82) * mm, "end": v(-43.97, -99.25) * mm});
            skArc(sketch, "E66.7.126.0", {"start": v(-45.05, -98.76) * mm, "mid": v(-45.2, -99.45) * mm, "end": v(-45.02, -100.13) * mm});
            skLineSegment(sketch, "E66.11.126.0", {"start": v(-44.46, -97.6) * mm, "end": v(-45.05, -98.76) * mm});
            skLineSegment(sketch, "E66.1.127.0", {"start": v(-41.35, -98.96) * mm, "end": v(-41.8, -100.18) * mm});
            skArc(sketch, "E66.3.127.0", {"start": v(-42.84, -101.08) * mm, "mid": v(-42.2, -100.76) * mm, "end": v(-41.8, -100.18) * mm});
            skArc(sketch, "E66.7.127.0", {"start": v(-42.9, -99.71) * mm, "mid": v(-43.04, -100.4) * mm, "end": v(-42.84, -101.08) * mm});
            skLineSegment(sketch, "E66.11.127.0", {"start": v(-42.34, -98.54) * mm, "end": v(-42.9, -99.71) * mm});
            skLineSegment(sketch, "E66.1.128.0", {"start": v(-39.2, -99.83) * mm, "end": v(-39.63, -101.06) * mm});
            skArc(sketch, "E66.3.128.0", {"start": v(-40.64, -101.99) * mm, "mid": v(-40.01, -101.65) * mm, "end": v(-39.63, -101.06) * mm});
            skArc(sketch, "E66.7.128.0", {"start": v(-40.73, -100.62) * mm, "mid": v(-40.85, -101.32) * mm, "end": v(-40.64, -101.99) * mm});
            skLineSegment(sketch, "E66.11.128.0", {"start": v(-40.2, -99.43) * mm, "end": v(-40.73, -100.62) * mm});
            skLineSegment(sketch, "E66.1.129.0", {"start": v(-37.03, -100.65) * mm, "end": v(-37.43, -101.9) * mm});
            skArc(sketch, "E66.3.129.0", {"start": v(-38.42, -102.84) * mm, "mid": v(-37.8, -102.5) * mm, "end": v(-37.43, -101.9) * mm});
            skArc(sketch, "E66.7.129.0", {"start": v(-38.54, -101.48) * mm, "mid": v(-38.65, -102.18) * mm, "end": v(-38.42, -102.84) * mm});
            skLineSegment(sketch, "E66.11.129.0", {"start": v(-38.03, -100.28) * mm, "end": v(-38.54, -101.48) * mm});
            skLineSegment(sketch, "E66.1.130.0", {"start": v(-34.84, -101.43) * mm, "end": v(-35.21, -102.68) * mm});
            skArc(sketch, "E66.3.130.0", {"start": v(-36.18, -103.65) * mm, "mid": v(-35.57, -103.29) * mm, "end": v(-35.21, -102.68) * mm});
            skArc(sketch, "E66.7.130.0", {"start": v(-36.33, -102.29) * mm, "mid": v(-36.43, -103) * mm, "end": v(-36.18, -103.65) * mm});
            skLineSegment(sketch, "E66.11.130.0", {"start": v(-35.85, -101.08) * mm, "end": v(-36.33, -102.29) * mm});
            skLineSegment(sketch, "E66.1.131.0", {"start": v(-32.63, -102.16) * mm, "end": v(-32.98, -103.42) * mm});
            skArc(sketch, "E66.3.131.0", {"start": v(-33.93, -104.41) * mm, "mid": v(-33.33, -104.03) * mm, "end": v(-32.98, -103.42) * mm});
            skArc(sketch, "E66.7.131.0", {"start": v(-34.1, -103.05) * mm, "mid": v(-34.19, -103.76) * mm, "end": v(-33.93, -104.41) * mm});
            skLineSegment(sketch, "E66.11.131.0", {"start": v(-33.65, -101.83) * mm, "end": v(-34.1, -103.05) * mm});
            skLineSegment(sketch, "E66.1.132.0", {"start": v(-30.41, -102.85) * mm, "end": v(-30.73, -104.1) * mm});
            skArc(sketch, "E66.3.132.0", {"start": v(-31.66, -105.12) * mm, "mid": v(-31.07, -104.73) * mm, "end": v(-30.73, -104.1) * mm});
            skArc(sketch, "E66.7.132.0", {"start": v(-31.87, -103.77) * mm, "mid": v(-31.93, -104.47) * mm, "end": v(-31.66, -105.12) * mm});
            skLineSegment(sketch, "E66.11.132.0", {"start": v(-31.44, -102.54) * mm, "end": v(-31.87, -103.77) * mm});
            skLineSegment(sketch, "E66.1.133.0", {"start": v(-28.18, -103.48) * mm, "end": v(-28.47, -104.75) * mm});
            skArc(sketch, "E66.3.133.0", {"start": v(-29.37, -105.78) * mm, "mid": v(-28.79, -105.38) * mm, "end": v(-28.47, -104.75) * mm});
            skArc(sketch, "E66.7.133.0", {"start": v(-29.61, -104.43) * mm, "mid": v(-29.66, -105.14) * mm, "end": v(-29.37, -105.78) * mm});
            skLineSegment(sketch, "E66.11.133.0", {"start": v(-29.2, -103.2) * mm, "end": v(-29.61, -104.43) * mm});
            skLineSegment(sketch, "E66.1.134.0", {"start": v(-25.93, -104.07) * mm, "end": v(-26.2, -105.34) * mm});
            skArc(sketch, "E66.3.134.0", {"start": v(-27.07, -106.4) * mm, "mid": v(-26.5, -105.98) * mm, "end": v(-26.2, -105.34) * mm});
            skArc(sketch, "E66.7.134.0", {"start": v(-27.34, -105.05) * mm, "mid": v(-27.38, -105.76) * mm, "end": v(-27.07, -106.4) * mm});
            skLineSegment(sketch, "E66.11.134.0", {"start": v(-26.96, -103.8) * mm, "end": v(-27.34, -105.05) * mm});
            skLineSegment(sketch, "E66.1.135.0", {"start": v(-23.67, -104.6) * mm, "end": v(-23.9, -105.89) * mm});
            skArc(sketch, "E66.3.135.0", {"start": v(-24.76, -106.96) * mm, "mid": v(-24.2, -106.53) * mm, "end": v(-23.9, -105.89) * mm});
            skArc(sketch, "E66.7.135.0", {"start": v(-25.06, -105.62) * mm, "mid": v(-25.08, -106.33) * mm, "end": v(-24.76, -106.96) * mm});
            skLineSegment(sketch, "E66.11.135.0", {"start": v(-24.7, -104.36) * mm, "end": v(-25.06, -105.62) * mm});
            skLineSegment(sketch, "E66.1.136.0", {"start": v(-21.4, -105.1) * mm, "end": v(-21.6, -106.38) * mm});
            skArc(sketch, "E66.3.136.0", {"start": v(-22.44, -107.47) * mm, "mid": v(-21.88, -107.03) * mm, "end": v(-21.6, -106.38) * mm});
            skArc(sketch, "E66.7.136.0", {"start": v(-22.77, -106.14) * mm, "mid": v(-22.77, -106.84) * mm, "end": v(-22.44, -107.47) * mm});
            skLineSegment(sketch, "E66.11.136.0", {"start": v(-22.44, -104.88) * mm, "end": v(-22.77, -106.14) * mm});
            skLineSegment(sketch, "E66.1.137.0", {"start": v(-19.11, -105.53) * mm, "end": v(-19.3, -106.82) * mm});
            skArc(sketch, "E66.3.137.0", {"start": v(-20.1, -107.93) * mm, "mid": v(-19.56, -107.48) * mm, "end": v(-19.3, -106.82) * mm});
            skArc(sketch, "E66.7.137.0", {"start": v(-20.46, -106.6) * mm, "mid": v(-20.45, -107.31) * mm, "end": v(-20.1, -107.93) * mm});
            skLineSegment(sketch, "E66.11.137.0", {"start": v(-20.16, -105.34) * mm, "end": v(-20.46, -106.6) * mm});
            skLineSegment(sketch, "E66.1.138.0", {"start": v(-16.82, -105.92) * mm, "end": v(-16.98, -107.22) * mm});
            skArc(sketch, "E66.3.138.0", {"start": v(-17.76, -108.34) * mm, "mid": v(-17.23, -107.88) * mm, "end": v(-16.98, -107.22) * mm});
            skArc(sketch, "E66.7.138.0", {"start": v(-18.15, -107.02) * mm, "mid": v(-18.12, -107.73) * mm, "end": v(-17.76, -108.34) * mm});
            skLineSegment(sketch, "E66.11.138.0", {"start": v(-17.88, -105.75) * mm, "end": v(-18.15, -107.02) * mm});
            skLineSegment(sketch, "E66.1.139.0", {"start": v(-14.53, -106.26) * mm, "end": v(-14.65, -107.56) * mm});
            skArc(sketch, "E66.3.139.0", {"start": v(-15.4, -108.7) * mm, "mid": v(-14.89, -108.22) * mm, "end": v(-14.65, -107.56) * mm});
            skArc(sketch, "E66.7.139.0", {"start": v(-15.82, -107.4) * mm, "mid": v(-15.78, -108.1) * mm, "end": v(-15.4, -108.7) * mm});
            skLineSegment(sketch, "E66.11.139.0", {"start": v(-15.58, -106.11) * mm, "end": v(-15.82, -107.4) * mm});
            skLineSegment(sketch, "E66.1.140.0", {"start": v(-12.22, -106.55) * mm, "end": v(-12.32, -107.85) * mm});
            skArc(sketch, "E66.3.140.0", {"start": v(-13.05, -109) * mm, "mid": v(-12.54, -108.52) * mm, "end": v(-12.32, -107.85) * mm});
            skArc(sketch, "E66.7.140.0", {"start": v(-13.5, -107.7) * mm, "mid": v(-13.44, -108.41) * mm, "end": v(-13.05, -109) * mm});
            skLineSegment(sketch, "E66.11.140.0", {"start": v(-13.28, -106.42) * mm, "end": v(-13.5, -107.7) * mm});
            skLineSegment(sketch, "E66.1.141.0", {"start": v(-9.9, -106.8) * mm, "end": v(-9.98, -108.1) * mm});
            skArc(sketch, "E66.3.141.0", {"start": v(-10.69, -109.26) * mm, "mid": v(-10.18, -108.77) * mm, "end": v(-9.98, -108.1) * mm});
            skArc(sketch, "E66.7.141.0", {"start": v(-11.16, -107.98) * mm, "mid": v(-11.08, -108.68) * mm, "end": v(-10.69, -109.26) * mm});
            skLineSegment(sketch, "E66.11.141.0", {"start": v(-10.97, -106.69) * mm, "end": v(-11.16, -107.98) * mm});
            skLineSegment(sketch, "E66.1.142.0", {"start": v(-7.6, -106.98) * mm, "end": v(-7.63, -108.28) * mm});
            skArc(sketch, "E66.3.142.0", {"start": v(-8.32, -109.47) * mm, "mid": v(-7.83, -108.96) * mm, "end": v(-7.63, -108.28) * mm});
            skArc(sketch, "E66.7.142.0", {"start": v(-8.82, -108.2) * mm, "mid": v(-8.73, -108.9) * mm, "end": v(-8.32, -109.47) * mm});
            skLineSegment(sketch, "E66.11.142.0", {"start": v(-8.66, -106.9) * mm, "end": v(-8.82, -108.2) * mm});
            skLineSegment(sketch, "E66.1.143.0", {"start": v(-5.27, -107.12) * mm, "end": v(-5.28, -108.42) * mm});
            skArc(sketch, "E66.3.143.0", {"start": v(-5.94, -109.62) * mm, "mid": v(-5.46, -109.1) * mm, "end": v(-5.28, -108.42) * mm});
            skArc(sketch, "E66.7.143.0", {"start": v(-6.47, -108.36) * mm, "mid": v(-6.37, -109.06) * mm, "end": v(-5.94, -109.62) * mm});
            skLineSegment(sketch, "E66.11.143.0", {"start": v(-6.34, -107.06) * mm, "end": v(-6.47, -108.36) * mm});
            skLineSegment(sketch, "E66.1.144.0", {"start": v(-2.95, -107.2) * mm, "end": v(-2.93, -108.51) * mm});
            skArc(sketch, "E66.3.144.0", {"start": v(-3.57, -109.73) * mm, "mid": v(-3.1, -109.2) * mm, "end": v(-2.93, -108.51) * mm});
            skArc(sketch, "E66.7.144.0", {"start": v(-4.12, -108.47) * mm, "mid": v(-4, -109.17) * mm, "end": v(-3.57, -109.73) * mm});
            skLineSegment(sketch, "E66.11.144.0", {"start": v(-4.02, -107.17) * mm, "end": v(-4.12, -108.47) * mm});
            skLineSegment(sketch, "E66.1.145.0", {"start": v(-0.63, -107.25) * mm, "end": v(-0.58, -108.55) * mm});
            skArc(sketch, "E66.3.145.0", {"start": v(-1.19, -109.78) * mm, "mid": v(-0.73, -109.24) * mm, "end": v(-0.58, -108.55) * mm});
            skArc(sketch, "E66.7.145.0", {"start": v(-1.77, -108.54) * mm, "mid": v(-1.64, -109.23) * mm, "end": v(-1.19, -109.78) * mm});
            skLineSegment(sketch, "E66.11.145.0", {"start": v(-1.7, -107.24) * mm, "end": v(-1.77, -108.54) * mm});
            skLineSegment(sketch, "E66.1.146.0", {"start": v(1.7, -107.24) * mm, "end": v(1.77, -108.54) * mm});
            skArc(sketch, "E66.3.146.0", {"start": v(1.19, -109.78) * mm, "mid": v(1.64, -109.23) * mm, "end": v(1.77, -108.54) * mm});
            skArc(sketch, "E66.7.146.0", {"start": v(0.58, -108.55) * mm, "mid": v(0.73, -109.24) * mm, "end": v(1.19, -109.78) * mm});
            skLineSegment(sketch, "E66.11.146.0", {"start": v(0.63, -107.25) * mm, "end": v(0.58, -108.55) * mm});
            skLineSegment(sketch, "E66.1.147.0", {"start": v(4.02, -107.17) * mm, "end": v(4.12, -108.47) * mm});
            skArc(sketch, "E66.3.147.0", {"start": v(3.57, -109.73) * mm, "mid": v(4, -109.17) * mm, "end": v(4.12, -108.47) * mm});
            skArc(sketch, "E66.7.147.0", {"start": v(2.93, -108.51) * mm, "mid": v(3.1, -109.2) * mm, "end": v(3.57, -109.73) * mm});
            skLineSegment(sketch, "E66.11.147.0", {"start": v(2.95, -107.2) * mm, "end": v(2.93, -108.51) * mm});
            skLineSegment(sketch, "E66.1.148.0", {"start": v(6.34, -107.06) * mm, "end": v(6.47, -108.36) * mm});
            skArc(sketch, "E66.3.148.0", {"start": v(5.94, -109.62) * mm, "mid": v(6.37, -109.06) * mm, "end": v(6.47, -108.36) * mm});
            skArc(sketch, "E66.7.148.0", {"start": v(5.28, -108.42) * mm, "mid": v(5.46, -109.1) * mm, "end": v(5.94, -109.62) * mm});
            skLineSegment(sketch, "E66.11.148.0", {"start": v(5.27, -107.12) * mm, "end": v(5.28, -108.42) * mm});
            skLineSegment(sketch, "E66.1.149.0", {"start": v(8.66, -106.9) * mm, "end": v(8.82, -108.2) * mm});
            skArc(sketch, "E66.3.149.0", {"start": v(8.32, -109.47) * mm, "mid": v(8.73, -108.9) * mm, "end": v(8.82, -108.2) * mm});
            skArc(sketch, "E66.7.149.0", {"start": v(7.63, -108.28) * mm, "mid": v(7.83, -108.96) * mm, "end": v(8.32, -109.47) * mm});
            skLineSegment(sketch, "E66.11.149.0", {"start": v(7.6, -106.98) * mm, "end": v(7.63, -108.28) * mm});
            skLineSegment(sketch, "E66.1.150.0", {"start": v(10.97, -106.69) * mm, "end": v(11.16, -107.98) * mm});
            skArc(sketch, "E66.3.150.0", {"start": v(10.69, -109.26) * mm, "mid": v(11.08, -108.68) * mm, "end": v(11.16, -107.98) * mm});
            skArc(sketch, "E66.7.150.0", {"start": v(9.98, -108.1) * mm, "mid": v(10.18, -108.77) * mm, "end": v(10.69, -109.26) * mm});
            skLineSegment(sketch, "E66.11.150.0", {"start": v(9.9, -106.8) * mm, "end": v(9.98, -108.1) * mm});
            skLineSegment(sketch, "E66.1.151.0", {"start": v(13.28, -106.42) * mm, "end": v(13.5, -107.7) * mm});
            skArc(sketch, "E66.3.151.0", {"start": v(13.05, -109) * mm, "mid": v(13.44, -108.41) * mm, "end": v(13.5, -107.7) * mm});
            skArc(sketch, "E66.7.151.0", {"start": v(12.32, -107.85) * mm, "mid": v(12.54, -108.52) * mm, "end": v(13.05, -109) * mm});
            skLineSegment(sketch, "E66.11.151.0", {"start": v(12.22, -106.55) * mm, "end": v(12.32, -107.85) * mm});
            skLineSegment(sketch, "E66.1.152.0", {"start": v(15.58, -106.11) * mm, "end": v(15.82, -107.4) * mm});
            skArc(sketch, "E66.3.152.0", {"start": v(15.4, -108.7) * mm, "mid": v(15.78, -108.1) * mm, "end": v(15.82, -107.4) * mm});
            skArc(sketch, "E66.7.152.0", {"start": v(14.65, -107.56) * mm, "mid": v(14.89, -108.22) * mm, "end": v(15.4, -108.7) * mm});
            skLineSegment(sketch, "E66.11.152.0", {"start": v(14.53, -106.26) * mm, "end": v(14.65, -107.56) * mm});
            skLineSegment(sketch, "E66.1.153.0", {"start": v(17.88, -105.75) * mm, "end": v(18.15, -107.02) * mm});
            skArc(sketch, "E66.3.153.0", {"start": v(17.76, -108.34) * mm, "mid": v(18.12, -107.73) * mm, "end": v(18.15, -107.02) * mm});
            skArc(sketch, "E66.7.153.0", {"start": v(16.98, -107.22) * mm, "mid": v(17.23, -107.88) * mm, "end": v(17.76, -108.34) * mm});
            skLineSegment(sketch, "E66.11.153.0", {"start": v(16.82, -105.92) * mm, "end": v(16.98, -107.22) * mm});
            skLineSegment(sketch, "E66.1.154.0", {"start": v(20.16, -105.34) * mm, "end": v(20.46, -106.6) * mm});
            skArc(sketch, "E66.3.154.0", {"start": v(20.1, -107.93) * mm, "mid": v(20.45, -107.31) * mm, "end": v(20.46, -106.6) * mm});
            skArc(sketch, "E66.7.154.0", {"start": v(19.3, -106.82) * mm, "mid": v(19.56, -107.48) * mm, "end": v(20.1, -107.93) * mm});
            skLineSegment(sketch, "E66.11.154.0", {"start": v(19.11, -105.53) * mm, "end": v(19.3, -106.82) * mm});
            skLineSegment(sketch, "E66.1.155.0", {"start": v(22.44, -104.88) * mm, "end": v(22.77, -106.14) * mm});
            skArc(sketch, "E66.3.155.0", {"start": v(22.44, -107.47) * mm, "mid": v(22.77, -106.84) * mm, "end": v(22.77, -106.14) * mm});
            skArc(sketch, "E66.7.155.0", {"start": v(21.6, -106.38) * mm, "mid": v(21.88, -107.03) * mm, "end": v(22.44, -107.47) * mm});
            skLineSegment(sketch, "E66.11.155.0", {"start": v(21.4, -105.1) * mm, "end": v(21.6, -106.38) * mm});
            skLineSegment(sketch, "E66.1.156.0", {"start": v(24.7, -104.36) * mm, "end": v(25.06, -105.62) * mm});
            skArc(sketch, "E66.3.156.0", {"start": v(24.76, -106.96) * mm, "mid": v(25.08, -106.33) * mm, "end": v(25.06, -105.62) * mm});
            skArc(sketch, "E66.7.156.0", {"start": v(23.9, -105.89) * mm, "mid": v(24.2, -106.53) * mm, "end": v(24.76, -106.96) * mm});
            skLineSegment(sketch, "E66.11.156.0", {"start": v(23.67, -104.6) * mm, "end": v(23.9, -105.89) * mm});
            skLineSegment(sketch, "E66.1.157.0", {"start": v(26.96, -103.8) * mm, "end": v(27.34, -105.05) * mm});
            skArc(sketch, "E66.3.157.0", {"start": v(27.07, -106.4) * mm, "mid": v(27.38, -105.76) * mm, "end": v(27.34, -105.05) * mm});
            skArc(sketch, "E66.7.157.0", {"start": v(26.2, -105.34) * mm, "mid": v(26.5, -105.98) * mm, "end": v(27.07, -106.4) * mm});
            skLineSegment(sketch, "E66.11.157.0", {"start": v(25.93, -104.07) * mm, "end": v(26.2, -105.34) * mm});
            skLineSegment(sketch, "E66.1.158.0", {"start": v(29.2, -103.2) * mm, "end": v(29.61, -104.43) * mm});
            skArc(sketch, "E66.3.158.0", {"start": v(29.37, -105.78) * mm, "mid": v(29.66, -105.14) * mm, "end": v(29.61, -104.43) * mm});
            skArc(sketch, "E66.7.158.0", {"start": v(28.47, -104.75) * mm, "mid": v(28.79, -105.38) * mm, "end": v(29.37, -105.78) * mm});
            skLineSegment(sketch, "E66.11.158.0", {"start": v(28.18, -103.48) * mm, "end": v(28.47, -104.75) * mm});
            skLineSegment(sketch, "E66.1.159.0", {"start": v(31.44, -102.54) * mm, "end": v(31.87, -103.77) * mm});
            skArc(sketch, "E66.3.159.0", {"start": v(31.66, -105.12) * mm, "mid": v(31.93, -104.47) * mm, "end": v(31.87, -103.77) * mm});
            skArc(sketch, "E66.7.159.0", {"start": v(30.73, -104.1) * mm, "mid": v(31.07, -104.73) * mm, "end": v(31.66, -105.12) * mm});
            skLineSegment(sketch, "E66.11.159.0", {"start": v(30.41, -102.85) * mm, "end": v(30.73, -104.1) * mm});
            skLineSegment(sketch, "E66.1.160.0", {"start": v(33.65, -101.83) * mm, "end": v(34.1, -103.05) * mm});
            skArc(sketch, "E66.3.160.0", {"start": v(33.93, -104.41) * mm, "mid": v(34.19, -103.76) * mm, "end": v(34.1, -103.05) * mm});
            skArc(sketch, "E66.7.160.0", {"start": v(32.98, -103.42) * mm, "mid": v(33.33, -104.03) * mm, "end": v(33.93, -104.41) * mm});
            skLineSegment(sketch, "E66.11.160.0", {"start": v(32.63, -102.16) * mm, "end": v(32.98, -103.42) * mm});
            skLineSegment(sketch, "E66.1.161.0", {"start": v(35.85, -101.08) * mm, "end": v(36.33, -102.29) * mm});
            skArc(sketch, "E66.3.161.0", {"start": v(36.18, -103.65) * mm, "mid": v(36.43, -103) * mm, "end": v(36.33, -102.29) * mm});
            skArc(sketch, "E66.7.161.0", {"start": v(35.21, -102.68) * mm, "mid": v(35.57, -103.29) * mm, "end": v(36.18, -103.65) * mm});
            skLineSegment(sketch, "E66.11.161.0", {"start": v(34.84, -101.43) * mm, "end": v(35.21, -102.68) * mm});
            skLineSegment(sketch, "E66.1.162.0", {"start": v(38.03, -100.28) * mm, "end": v(38.54, -101.48) * mm});
            skArc(sketch, "E66.3.162.0", {"start": v(38.42, -102.84) * mm, "mid": v(38.65, -102.18) * mm, "end": v(38.54, -101.48) * mm});
            skArc(sketch, "E66.7.162.0", {"start": v(37.43, -101.9) * mm, "mid": v(37.8, -102.5) * mm, "end": v(38.42, -102.84) * mm});
            skLineSegment(sketch, "E66.11.162.0", {"start": v(37.03, -100.65) * mm, "end": v(37.43, -101.9) * mm});
            skLineSegment(sketch, "E66.1.163.0", {"start": v(40.2, -99.43) * mm, "end": v(40.73, -100.62) * mm});
            skArc(sketch, "E66.3.163.0", {"start": v(40.64, -101.99) * mm, "mid": v(40.85, -101.32) * mm, "end": v(40.73, -100.62) * mm});
            skArc(sketch, "E66.7.163.0", {"start": v(39.63, -101.06) * mm, "mid": v(40.01, -101.65) * mm, "end": v(40.64, -101.99) * mm});
            skLineSegment(sketch, "E66.11.163.0", {"start": v(39.2, -99.83) * mm, "end": v(39.63, -101.06) * mm});
            skLineSegment(sketch, "E66.1.164.0", {"start": v(42.34, -98.54) * mm, "end": v(42.9, -99.71) * mm});
            skArc(sketch, "E66.3.164.0", {"start": v(42.84, -101.08) * mm, "mid": v(43.04, -100.4) * mm, "end": v(42.9, -99.71) * mm});
            skArc(sketch, "E66.7.164.0", {"start": v(41.8, -100.18) * mm, "mid": v(42.2, -100.76) * mm, "end": v(42.84, -101.08) * mm});
            skLineSegment(sketch, "E66.11.164.0", {"start": v(41.35, -98.96) * mm, "end": v(41.8, -100.18) * mm});
            skLineSegment(sketch, "E66.1.165.0", {"start": v(44.46, -97.6) * mm, "end": v(45.05, -98.76) * mm});
            skArc(sketch, "E66.3.165.0", {"start": v(45.02, -100.13) * mm, "mid": v(45.2, -99.45) * mm, "end": v(45.05, -98.76) * mm});
            skArc(sketch, "E66.7.165.0", {"start": v(43.97, -99.25) * mm, "mid": v(44.38, -99.82) * mm, "end": v(45.02, -100.13) * mm});
            skLineSegment(sketch, "E66.11.165.0", {"start": v(43.49, -98.04) * mm, "end": v(43.97, -99.25) * mm});
            skLineSegment(sketch, "E66.1.166.0", {"start": v(46.57, -96.61) * mm, "end": v(47.18, -97.76) * mm});
            skArc(sketch, "E66.3.166.0", {"start": v(47.17, -99.13) * mm, "mid": v(47.35, -98.45) * mm, "end": v(47.18, -97.76) * mm});
            skArc(sketch, "E66.7.166.0", {"start": v(46.1, -98.27) * mm, "mid": v(46.53, -98.84) * mm, "end": v(47.17, -99.13) * mm});
            skLineSegment(sketch, "E66.11.166.0", {"start": v(45.6, -97.07) * mm, "end": v(46.1, -98.27) * mm});
            skLineSegment(sketch, "E66.1.167.0", {"start": v(48.65, -95.58) * mm, "end": v(49.29, -96.72) * mm});
            skArc(sketch, "E66.3.167.0", {"start": v(49.31, -98.09) * mm, "mid": v(49.47, -97.4) * mm, "end": v(49.29, -96.72) * mm});
            skArc(sketch, "E66.7.167.0", {"start": v(48.23, -97.25) * mm, "mid": v(48.66, -97.8) * mm, "end": v(49.31, -98.09) * mm});
            skLineSegment(sketch, "E66.11.167.0", {"start": v(47.7, -96.06) * mm, "end": v(48.23, -97.25) * mm});
            skLineSegment(sketch, "E66.1.168.0", {"start": v(50.7, -94.5) * mm, "end": v(51.37, -95.63) * mm});
            skArc(sketch, "E66.3.168.0", {"start": v(51.42, -97) * mm, "mid": v(51.57, -96.3) * mm, "end": v(51.37, -95.63) * mm});
            skArc(sketch, "E66.7.168.0", {"start": v(50.32, -96.18) * mm, "mid": v(50.77, -96.73) * mm, "end": v(51.42, -97) * mm});
            skLineSegment(sketch, "E66.11.168.0", {"start": v(49.76, -95) * mm, "end": v(50.32, -96.18) * mm});
            skLineSegment(sketch, "E66.1.169.0", {"start": v(52.74, -93.38) * mm, "end": v(53.43, -94.5) * mm});
            skArc(sketch, "E66.3.169.0", {"start": v(53.51, -95.86) * mm, "mid": v(53.64, -95.16) * mm, "end": v(53.43, -94.5) * mm});
            skArc(sketch, "E66.7.169.0", {"start": v(52.4, -95.07) * mm, "mid": v(52.85, -95.6) * mm, "end": v(53.51, -95.86) * mm});
            skLineSegment(sketch, "E66.11.169.0", {"start": v(51.81, -93.9) * mm, "end": v(52.4, -95.07) * mm});
            skLineSegment(sketch, "E66.1.170.0", {"start": v(54.75, -92.22) * mm, "end": v(55.46, -93.31) * mm});
            skArc(sketch, "E66.3.170.0", {"start": v(55.58, -94.68) * mm, "mid": v(55.7, -93.98) * mm, "end": v(55.46, -93.31) * mm});
            skArc(sketch, "E66.7.170.0", {"start": v(54.44, -93.91) * mm, "mid": v(54.91, -94.44) * mm, "end": v(55.58, -94.68) * mm});
            skLineSegment(sketch, "E66.11.170.0", {"start": v(53.83, -92.76) * mm, "end": v(54.44, -93.91) * mm});
            skLineSegment(sketch, "E66.1.171.0", {"start": v(56.74, -91.01) * mm, "end": v(57.47, -92.09) * mm});
            skArc(sketch, "E66.3.171.0", {"start": v(57.62, -93.45) * mm, "mid": v(57.72, -92.75) * mm, "end": v(57.47, -92.09) * mm});
            skArc(sketch, "E66.7.171.0", {"start": v(56.46, -92.71) * mm, "mid": v(56.95, -93.23) * mm, "end": v(57.62, -93.45) * mm});
            skLineSegment(sketch, "E66.11.171.0", {"start": v(55.83, -91.57) * mm, "end": v(56.46, -92.71) * mm});
            skLineSegment(sketch, "E66.1.172.0", {"start": v(58.7, -89.76) * mm, "end": v(59.45, -90.82) * mm});
            skArc(sketch, "E66.3.172.0", {"start": v(59.63, -92.18) * mm, "mid": v(59.71, -91.48) * mm, "end": v(59.45, -90.82) * mm});
            skArc(sketch, "E66.7.172.0", {"start": v(58.46, -91.47) * mm, "mid": v(58.95, -91.97) * mm, "end": v(59.63, -92.18) * mm});
            skLineSegment(sketch, "E66.11.172.0", {"start": v(57.8, -90.34) * mm, "end": v(58.46, -91.47) * mm});
            skLineSegment(sketch, "E66.1.173.0", {"start": v(60.63, -88.47) * mm, "end": v(61.4, -89.51) * mm});
            skArc(sketch, "E66.3.173.0", {"start": v(61.6, -90.87) * mm, "mid": v(61.68, -90.16) * mm, "end": v(61.4, -89.51) * mm});
            skArc(sketch, "E66.7.173.0", {"start": v(60.43, -90.18) * mm, "mid": v(60.93, -90.67) * mm, "end": v(61.6, -90.87) * mm});
            skLineSegment(sketch, "E66.11.173.0", {"start": v(59.74, -89.07) * mm, "end": v(60.43, -90.18) * mm});
            skLineSegment(sketch, "E66.1.174.0", {"start": v(62.53, -87.13) * mm, "end": v(63.33, -88.16) * mm});
            skArc(sketch, "E66.3.174.0", {"start": v(63.56, -89.51) * mm, "mid": v(63.62, -88.8) * mm, "end": v(63.33, -88.16) * mm});
            skArc(sketch, "E66.7.174.0", {"start": v(62.36, -88.85) * mm, "mid": v(62.88, -89.33) * mm, "end": v(63.56, -89.51) * mm});
            skLineSegment(sketch, "E66.11.174.0", {"start": v(61.66, -87.75) * mm, "end": v(62.36, -88.85) * mm});
            skLineSegment(sketch, "E66.1.175.0", {"start": v(64.4, -85.76) * mm, "end": v(65.23, -86.77) * mm});
            skArc(sketch, "E66.3.175.0", {"start": v(65.49, -88.11) * mm, "mid": v(65.53, -87.4) * mm, "end": v(65.23, -86.77) * mm});
            skArc(sketch, "E66.7.175.0", {"start": v(64.27, -87.48) * mm, "mid": v(64.8, -87.95) * mm, "end": v(65.49, -88.11) * mm});
            skLineSegment(sketch, "E66.11.175.0", {"start": v(63.55, -86.4) * mm, "end": v(64.27, -87.48) * mm});
            skLineSegment(sketch, "E66.1.176.0", {"start": v(66.25, -84.34) * mm, "end": v(67.1, -85.33) * mm});
            skArc(sketch, "E66.3.176.0", {"start": v(67.38, -86.67) * mm, "mid": v(67.4, -85.97) * mm, "end": v(67.1, -85.33) * mm});
            skArc(sketch, "E66.7.176.0", {"start": v(66.15, -86.06) * mm, "mid": v(66.7, -86.52) * mm, "end": v(67.38, -86.67) * mm});
            skLineSegment(sketch, "E66.11.176.0", {"start": v(65.4, -85) * mm, "end": v(66.15, -86.06) * mm});
            skLineSegment(sketch, "E66.1.177.0", {"start": v(68.06, -82.89) * mm, "end": v(68.92, -83.86) * mm});
            skArc(sketch, "E66.3.177.0", {"start": v(69.24, -85.2) * mm, "mid": v(69.25, -84.49) * mm, "end": v(68.92, -83.86) * mm});
            skArc(sketch, "E66.7.177.0", {"start": v(68, -84.6) * mm, "mid": v(68.55, -85.06) * mm, "end": v(69.24, -85.2) * mm});
            skLineSegment(sketch, "E66.11.177.0", {"start": v(67.23, -83.56) * mm, "end": v(68, -84.6) * mm});
            skLineSegment(sketch, "E66.1.178.0", {"start": v(69.84, -81.4) * mm, "end": v(70.73, -82.35) * mm});
            skArc(sketch, "E66.3.178.0", {"start": v(71.07, -83.67) * mm, "mid": v(71.07, -82.97) * mm, "end": v(70.73, -82.35) * mm});
            skArc(sketch, "E66.7.178.0", {"start": v(69.82, -83.12) * mm, "mid": v(70.38, -83.55) * mm, "end": v(71.07, -83.67) * mm});
            skLineSegment(sketch, "E66.11.178.0", {"start": v(69.02, -82.09) * mm, "end": v(69.82, -83.12) * mm});
            skLineSegment(sketch, "E66.1.179.0", {"start": v(71.59, -79.86) * mm, "end": v(72.5, -80.8) * mm});
            skArc(sketch, "E66.3.179.0", {"start": v(72.87, -82.11) * mm, "mid": v(72.85, -81.4) * mm, "end": v(72.5, -80.8) * mm});
            skArc(sketch, "E66.7.179.0", {"start": v(71.6, -81.58) * mm, "mid": v(72.17, -82) * mm, "end": v(72.87, -82.11) * mm});
            skLineSegment(sketch, "E66.11.179.0", {"start": v(70.79, -80.57) * mm, "end": v(71.6, -81.58) * mm});
            skLineSegment(sketch, "E66.1.180.0", {"start": v(73.3, -78.3) * mm, "end": v(74.23, -79.2) * mm});
            skArc(sketch, "E66.3.180.0", {"start": v(74.63, -80.52) * mm, "mid": v(74.6, -79.81) * mm, "end": v(74.23, -79.2) * mm});
            skArc(sketch, "E66.7.180.0", {"start": v(73.36, -80.01) * mm, "mid": v(73.93, -80.43) * mm, "end": v(74.63, -80.52) * mm});
            skLineSegment(sketch, "E66.11.180.0", {"start": v(72.52, -79.02) * mm, "end": v(73.36, -80.01) * mm});
            skLineSegment(sketch, "E66.1.181.0", {"start": v(74.98, -76.69) * mm, "end": v(75.92, -77.58) * mm});
            skArc(sketch, "E66.3.181.0", {"start": v(76.36, -78.88) * mm, "mid": v(76.3, -78.18) * mm, "end": v(75.92, -77.58) * mm});
            skArc(sketch, "E66.7.181.0", {"start": v(75.07, -78.4) * mm, "mid": v(75.66, -78.8) * mm, "end": v(76.36, -78.88) * mm});
            skLineSegment(sketch, "E66.11.181.0", {"start": v(74.21, -77.43) * mm, "end": v(75.07, -78.4) * mm});
            skLineSegment(sketch, "E66.1.182.0", {"start": v(76.62, -75.04) * mm, "end": v(77.59, -75.92) * mm});
            skArc(sketch, "E66.3.182.0", {"start": v(78.05, -77.2) * mm, "mid": v(77.98, -76.5) * mm, "end": v(77.59, -75.92) * mm});
            skArc(sketch, "E66.7.182.0", {"start": v(76.75, -76.76) * mm, "mid": v(77.34, -77.15) * mm, "end": v(78.05, -77.2) * mm});
            skLineSegment(sketch, "E66.11.182.0", {"start": v(75.87, -75.8) * mm, "end": v(76.75, -76.76) * mm});
            skLineSegment(sketch, "E66.1.183.0", {"start": v(78.23, -73.37) * mm, "end": v(79.21, -74.22) * mm});
            skArc(sketch, "E66.3.183.0", {"start": v(79.7, -75.5) * mm, "mid": v(79.62, -74.8) * mm, "end": v(79.21, -74.22) * mm});
            skArc(sketch, "E66.7.183.0", {"start": v(78.4, -75.08) * mm, "mid": v(79, -75.45) * mm, "end": v(79.7, -75.5) * mm});
            skLineSegment(sketch, "E66.11.183.0", {"start": v(77.5, -74.14) * mm, "end": v(78.4, -75.08) * mm});
            skLineSegment(sketch, "E66.1.184.0", {"start": v(79.8, -71.66) * mm, "end": v(80.8, -72.48) * mm});
            skArc(sketch, "E66.3.184.0", {"start": v(81.32, -73.75) * mm, "mid": v(81.22, -73.05) * mm, "end": v(80.8, -72.48) * mm});
            skArc(sketch, "E66.7.184.0", {"start": v(80, -73.36) * mm, "mid": v(80.61, -73.72) * mm, "end": v(81.32, -73.75) * mm});
            skLineSegment(sketch, "E66.11.184.0", {"start": v(79.08, -72.45) * mm, "end": v(80, -73.36) * mm});
            skLineSegment(sketch, "E66.1.185.0", {"start": v(81.33, -69.9) * mm, "end": v(82.35, -70.72) * mm});
            skArc(sketch, "E66.3.185.0", {"start": v(82.9, -71.98) * mm, "mid": v(82.79, -71.28) * mm, "end": v(82.35, -70.72) * mm});
            skArc(sketch, "E66.7.185.0", {"start": v(81.58, -71.61) * mm, "mid": v(82.2, -71.96) * mm, "end": v(82.9, -71.98) * mm});
            skLineSegment(sketch, "E66.11.185.0", {"start": v(80.63, -70.72) * mm, "end": v(81.58, -71.61) * mm});
            skLineSegment(sketch, "E66.1.186.0", {"start": v(82.83, -68.13) * mm, "end": v(83.87, -68.92) * mm});
            skArc(sketch, "E66.3.186.0", {"start": v(84.44, -70.16) * mm, "mid": v(84.31, -69.47) * mm, "end": v(83.87, -68.92) * mm});
            skArc(sketch, "E66.7.186.0", {"start": v(83.1, -69.83) * mm, "mid": v(83.73, -70.16) * mm, "end": v(84.44, -70.16) * mm});
            skLineSegment(sketch, "E66.11.186.0", {"start": v(82.15, -68.95) * mm, "end": v(83.1, -69.83) * mm});
            skLineSegment(sketch, "E66.1.187.0", {"start": v(84.29, -66.32) * mm, "end": v(85.34, -67.08) * mm});
            skArc(sketch, "E66.3.187.0", {"start": v(85.94, -68.32) * mm, "mid": v(85.8, -67.62) * mm, "end": v(85.34, -67.08) * mm});
            skArc(sketch, "E66.7.187.0", {"start": v(84.6, -68.01) * mm, "mid": v(85.23, -68.33) * mm, "end": v(85.94, -68.32) * mm});
            skLineSegment(sketch, "E66.11.187.0", {"start": v(83.62, -67.16) * mm, "end": v(84.6, -68.01) * mm});
            skLineSegment(sketch, "E66.1.188.0", {"start": v(85.7, -64.48) * mm, "end": v(86.77, -65.22) * mm});
            skArc(sketch, "E66.3.188.0", {"start": v(87.4, -66.44) * mm, "mid": v(87.24, -65.75) * mm, "end": v(86.77, -65.22) * mm});
            skArc(sketch, "E66.7.188.0", {"start": v(86.06, -66.16) * mm, "mid": v(86.7, -66.47) * mm, "end": v(87.4, -66.44) * mm});
            skLineSegment(sketch, "E66.11.188.0", {"start": v(85.06, -65.33) * mm, "end": v(86.06, -66.16) * mm});
            skLineSegment(sketch, "E66.1.189.0", {"start": v(87.08, -62.6) * mm, "end": v(88.17, -63.32) * mm});
            skArc(sketch, "E66.3.189.0", {"start": v(88.82, -64.53) * mm, "mid": v(88.64, -63.84) * mm, "end": v(88.17, -63.32) * mm});
            skArc(sketch, "E66.7.189.0", {"start": v(87.47, -64.28) * mm, "mid": v(88.11, -64.58) * mm, "end": v(88.82, -64.53) * mm});
            skLineSegment(sketch, "E66.11.189.0", {"start": v(86.45, -63.47) * mm, "end": v(87.47, -64.28) * mm});
            skLineSegment(sketch, "E66.1.190.0", {"start": v(88.42, -60.7) * mm, "end": v(89.52, -61.4) * mm});
            skArc(sketch, "E66.3.190.0", {"start": v(90.2, -62.6) * mm, "mid": v(90, -61.9) * mm, "end": v(89.52, -61.4) * mm});
            skArc(sketch, "E66.7.190.0", {"start": v(88.84, -62.37) * mm, "mid": v(89.5, -62.65) * mm, "end": v(90.2, -62.6) * mm});
            skLineSegment(sketch, "E66.11.190.0", {"start": v(87.8, -61.58) * mm, "end": v(88.84, -62.37) * mm});
            skLineSegment(sketch, "E66.1.191.0", {"start": v(89.71, -58.78) * mm, "end": v(90.83, -59.44) * mm});
            skArc(sketch, "E66.3.191.0", {"start": v(91.53, -60.62) * mm, "mid": v(91.33, -59.94) * mm, "end": v(90.83, -59.44) * mm});
            skArc(sketch, "E66.7.191.0", {"start": v(90.17, -60.43) * mm, "mid": v(90.83, -60.7) * mm, "end": v(91.53, -60.62) * mm});
            skLineSegment(sketch, "E66.11.191.0", {"start": v(89.12, -59.67) * mm, "end": v(90.17, -60.43) * mm});
            skLineSegment(sketch, "E66.1.192.0", {"start": v(90.96, -56.82) * mm, "end": v(92.1, -57.46) * mm});
            skArc(sketch, "E66.3.192.0", {"start": v(92.82, -58.62) * mm, "mid": v(92.6, -57.95) * mm, "end": v(92.1, -57.46) * mm});
            skArc(sketch, "E66.7.192.0", {"start": v(91.46, -58.47) * mm, "mid": v(92.12, -58.72) * mm, "end": v(92.82, -58.62) * mm});
            skLineSegment(sketch, "E66.11.192.0", {"start": v(90.4, -57.72) * mm, "end": v(91.46, -58.47) * mm});
            skLineSegment(sketch, "E66.1.193.0", {"start": v(92.17, -54.84) * mm, "end": v(93.32, -55.45) * mm});
            skArc(sketch, "E66.3.193.0", {"start": v(94.07, -56.6) * mm, "mid": v(93.84, -55.93) * mm, "end": v(93.32, -55.45) * mm});
            skArc(sketch, "E66.7.193.0", {"start": v(92.7, -56.47) * mm, "mid": v(93.37, -56.7) * mm, "end": v(94.07, -56.6) * mm});
            skLineSegment(sketch, "E66.11.193.0", {"start": v(91.62, -55.75) * mm, "end": v(92.7, -56.47) * mm});
            skLineSegment(sketch, "E66.1.194.0", {"start": v(93.34, -52.83) * mm, "end": v(94.5, -53.42) * mm});
            skArc(sketch, "E66.3.194.0", {"start": v(95.27, -54.55) * mm, "mid": v(95.03, -53.89) * mm, "end": v(94.5, -53.42) * mm});
            skArc(sketch, "E66.7.194.0", {"start": v(93.9, -54.45) * mm, "mid": v(94.58, -54.67) * mm, "end": v(95.27, -54.55) * mm});
            skLineSegment(sketch, "E66.11.194.0", {"start": v(92.8, -53.75) * mm, "end": v(93.9, -54.45) * mm});
            skLineSegment(sketch, "E66.1.195.0", {"start": v(94.46, -50.8) * mm, "end": v(95.63, -51.36) * mm});
            skArc(sketch, "E66.3.195.0", {"start": v(96.43, -52.47) * mm, "mid": v(96.17, -51.82) * mm, "end": v(95.63, -51.36) * mm});
            skArc(sketch, "E66.7.195.0", {"start": v(95.06, -52.4) * mm, "mid": v(95.74, -52.6) * mm, "end": v(96.43, -52.47) * mm});
            skLineSegment(sketch, "E66.11.195.0", {"start": v(93.95, -51.73) * mm, "end": v(95.06, -52.4) * mm});
            skLineSegment(sketch, "E66.1.196.0", {"start": v(95.54, -48.73) * mm, "end": v(96.72, -49.28) * mm});
            skArc(sketch, "E66.3.196.0", {"start": v(97.55, -50.37) * mm, "mid": v(97.27, -49.72) * mm, "end": v(96.72, -49.28) * mm});
            skArc(sketch, "E66.7.196.0", {"start": v(96.18, -50.33) * mm, "mid": v(96.86, -50.52) * mm, "end": v(97.55, -50.37) * mm});
            skLineSegment(sketch, "E66.11.196.0", {"start": v(95.05, -49.68) * mm, "end": v(96.18, -50.33) * mm});
            skLineSegment(sketch, "E66.1.197.0", {"start": v(96.57, -46.65) * mm, "end": v(97.77, -47.17) * mm});
            skArc(sketch, "E66.3.197.0", {"start": v(98.62, -48.25) * mm, "mid": v(98.33, -47.6) * mm, "end": v(97.77, -47.17) * mm});
            skArc(sketch, "E66.7.197.0", {"start": v(97.25, -48.24) * mm, "mid": v(97.93, -48.41) * mm, "end": v(98.62, -48.25) * mm});
            skLineSegment(sketch, "E66.11.197.0", {"start": v(96.1, -47.61) * mm, "end": v(97.25, -48.24) * mm});
            skLineSegment(sketch, "E66.1.198.0", {"start": v(97.56, -44.55) * mm, "end": v(98.77, -45.04) * mm});
            skArc(sketch, "E66.3.198.0", {"start": v(99.64, -46.1) * mm, "mid": v(99.34, -45.46) * mm, "end": v(98.77, -45.04) * mm});
            skArc(sketch, "E66.7.198.0", {"start": v(98.27, -46.12) * mm, "mid": v(98.96, -46.28) * mm, "end": v(99.64, -46.1) * mm});
            skLineSegment(sketch, "E66.11.198.0", {"start": v(97.11, -45.52) * mm, "end": v(98.27, -46.12) * mm});
            skLineSegment(sketch, "E66.1.199.0", {"start": v(98.5, -42.42) * mm, "end": v(99.72, -42.89) * mm});
            skArc(sketch, "E66.3.199.0", {"start": v(100.61, -43.93) * mm, "mid": v(100.3, -43.3) * mm, "end": v(99.72, -42.89) * mm});
            skArc(sketch, "E66.7.199.0", {"start": v(99.24, -43.98) * mm, "mid": v(99.93, -44.13) * mm, "end": v(100.61, -43.93) * mm});
            skLineSegment(sketch, "E66.11.199.0", {"start": v(98.08, -43.4) * mm, "end": v(99.24, -43.98) * mm});
            skLineSegment(sketch, "E66.1.200.0", {"start": v(99.4, -40.28) * mm, "end": v(100.62, -40.72) * mm});
            skArc(sketch, "E66.3.200.0", {"start": v(101.54, -41.74) * mm, "mid": v(101.21, -41.11) * mm, "end": v(100.62, -40.72) * mm});
            skArc(sketch, "E66.7.200.0", {"start": v(100.17, -41.82) * mm, "mid": v(100.87, -41.95) * mm, "end": v(101.54, -41.74) * mm});
            skLineSegment(sketch, "E66.11.200.0", {"start": v(99, -41.27) * mm, "end": v(100.17, -41.82) * mm});
            skLineSegment(sketch, "E66.1.201.0", {"start": v(100.25, -38.12) * mm, "end": v(101.48, -38.53) * mm});
            skArc(sketch, "E66.3.201.0", {"start": v(102.42, -39.53) * mm, "mid": v(102.08, -38.91) * mm, "end": v(101.48, -38.53) * mm});
            skArc(sketch, "E66.7.201.0", {"start": v(101.06, -39.64) * mm, "mid": v(101.75, -39.75) * mm, "end": v(102.42, -39.53) * mm});
            skLineSegment(sketch, "E66.11.201.0", {"start": v(99.86, -39.11) * mm, "end": v(101.06, -39.64) * mm});
            skLineSegment(sketch, "E66.1.202.0", {"start": v(101.05, -35.94) * mm, "end": v(102.3, -36.32) * mm});
            skArc(sketch, "E66.3.202.0", {"start": v(103.25, -37.3) * mm, "mid": v(102.9, -36.7) * mm, "end": v(102.3, -36.32) * mm});
            skArc(sketch, "E66.7.202.0", {"start": v(101.9, -37.44) * mm, "mid": v(102.59, -37.54) * mm, "end": v(103.25, -37.3) * mm});
            skLineSegment(sketch, "E66.11.202.0", {"start": v(100.69, -36.94) * mm, "end": v(101.9, -37.44) * mm});
            skLineSegment(sketch, "E66.1.203.0", {"start": v(101.8, -33.74) * mm, "end": v(103.06, -34.1) * mm});
            skArc(sketch, "E66.3.203.0", {"start": v(104.04, -35.05) * mm, "mid": v(103.67, -34.45) * mm, "end": v(103.06, -34.1) * mm});
            skArc(sketch, "E66.7.203.0", {"start": v(102.68, -35.22) * mm, "mid": v(103.38, -35.3) * mm, "end": v(104.04, -35.05) * mm});
            skLineSegment(sketch, "E66.11.203.0", {"start": v(101.46, -34.75) * mm, "end": v(102.68, -35.22) * mm});
            skLineSegment(sketch, "E66.1.204.0", {"start": v(102.51, -31.53) * mm, "end": v(103.77, -31.86) * mm});
            skArc(sketch, "E66.3.204.0", {"start": v(104.77, -32.8) * mm, "mid": v(104.39, -32.2) * mm, "end": v(103.77, -31.86) * mm});
            skArc(sketch, "E66.7.204.0", {"start": v(103.42, -32.99) * mm, "mid": v(104.12, -33.06) * mm, "end": v(104.77, -32.8) * mm});
            skLineSegment(sketch, "E66.11.204.0", {"start": v(102.2, -32.54) * mm, "end": v(103.42, -32.99) * mm});
            skLineSegment(sketch, "E66.1.205.0", {"start": v(103.17, -29.3) * mm, "end": v(104.44, -29.6) * mm});
            skArc(sketch, "E66.3.205.0", {"start": v(105.46, -30.51) * mm, "mid": v(105.06, -29.93) * mm, "end": v(104.44, -29.6) * mm});
            skArc(sketch, "E66.7.205.0", {"start": v(104.1, -30.74) * mm, "mid": v(104.81, -30.8) * mm, "end": v(105.46, -30.51) * mm});
            skLineSegment(sketch, "E66.11.205.0", {"start": v(102.87, -30.32) * mm, "end": v(104.1, -30.74) * mm});
            skLineSegment(sketch, "E66.1.206.0", {"start": v(103.78, -27.06) * mm, "end": v(105.05, -27.33) * mm});
            skArc(sketch, "E66.3.206.0", {"start": v(106.1, -28.22) * mm, "mid": v(105.69, -27.65) * mm, "end": v(105.05, -27.33) * mm});
            skArc(sketch, "E66.7.206.0", {"start": v(104.75, -28.48) * mm, "mid": v(105.45, -28.52) * mm, "end": v(106.1, -28.22) * mm});
            skLineSegment(sketch, "E66.11.206.0", {"start": v(103.5, -28.09) * mm, "end": v(104.75, -28.48) * mm});
            skLineSegment(sketch, "E66.1.207.0", {"start": v(104.34, -24.8) * mm, "end": v(105.62, -25.05) * mm});
            skArc(sketch, "E66.3.207.0", {"start": v(106.68, -25.92) * mm, "mid": v(106.26, -25.35) * mm, "end": v(105.62, -25.05) * mm});
            skArc(sketch, "E66.7.207.0", {"start": v(105.34, -26.2) * mm, "mid": v(106.05, -26.23) * mm, "end": v(106.68, -25.92) * mm});
            skLineSegment(sketch, "E66.11.207.0", {"start": v(104.1, -25.84) * mm, "end": v(105.34, -26.2) * mm});
            skLineSegment(sketch, "E66.1.208.0", {"start": v(104.86, -22.53) * mm, "end": v(106.14, -22.76) * mm});
            skArc(sketch, "E66.3.208.0", {"start": v(107.22, -23.6) * mm, "mid": v(106.78, -23.04) * mm, "end": v(106.14, -22.76) * mm});
            skArc(sketch, "E66.7.208.0", {"start": v(105.88, -23.91) * mm, "mid": v(106.6, -23.93) * mm, "end": v(107.22, -23.6) * mm});
            skLineSegment(sketch, "E66.11.208.0", {"start": v(104.63, -23.58) * mm, "end": v(105.88, -23.91) * mm});
            skLineSegment(sketch, "E66.1.209.0", {"start": v(105.32, -20.26) * mm, "end": v(106.6, -20.45) * mm});
            skArc(sketch, "E66.3.209.0", {"start": v(107.7, -21.27) * mm, "mid": v(107.26, -20.72) * mm, "end": v(106.6, -20.45) * mm});
            skArc(sketch, "E66.7.209.0", {"start": v(106.38, -21.61) * mm, "mid": v(107.08, -21.61) * mm, "end": v(107.7, -21.27) * mm});
            skLineSegment(sketch, "E66.11.209.0", {"start": v(105.11, -21.3) * mm, "end": v(106.38, -21.61) * mm});
            skLineSegment(sketch, "E66.1.210.0", {"start": v(105.73, -17.97) * mm, "end": v(107.02, -18.14) * mm});
            skArc(sketch, "E66.3.210.0", {"start": v(108.14, -18.93) * mm, "mid": v(107.68, -18.4) * mm, "end": v(107.02, -18.14) * mm});
            skArc(sketch, "E66.7.210.0", {"start": v(106.82, -19.3) * mm, "mid": v(107.53, -19.29) * mm, "end": v(108.14, -18.93) * mm});
            skLineSegment(sketch, "E66.11.210.0", {"start": v(105.55, -19.02) * mm, "end": v(106.82, -19.3) * mm});
            skLineSegment(sketch, "E66.1.211.0", {"start": v(106.1, -15.68) * mm, "end": v(107.4, -15.81) * mm});
            skArc(sketch, "E66.3.211.0", {"start": v(108.52, -16.59) * mm, "mid": v(108.06, -16.06) * mm, "end": v(107.4, -15.81) * mm});
            skArc(sketch, "E66.7.211.0", {"start": v(107.21, -16.99) * mm, "mid": v(107.92, -16.95) * mm, "end": v(108.52, -16.59) * mm});
            skLineSegment(sketch, "E66.11.211.0", {"start": v(105.94, -16.73) * mm, "end": v(107.21, -16.99) * mm});
            skLineSegment(sketch, "E66.1.212.0", {"start": v(106.41, -13.37) * mm, "end": v(107.71, -13.48) * mm});
            skArc(sketch, "E66.3.212.0", {"start": v(108.86, -14.23) * mm, "mid": v(108.38, -13.71) * mm, "end": v(107.71, -13.48) * mm});
            skArc(sketch, "E66.7.212.0", {"start": v(107.56, -14.66) * mm, "mid": v(108.26, -14.6) * mm, "end": v(108.86, -14.23) * mm});
            skLineSegment(sketch, "E66.11.212.0", {"start": v(106.27, -14.43) * mm, "end": v(107.56, -14.66) * mm});
            skLineSegment(sketch, "E66.1.213.0", {"start": v(106.68, -11.06) * mm, "end": v(107.98, -11.15) * mm});
            skArc(sketch, "E66.3.213.0", {"start": v(109.14, -11.87) * mm, "mid": v(108.65, -11.36) * mm, "end": v(107.98, -11.15) * mm});
            skArc(sketch, "E66.7.213.0", {"start": v(107.85, -12.33) * mm, "mid": v(108.55, -12.26) * mm, "end": v(109.14, -11.87) * mm});
            skLineSegment(sketch, "E66.11.213.0", {"start": v(106.56, -12.13) * mm, "end": v(107.85, -12.33) * mm});
            skLineSegment(sketch, "E66.1.214.0", {"start": v(106.9, -8.75) * mm, "end": v(108.2, -8.8) * mm});
            skArc(sketch, "E66.3.214.0", {"start": v(109.37, -9.5) * mm, "mid": v(108.87, -9) * mm, "end": v(108.2, -8.8) * mm});
            skArc(sketch, "E66.7.214.0", {"start": v(108.1, -9.99) * mm, "mid": v(108.8, -9.9) * mm, "end": v(109.37, -9.5) * mm});
            skLineSegment(sketch, "E66.11.214.0", {"start": v(106.8, -9.81) * mm, "end": v(108.1, -9.99) * mm});
            skLineSegment(sketch, "E66.1.215.0", {"start": v(107.06, -6.43) * mm, "end": v(108.36, -6.46) * mm});
            skArc(sketch, "E66.3.215.0", {"start": v(109.55, -7.13) * mm, "mid": v(109.04, -6.64) * mm, "end": v(108.36, -6.46) * mm});
            skArc(sketch, "E66.7.215.0", {"start": v(108.28, -7.64) * mm, "mid": v(108.98, -7.55) * mm, "end": v(109.55, -7.13) * mm});
            skLineSegment(sketch, "E66.11.215.0", {"start": v(106.99, -7.5) * mm, "end": v(108.28, -7.64) * mm});
            skLineSegment(sketch, "E66.1.216.0", {"start": v(107.17, -4.11) * mm, "end": v(108.47, -4.1) * mm});
            skArc(sketch, "E66.3.216.0", {"start": v(109.68, -4.76) * mm, "mid": v(109.16, -4.28) * mm, "end": v(108.47, -4.1) * mm});
            skArc(sketch, "E66.7.216.0", {"start": v(108.42, -5.3) * mm, "mid": v(109.12, -5.18) * mm, "end": v(109.68, -4.76) * mm});
            skLineSegment(sketch, "E66.11.216.0", {"start": v(107.12, -5.18) * mm, "end": v(108.42, -5.3) * mm});
            skLineSegment(sketch, "E66.1.217.0", {"start": v(107.24, -1.79) * mm, "end": v(108.54, -1.76) * mm});
            skArc(sketch, "E66.3.217.0", {"start": v(109.76, -2.38) * mm, "mid": v(109.23, -1.91) * mm, "end": v(108.54, -1.76) * mm});
            skArc(sketch, "E66.7.217.0", {"start": v(108.51, -2.94) * mm, "mid": v(109.2, -2.82) * mm, "end": v(109.76, -2.38) * mm});
            skLineSegment(sketch, "E66.11.217.0", {"start": v(107.21, -2.86) * mm, "end": v(108.51, -2.94) * mm});
            skLineSegment(sketch, "E66.1.218.0", {"start": v(107.25, 0.53) * mm, "end": v(108.55, 0.6) * mm});
            skArc(sketch, "E66.3.218.0", {"start": v(109.78, 0) * mm, "mid": v(109.24, 0.45) * mm, "end": v(108.55, 0.6) * mm});
            skArc(sketch, "E66.7.218.0", {"start": v(108.55, -0.6) * mm, "mid": v(109.24, -0.45) * mm, "end": v(109.79, 0) * mm});
            skLineSegment(sketch, "E66.11.218.0", {"start": v(107.25, -0.53) * mm, "end": v(108.55, -0.6) * mm});
            skLineSegment(sketch, "E66.1.219.0", {"start": v(107.21, 2.86) * mm, "end": v(108.51, 2.94) * mm});
            skArc(sketch, "E66.3.219.0", {"start": v(109.76, 2.38) * mm, "mid": v(109.2, 2.82) * mm, "end": v(108.51, 2.94) * mm});
            skArc(sketch, "E66.7.219.0", {"start": v(108.54, 1.76) * mm, "mid": v(109.23, 1.91) * mm, "end": v(109.76, 2.38) * mm});
            skLineSegment(sketch, "E66.11.219.0", {"start": v(107.24, 1.79) * mm, "end": v(108.54, 1.76) * mm});
            skLineSegment(sketch, "E66.1.220.0", {"start": v(107.12, 5.18) * mm, "end": v(108.42, 5.3) * mm});
            skArc(sketch, "E66.3.220.0", {"start": v(109.68, 4.76) * mm, "mid": v(109.12, 5.18) * mm, "end": v(108.42, 5.3) * mm});
            skArc(sketch, "E66.7.220.0", {"start": v(108.47, 4.1) * mm, "mid": v(109.16, 4.28) * mm, "end": v(109.68, 4.76) * mm});
            skLineSegment(sketch, "E66.11.220.0", {"start": v(107.17, 4.11) * mm, "end": v(108.47, 4.1) * mm});
            skLineSegment(sketch, "E66.1.221.0", {"start": v(106.99, 7.5) * mm, "end": v(108.28, 7.64) * mm});
            skArc(sketch, "E66.3.221.0", {"start": v(109.55, 7.13) * mm, "mid": v(108.98, 7.55) * mm, "end": v(108.28, 7.64) * mm});
            skArc(sketch, "E66.7.221.0", {"start": v(108.36, 6.46) * mm, "mid": v(109.04, 6.64) * mm, "end": v(109.55, 7.13) * mm});
            skLineSegment(sketch, "E66.11.221.0", {"start": v(107.06, 6.43) * mm, "end": v(108.36, 6.46) * mm});
            skLineSegment(sketch, "E66.1.222.0", {"start": v(106.8, 9.81) * mm, "end": v(108.1, 9.99) * mm});
            skArc(sketch, "E66.3.222.0", {"start": v(109.37, 9.5) * mm, "mid": v(108.8, 9.9) * mm, "end": v(108.1, 9.99) * mm});
            skArc(sketch, "E66.7.222.0", {"start": v(108.2, 8.8) * mm, "mid": v(108.87, 9) * mm, "end": v(109.37, 9.5) * mm});
            skLineSegment(sketch, "E66.11.222.0", {"start": v(106.9, 8.75) * mm, "end": v(108.2, 8.8) * mm});
            skLineSegment(sketch, "E66.1.223.0", {"start": v(106.56, 12.13) * mm, "end": v(107.85, 12.33) * mm});
            skArc(sketch, "E66.3.223.0", {"start": v(109.14, 11.87) * mm, "mid": v(108.55, 12.26) * mm, "end": v(107.85, 12.33) * mm});
            skArc(sketch, "E66.7.223.0", {"start": v(107.98, 11.15) * mm, "mid": v(108.65, 11.36) * mm, "end": v(109.14, 11.87) * mm});
            skLineSegment(sketch, "E66.11.223.0", {"start": v(106.68, 11.06) * mm, "end": v(107.98, 11.15) * mm});
            skLineSegment(sketch, "E66.1.224.0", {"start": v(106.27, 14.43) * mm, "end": v(107.56, 14.66) * mm});
            skArc(sketch, "E66.3.224.0", {"start": v(108.86, 14.23) * mm, "mid": v(108.26, 14.6) * mm, "end": v(107.56, 14.66) * mm});
            skArc(sketch, "E66.7.224.0", {"start": v(107.71, 13.48) * mm, "mid": v(108.38, 13.71) * mm, "end": v(108.86, 14.23) * mm});
            skLineSegment(sketch, "E66.11.224.0", {"start": v(106.41, 13.37) * mm, "end": v(107.71, 13.48) * mm});
            skLineSegment(sketch, "E66.1.225.0", {"start": v(105.94, 16.73) * mm, "end": v(107.21, 16.99) * mm});
            skArc(sketch, "E66.3.225.0", {"start": v(108.52, 16.59) * mm, "mid": v(107.92, 16.95) * mm, "end": v(107.21, 16.99) * mm});
            skArc(sketch, "E66.7.225.0", {"start": v(107.4, 15.81) * mm, "mid": v(108.06, 16.06) * mm, "end": v(108.52, 16.59) * mm});
            skLineSegment(sketch, "E66.11.225.0", {"start": v(106.1, 15.68) * mm, "end": v(107.4, 15.81) * mm});
            skLineSegment(sketch, "E66.1.226.0", {"start": v(105.55, 19.02) * mm, "end": v(106.82, 19.3) * mm});
            skArc(sketch, "E66.3.226.0", {"start": v(108.14, 18.93) * mm, "mid": v(107.53, 19.29) * mm, "end": v(106.82, 19.3) * mm});
            skArc(sketch, "E66.7.226.0", {"start": v(107.02, 18.14) * mm, "mid": v(107.68, 18.4) * mm, "end": v(108.14, 18.93) * mm});
            skLineSegment(sketch, "E66.11.226.0", {"start": v(105.73, 17.97) * mm, "end": v(107.02, 18.14) * mm});
            skLineSegment(sketch, "E66.1.227.0", {"start": v(105.11, 21.3) * mm, "end": v(106.38, 21.61) * mm});
            skArc(sketch, "E66.3.227.0", {"start": v(107.7, 21.27) * mm, "mid": v(107.08, 21.61) * mm, "end": v(106.38, 21.61) * mm});
            skArc(sketch, "E66.7.227.0", {"start": v(106.6, 20.45) * mm, "mid": v(107.26, 20.72) * mm, "end": v(107.7, 21.27) * mm});
            skLineSegment(sketch, "E66.11.227.0", {"start": v(105.32, 20.26) * mm, "end": v(106.6, 20.45) * mm});
            skLineSegment(sketch, "E66.1.228.0", {"start": v(104.63, 23.58) * mm, "end": v(105.88, 23.91) * mm});
            skArc(sketch, "E66.3.228.0", {"start": v(107.22, 23.6) * mm, "mid": v(106.6, 23.93) * mm, "end": v(105.88, 23.91) * mm});
            skArc(sketch, "E66.7.228.0", {"start": v(106.14, 22.76) * mm, "mid": v(106.78, 23.04) * mm, "end": v(107.22, 23.6) * mm});
            skLineSegment(sketch, "E66.11.228.0", {"start": v(104.86, 22.53) * mm, "end": v(106.14, 22.76) * mm});
            skLineSegment(sketch, "E66.1.229.0", {"start": v(104.1, 25.84) * mm, "end": v(105.34, 26.2) * mm});
            skArc(sketch, "E66.3.229.0", {"start": v(106.68, 25.92) * mm, "mid": v(106.05, 26.23) * mm, "end": v(105.34, 26.2) * mm});
            skArc(sketch, "E66.7.229.0", {"start": v(105.62, 25.05) * mm, "mid": v(106.26, 25.35) * mm, "end": v(106.68, 25.92) * mm});
            skLineSegment(sketch, "E66.11.229.0", {"start": v(104.34, 24.8) * mm, "end": v(105.62, 25.05) * mm});
            skLineSegment(sketch, "E66.1.230.0", {"start": v(103.5, 28.09) * mm, "end": v(104.75, 28.48) * mm});
            skArc(sketch, "E66.3.230.0", {"start": v(106.1, 28.22) * mm, "mid": v(105.45, 28.52) * mm, "end": v(104.75, 28.48) * mm});
            skArc(sketch, "E66.7.230.0", {"start": v(105.05, 27.33) * mm, "mid": v(105.69, 27.65) * mm, "end": v(106.1, 28.22) * mm});
            skLineSegment(sketch, "E66.11.230.0", {"start": v(103.78, 27.06) * mm, "end": v(105.05, 27.33) * mm});
            skLineSegment(sketch, "E66.1.231.0", {"start": v(102.87, 30.32) * mm, "end": v(104.1, 30.74) * mm});
            skArc(sketch, "E66.3.231.0", {"start": v(105.46, 30.51) * mm, "mid": v(104.81, 30.8) * mm, "end": v(104.1, 30.74) * mm});
            skArc(sketch, "E66.7.231.0", {"start": v(104.44, 29.6) * mm, "mid": v(105.06, 29.93) * mm, "end": v(105.46, 30.51) * mm});
            skLineSegment(sketch, "E66.11.231.0", {"start": v(103.17, 29.3) * mm, "end": v(104.44, 29.6) * mm});
            skLineSegment(sketch, "E66.1.232.0", {"start": v(102.2, 32.54) * mm, "end": v(103.42, 32.99) * mm});
            skArc(sketch, "E66.3.232.0", {"start": v(104.77, 32.8) * mm, "mid": v(104.12, 33.06) * mm, "end": v(103.42, 32.99) * mm});
            skArc(sketch, "E66.7.232.0", {"start": v(103.77, 31.86) * mm, "mid": v(104.39, 32.2) * mm, "end": v(104.77, 32.8) * mm});
            skLineSegment(sketch, "E66.11.232.0", {"start": v(102.51, 31.53) * mm, "end": v(103.77, 31.86) * mm});
            skLineSegment(sketch, "E66.1.233.0", {"start": v(101.46, 34.75) * mm, "end": v(102.68, 35.22) * mm});
            skArc(sketch, "E66.3.233.0", {"start": v(104.04, 35.05) * mm, "mid": v(103.38, 35.3) * mm, "end": v(102.68, 35.22) * mm});
            skArc(sketch, "E66.7.233.0", {"start": v(103.06, 34.1) * mm, "mid": v(103.67, 34.45) * mm, "end": v(104.04, 35.05) * mm});
            skLineSegment(sketch, "E66.11.233.0", {"start": v(101.8, 33.74) * mm, "end": v(103.06, 34.1) * mm});
            skLineSegment(sketch, "E66.1.234.0", {"start": v(100.69, 36.94) * mm, "end": v(101.9, 37.44) * mm});
            skArc(sketch, "E66.3.234.0", {"start": v(103.25, 37.3) * mm, "mid": v(102.59, 37.54) * mm, "end": v(101.9, 37.44) * mm});
            skArc(sketch, "E66.7.234.0", {"start": v(102.3, 36.32) * mm, "mid": v(102.9, 36.7) * mm, "end": v(103.25, 37.3) * mm});
            skLineSegment(sketch, "E66.11.234.0", {"start": v(101.05, 35.94) * mm, "end": v(102.3, 36.32) * mm});
            skLineSegment(sketch, "E66.1.235.0", {"start": v(99.86, 39.11) * mm, "end": v(101.06, 39.64) * mm});
            skArc(sketch, "E66.3.235.0", {"start": v(102.42, 39.53) * mm, "mid": v(101.75, 39.75) * mm, "end": v(101.06, 39.64) * mm});
            skArc(sketch, "E66.7.235.0", {"start": v(101.48, 38.53) * mm, "mid": v(102.08, 38.91) * mm, "end": v(102.42, 39.53) * mm});
            skLineSegment(sketch, "E66.11.235.0", {"start": v(100.25, 38.12) * mm, "end": v(101.48, 38.53) * mm});
            skLineSegment(sketch, "E66.1.236.0", {"start": v(99, 41.27) * mm, "end": v(100.17, 41.82) * mm});
            skArc(sketch, "E66.3.236.0", {"start": v(101.54, 41.74) * mm, "mid": v(100.87, 41.95) * mm, "end": v(100.17, 41.82) * mm});
            skArc(sketch, "E66.7.236.0", {"start": v(100.62, 40.72) * mm, "mid": v(101.21, 41.11) * mm, "end": v(101.54, 41.74) * mm});
            skLineSegment(sketch, "E66.11.236.0", {"start": v(99.4, 40.28) * mm, "end": v(100.62, 40.72) * mm});
            skLineSegment(sketch, "E66.1.237.0", {"start": v(98.08, 43.4) * mm, "end": v(99.24, 43.98) * mm});
            skArc(sketch, "E66.3.237.0", {"start": v(100.61, 43.93) * mm, "mid": v(99.93, 44.13) * mm, "end": v(99.24, 43.98) * mm});
            skArc(sketch, "E66.7.237.0", {"start": v(99.72, 42.89) * mm, "mid": v(100.3, 43.3) * mm, "end": v(100.61, 43.93) * mm});
            skLineSegment(sketch, "E66.11.237.0", {"start": v(98.5, 42.42) * mm, "end": v(99.72, 42.89) * mm});
            skLineSegment(sketch, "E66.1.238.0", {"start": v(97.11, 45.52) * mm, "end": v(98.27, 46.12) * mm});
            skArc(sketch, "E66.3.238.0", {"start": v(99.64, 46.1) * mm, "mid": v(98.96, 46.28) * mm, "end": v(98.27, 46.12) * mm});
            skArc(sketch, "E66.7.238.0", {"start": v(98.77, 45.04) * mm, "mid": v(99.34, 45.46) * mm, "end": v(99.64, 46.1) * mm});
            skLineSegment(sketch, "E66.11.238.0", {"start": v(97.56, 44.55) * mm, "end": v(98.77, 45.04) * mm});
            skLineSegment(sketch, "E66.1.239.0", {"start": v(96.1, 47.61) * mm, "end": v(97.25, 48.24) * mm});
            skArc(sketch, "E66.3.239.0", {"start": v(98.62, 48.25) * mm, "mid": v(97.93, 48.41) * mm, "end": v(97.25, 48.24) * mm});
            skArc(sketch, "E66.7.239.0", {"start": v(97.77, 47.17) * mm, "mid": v(98.33, 47.6) * mm, "end": v(98.62, 48.25) * mm});
            skLineSegment(sketch, "E66.11.239.0", {"start": v(96.57, 46.65) * mm, "end": v(97.77, 47.17) * mm});
            skLineSegment(sketch, "E66.1.240.0", {"start": v(95.05, 49.68) * mm, "end": v(96.18, 50.33) * mm});
            skArc(sketch, "E66.3.240.0", {"start": v(97.55, 50.37) * mm, "mid": v(96.86, 50.52) * mm, "end": v(96.18, 50.33) * mm});
            skArc(sketch, "E66.7.240.0", {"start": v(96.72, 49.28) * mm, "mid": v(97.27, 49.72) * mm, "end": v(97.55, 50.37) * mm});
            skLineSegment(sketch, "E66.11.240.0", {"start": v(95.54, 48.73) * mm, "end": v(96.72, 49.28) * mm});
            skLineSegment(sketch, "E66.1.241.0", {"start": v(93.95, 51.73) * mm, "end": v(95.06, 52.4) * mm});
            skArc(sketch, "E66.3.241.0", {"start": v(96.43, 52.47) * mm, "mid": v(95.74, 52.6) * mm, "end": v(95.06, 52.4) * mm});
            skArc(sketch, "E66.7.241.0", {"start": v(95.63, 51.36) * mm, "mid": v(96.17, 51.82) * mm, "end": v(96.43, 52.47) * mm});
            skLineSegment(sketch, "E66.11.241.0", {"start": v(94.46, 50.8) * mm, "end": v(95.63, 51.36) * mm});
            skLineSegment(sketch, "E66.1.242.0", {"start": v(92.8, 53.75) * mm, "end": v(93.9, 54.45) * mm});
            skArc(sketch, "E66.3.242.0", {"start": v(95.27, 54.55) * mm, "mid": v(94.58, 54.67) * mm, "end": v(93.9, 54.45) * mm});
            skArc(sketch, "E66.7.242.0", {"start": v(94.5, 53.42) * mm, "mid": v(95.03, 53.89) * mm, "end": v(95.27, 54.55) * mm});
            skLineSegment(sketch, "E66.11.242.0", {"start": v(93.34, 52.83) * mm, "end": v(94.5, 53.42) * mm});
            skLineSegment(sketch, "E66.1.243.0", {"start": v(91.62, 55.75) * mm, "end": v(92.7, 56.47) * mm});
            skArc(sketch, "E66.3.243.0", {"start": v(94.07, 56.6) * mm, "mid": v(93.37, 56.7) * mm, "end": v(92.7, 56.47) * mm});
            skArc(sketch, "E66.7.243.0", {"start": v(93.32, 55.45) * mm, "mid": v(93.84, 55.93) * mm, "end": v(94.07, 56.6) * mm});
            skLineSegment(sketch, "E66.11.243.0", {"start": v(92.17, 54.84) * mm, "end": v(93.32, 55.45) * mm});
            skLineSegment(sketch, "E66.1.244.0", {"start": v(90.4, 57.72) * mm, "end": v(91.46, 58.47) * mm});
            skArc(sketch, "E66.3.244.0", {"start": v(92.82, 58.62) * mm, "mid": v(92.12, 58.72) * mm, "end": v(91.46, 58.47) * mm});
            skArc(sketch, "E66.7.244.0", {"start": v(92.1, 57.46) * mm, "mid": v(92.6, 57.95) * mm, "end": v(92.82, 58.62) * mm});
            skLineSegment(sketch, "E66.11.244.0", {"start": v(90.96, 56.82) * mm, "end": v(92.1, 57.46) * mm});
            skLineSegment(sketch, "E66.1.245.0", {"start": v(89.12, 59.67) * mm, "end": v(90.17, 60.43) * mm});
            skArc(sketch, "E66.3.245.0", {"start": v(91.53, 60.62) * mm, "mid": v(90.83, 60.7) * mm, "end": v(90.17, 60.43) * mm});
            skArc(sketch, "E66.7.245.0", {"start": v(90.83, 59.44) * mm, "mid": v(91.33, 59.94) * mm, "end": v(91.53, 60.62) * mm});
            skLineSegment(sketch, "E66.11.245.0", {"start": v(89.71, 58.78) * mm, "end": v(90.83, 59.44) * mm});
            skLineSegment(sketch, "E66.1.246.0", {"start": v(87.8, 61.58) * mm, "end": v(88.84, 62.37) * mm});
            skArc(sketch, "E66.3.246.0", {"start": v(90.2, 62.6) * mm, "mid": v(89.5, 62.65) * mm, "end": v(88.84, 62.37) * mm});
            skArc(sketch, "E66.7.246.0", {"start": v(89.52, 61.4) * mm, "mid": v(90, 61.9) * mm, "end": v(90.2, 62.6) * mm});
            skLineSegment(sketch, "E66.11.246.0", {"start": v(88.42, 60.7) * mm, "end": v(89.52, 61.4) * mm});
            skLineSegment(sketch, "E66.1.247.0", {"start": v(86.45, 63.47) * mm, "end": v(87.47, 64.28) * mm});
            skArc(sketch, "E66.3.247.0", {"start": v(88.82, 64.53) * mm, "mid": v(88.11, 64.58) * mm, "end": v(87.47, 64.28) * mm});
            skArc(sketch, "E66.7.247.0", {"start": v(88.17, 63.32) * mm, "mid": v(88.64, 63.84) * mm, "end": v(88.82, 64.53) * mm});
            skLineSegment(sketch, "E66.11.247.0", {"start": v(87.08, 62.6) * mm, "end": v(88.17, 63.32) * mm});
            skLineSegment(sketch, "E66.1.248.0", {"start": v(85.06, 65.33) * mm, "end": v(86.06, 66.16) * mm});
            skArc(sketch, "E66.3.248.0", {"start": v(87.4, 66.44) * mm, "mid": v(86.7, 66.47) * mm, "end": v(86.06, 66.16) * mm});
            skArc(sketch, "E66.7.248.0", {"start": v(86.77, 65.22) * mm, "mid": v(87.24, 65.75) * mm, "end": v(87.4, 66.44) * mm});
            skLineSegment(sketch, "E66.11.248.0", {"start": v(85.7, 64.48) * mm, "end": v(86.77, 65.22) * mm});
            skLineSegment(sketch, "E66.1.249.0", {"start": v(83.62, 67.16) * mm, "end": v(84.6, 68.01) * mm});
            skArc(sketch, "E66.3.249.0", {"start": v(85.94, 68.32) * mm, "mid": v(85.23, 68.33) * mm, "end": v(84.6, 68.01) * mm});
            skArc(sketch, "E66.7.249.0", {"start": v(85.34, 67.08) * mm, "mid": v(85.8, 67.62) * mm, "end": v(85.94, 68.32) * mm});
            skLineSegment(sketch, "E66.11.249.0", {"start": v(84.29, 66.32) * mm, "end": v(85.34, 67.08) * mm});
            skLineSegment(sketch, "E66.1.250.0", {"start": v(82.15, 68.95) * mm, "end": v(83.1, 69.83) * mm});
            skArc(sketch, "E66.3.250.0", {"start": v(84.44, 70.16) * mm, "mid": v(83.73, 70.16) * mm, "end": v(83.1, 69.83) * mm});
            skArc(sketch, "E66.7.250.0", {"start": v(83.87, 68.92) * mm, "mid": v(84.31, 69.47) * mm, "end": v(84.44, 70.16) * mm});
            skLineSegment(sketch, "E66.11.250.0", {"start": v(82.83, 68.13) * mm, "end": v(83.87, 68.92) * mm});
            skLineSegment(sketch, "E66.1.251.0", {"start": v(80.63, 70.72) * mm, "end": v(81.58, 71.61) * mm});
            skArc(sketch, "E66.3.251.0", {"start": v(82.9, 71.98) * mm, "mid": v(82.2, 71.96) * mm, "end": v(81.58, 71.61) * mm});
            skArc(sketch, "E66.7.251.0", {"start": v(82.35, 70.72) * mm, "mid": v(82.79, 71.28) * mm, "end": v(82.9, 71.98) * mm});
            skLineSegment(sketch, "E66.11.251.0", {"start": v(81.33, 69.9) * mm, "end": v(82.35, 70.72) * mm});
            skLineSegment(sketch, "E66.1.252.0", {"start": v(79.08, 72.45) * mm, "end": v(80, 73.36) * mm});
            skArc(sketch, "E66.3.252.0", {"start": v(81.32, 73.75) * mm, "mid": v(80.61, 73.72) * mm, "end": v(80, 73.36) * mm});
            skArc(sketch, "E66.7.252.0", {"start": v(80.8, 72.48) * mm, "mid": v(81.22, 73.05) * mm, "end": v(81.32, 73.75) * mm});
            skLineSegment(sketch, "E66.11.252.0", {"start": v(79.8, 71.66) * mm, "end": v(80.8, 72.48) * mm});
            skLineSegment(sketch, "E66.1.253.0", {"start": v(77.5, 74.14) * mm, "end": v(78.4, 75.08) * mm});
            skArc(sketch, "E66.3.253.0", {"start": v(79.7, 75.5) * mm, "mid": v(79, 75.45) * mm, "end": v(78.4, 75.08) * mm});
            skArc(sketch, "E66.7.253.0", {"start": v(79.21, 74.22) * mm, "mid": v(79.62, 74.8) * mm, "end": v(79.7, 75.5) * mm});
            skLineSegment(sketch, "E66.11.253.0", {"start": v(78.23, 73.37) * mm, "end": v(79.21, 74.22) * mm});
            skLineSegment(sketch, "E66.1.254.0", {"start": v(75.87, 75.8) * mm, "end": v(76.75, 76.76) * mm});
            skArc(sketch, "E66.3.254.0", {"start": v(78.05, 77.2) * mm, "mid": v(77.34, 77.15) * mm, "end": v(76.75, 76.76) * mm});
            skArc(sketch, "E66.7.254.0", {"start": v(77.59, 75.92) * mm, "mid": v(77.98, 76.5) * mm, "end": v(78.05, 77.2) * mm});
            skLineSegment(sketch, "E66.11.254.0", {"start": v(76.62, 75.04) * mm, "end": v(77.59, 75.92) * mm});
            skLineSegment(sketch, "E66.1.255.0", {"start": v(74.21, 77.43) * mm, "end": v(75.07, 78.4) * mm});
            skArc(sketch, "E66.3.255.0", {"start": v(76.36, 78.88) * mm, "mid": v(75.66, 78.8) * mm, "end": v(75.07, 78.4) * mm});
            skArc(sketch, "E66.7.255.0", {"start": v(75.92, 77.58) * mm, "mid": v(76.3, 78.18) * mm, "end": v(76.36, 78.88) * mm});
            skLineSegment(sketch, "E66.11.255.0", {"start": v(74.98, 76.69) * mm, "end": v(75.92, 77.58) * mm});
            skLineSegment(sketch, "E66.1.256.0", {"start": v(72.52, 79.02) * mm, "end": v(73.36, 80.01) * mm});
            skArc(sketch, "E66.3.256.0", {"start": v(74.63, 80.52) * mm, "mid": v(73.93, 80.43) * mm, "end": v(73.36, 80.01) * mm});
            skArc(sketch, "E66.7.256.0", {"start": v(74.23, 79.2) * mm, "mid": v(74.6, 79.81) * mm, "end": v(74.63, 80.52) * mm});
            skLineSegment(sketch, "E66.11.256.0", {"start": v(73.3, 78.3) * mm, "end": v(74.23, 79.2) * mm});
            skLineSegment(sketch, "E66.1.257.0", {"start": v(70.79, 80.57) * mm, "end": v(71.6, 81.58) * mm});
            skArc(sketch, "E66.3.257.0", {"start": v(72.87, 82.11) * mm, "mid": v(72.17, 82) * mm, "end": v(71.6, 81.58) * mm});
            skArc(sketch, "E66.7.257.0", {"start": v(72.5, 80.8) * mm, "mid": v(72.85, 81.4) * mm, "end": v(72.87, 82.11) * mm});
            skLineSegment(sketch, "E66.11.257.0", {"start": v(71.59, 79.86) * mm, "end": v(72.5, 80.8) * mm});
            skLineSegment(sketch, "E66.1.258.0", {"start": v(69.02, 82.09) * mm, "end": v(69.82, 83.12) * mm});
            skArc(sketch, "E66.3.258.0", {"start": v(71.07, 83.67) * mm, "mid": v(70.38, 83.55) * mm, "end": v(69.82, 83.12) * mm});
            skArc(sketch, "E66.7.258.0", {"start": v(70.73, 82.35) * mm, "mid": v(71.07, 82.97) * mm, "end": v(71.07, 83.67) * mm});
            skLineSegment(sketch, "E66.11.258.0", {"start": v(69.84, 81.4) * mm, "end": v(70.73, 82.35) * mm});
            skLineSegment(sketch, "E66.1.259.0", {"start": v(67.23, 83.56) * mm, "end": v(68, 84.6) * mm});
            skArc(sketch, "E66.3.259.0", {"start": v(69.24, 85.2) * mm, "mid": v(68.55, 85.06) * mm, "end": v(68, 84.6) * mm});
            skArc(sketch, "E66.7.259.0", {"start": v(68.92, 83.86) * mm, "mid": v(69.25, 84.49) * mm, "end": v(69.24, 85.2) * mm});
            skLineSegment(sketch, "E66.11.259.0", {"start": v(68.06, 82.89) * mm, "end": v(68.92, 83.86) * mm});
            skLineSegment(sketch, "E66.1.260.0", {"start": v(65.4, 85) * mm, "end": v(66.15, 86.06) * mm});
            skArc(sketch, "E66.3.260.0", {"start": v(67.38, 86.67) * mm, "mid": v(66.7, 86.52) * mm, "end": v(66.15, 86.06) * mm});
            skArc(sketch, "E66.7.260.0", {"start": v(67.1, 85.33) * mm, "mid": v(67.4, 85.97) * mm, "end": v(67.38, 86.67) * mm});
            skLineSegment(sketch, "E66.11.260.0", {"start": v(66.25, 84.34) * mm, "end": v(67.1, 85.33) * mm});
            skLineSegment(sketch, "E66.1.261.0", {"start": v(63.55, 86.4) * mm, "end": v(64.27, 87.48) * mm});
            skArc(sketch, "E66.3.261.0", {"start": v(65.49, 88.11) * mm, "mid": v(64.8, 87.95) * mm, "end": v(64.27, 87.48) * mm});
            skArc(sketch, "E66.7.261.0", {"start": v(65.23, 86.77) * mm, "mid": v(65.53, 87.4) * mm, "end": v(65.49, 88.11) * mm});
            skLineSegment(sketch, "E66.11.261.0", {"start": v(64.4, 85.76) * mm, "end": v(65.23, 86.77) * mm});
            skLineSegment(sketch, "E66.1.262.0", {"start": v(61.66, 87.75) * mm, "end": v(62.36, 88.85) * mm});
            skArc(sketch, "E66.3.262.0", {"start": v(63.56, 89.51) * mm, "mid": v(62.88, 89.33) * mm, "end": v(62.36, 88.85) * mm});
            skArc(sketch, "E66.7.262.0", {"start": v(63.33, 88.16) * mm, "mid": v(63.62, 88.8) * mm, "end": v(63.56, 89.51) * mm});
            skLineSegment(sketch, "E66.11.262.0", {"start": v(62.53, 87.13) * mm, "end": v(63.33, 88.16) * mm});
            skLineSegment(sketch, "E66.1.263.0", {"start": v(59.74, 89.07) * mm, "end": v(60.43, 90.18) * mm});
            skArc(sketch, "E66.3.263.0", {"start": v(61.6, 90.87) * mm, "mid": v(60.93, 90.67) * mm, "end": v(60.43, 90.18) * mm});
            skArc(sketch, "E66.7.263.0", {"start": v(61.4, 89.51) * mm, "mid": v(61.68, 90.16) * mm, "end": v(61.6, 90.87) * mm});
            skLineSegment(sketch, "E66.11.263.0", {"start": v(60.63, 88.47) * mm, "end": v(61.4, 89.51) * mm});
            skLineSegment(sketch, "E66.1.264.0", {"start": v(57.8, 90.34) * mm, "end": v(58.46, 91.47) * mm});
            skArc(sketch, "E66.3.264.0", {"start": v(59.63, 92.18) * mm, "mid": v(58.95, 91.97) * mm, "end": v(58.46, 91.47) * mm});
            skArc(sketch, "E66.7.264.0", {"start": v(59.45, 90.82) * mm, "mid": v(59.71, 91.48) * mm, "end": v(59.63, 92.18) * mm});
            skLineSegment(sketch, "E66.11.264.0", {"start": v(58.7, 89.76) * mm, "end": v(59.45, 90.82) * mm});
            skLineSegment(sketch, "E66.1.265.0", {"start": v(55.83, 91.57) * mm, "end": v(56.46, 92.71) * mm});
            skArc(sketch, "E66.3.265.0", {"start": v(57.62, 93.45) * mm, "mid": v(56.95, 93.23) * mm, "end": v(56.46, 92.71) * mm});
            skArc(sketch, "E66.7.265.0", {"start": v(57.47, 92.09) * mm, "mid": v(57.72, 92.75) * mm, "end": v(57.62, 93.45) * mm});
            skLineSegment(sketch, "E66.11.265.0", {"start": v(56.74, 91.01) * mm, "end": v(57.47, 92.09) * mm});
            skLineSegment(sketch, "E66.1.266.0", {"start": v(53.83, 92.76) * mm, "end": v(54.44, 93.91) * mm});
            skArc(sketch, "E66.3.266.0", {"start": v(55.58, 94.68) * mm, "mid": v(54.91, 94.44) * mm, "end": v(54.44, 93.91) * mm});
            skArc(sketch, "E66.7.266.0", {"start": v(55.46, 93.31) * mm, "mid": v(55.7, 93.98) * mm, "end": v(55.58, 94.68) * mm});
            skLineSegment(sketch, "E66.11.266.0", {"start": v(54.75, 92.22) * mm, "end": v(55.46, 93.31) * mm});
            skLineSegment(sketch, "E66.1.267.0", {"start": v(51.81, 93.9) * mm, "end": v(52.4, 95.07) * mm});
            skArc(sketch, "E66.3.267.0", {"start": v(53.51, 95.86) * mm, "mid": v(52.85, 95.6) * mm, "end": v(52.4, 95.07) * mm});
            skArc(sketch, "E66.7.267.0", {"start": v(53.43, 94.5) * mm, "mid": v(53.64, 95.16) * mm, "end": v(53.51, 95.86) * mm});
            skLineSegment(sketch, "E66.11.267.0", {"start": v(52.74, 93.38) * mm, "end": v(53.43, 94.5) * mm});
            skLineSegment(sketch, "E66.1.268.0", {"start": v(49.76, 95) * mm, "end": v(50.32, 96.18) * mm});
            skArc(sketch, "E66.3.268.0", {"start": v(51.42, 97) * mm, "mid": v(50.77, 96.73) * mm, "end": v(50.32, 96.18) * mm});
            skArc(sketch, "E66.7.268.0", {"start": v(51.37, 95.63) * mm, "mid": v(51.57, 96.3) * mm, "end": v(51.42, 97) * mm});
            skLineSegment(sketch, "E66.11.268.0", {"start": v(50.7, 94.5) * mm, "end": v(51.37, 95.63) * mm});
            skLineSegment(sketch, "E66.1.269.0", {"start": v(47.7, 96.06) * mm, "end": v(48.23, 97.25) * mm});
            skArc(sketch, "E66.3.269.0", {"start": v(49.31, 98.09) * mm, "mid": v(48.66, 97.8) * mm, "end": v(48.23, 97.25) * mm});
            skArc(sketch, "E66.7.269.0", {"start": v(49.29, 96.72) * mm, "mid": v(49.47, 97.4) * mm, "end": v(49.31, 98.09) * mm});
            skLineSegment(sketch, "E66.11.269.0", {"start": v(48.65, 95.58) * mm, "end": v(49.29, 96.72) * mm});
            skLineSegment(sketch, "E66.1.270.0", {"start": v(45.6, 97.07) * mm, "end": v(46.1, 98.27) * mm});
            skArc(sketch, "E66.3.270.0", {"start": v(47.17, 99.13) * mm, "mid": v(46.53, 98.84) * mm, "end": v(46.1, 98.27) * mm});
            skArc(sketch, "E66.7.270.0", {"start": v(47.18, 97.76) * mm, "mid": v(47.35, 98.45) * mm, "end": v(47.17, 99.13) * mm});
            skLineSegment(sketch, "E66.11.270.0", {"start": v(46.57, 96.61) * mm, "end": v(47.18, 97.76) * mm});
            skLineSegment(sketch, "E66.1.271.0", {"start": v(43.49, 98.04) * mm, "end": v(43.97, 99.25) * mm});
            skArc(sketch, "E66.3.271.0", {"start": v(45.02, 100.13) * mm, "mid": v(44.38, 99.82) * mm, "end": v(43.97, 99.25) * mm});
            skArc(sketch, "E66.7.271.0", {"start": v(45.05, 98.76) * mm, "mid": v(45.2, 99.45) * mm, "end": v(45.02, 100.13) * mm});
            skLineSegment(sketch, "E66.11.271.0", {"start": v(44.46, 97.6) * mm, "end": v(45.05, 98.76) * mm});
            skLineSegment(sketch, "E66.1.272.0", {"start": v(41.35, 98.96) * mm, "end": v(41.8, 100.18) * mm});
            skArc(sketch, "E66.3.272.0", {"start": v(42.84, 101.08) * mm, "mid": v(42.2, 100.76) * mm, "end": v(41.8, 100.18) * mm});
            skArc(sketch, "E66.7.272.0", {"start": v(42.9, 99.71) * mm, "mid": v(43.04, 100.4) * mm, "end": v(42.84, 101.08) * mm});
            skLineSegment(sketch, "E66.11.272.0", {"start": v(42.34, 98.54) * mm, "end": v(42.9, 99.71) * mm});
            skLineSegment(sketch, "E66.1.273.0", {"start": v(39.2, 99.83) * mm, "end": v(39.63, 101.06) * mm});
            skArc(sketch, "E66.3.273.0", {"start": v(40.64, 101.99) * mm, "mid": v(40.01, 101.65) * mm, "end": v(39.63, 101.06) * mm});
            skArc(sketch, "E66.7.273.0", {"start": v(40.73, 100.62) * mm, "mid": v(40.85, 101.32) * mm, "end": v(40.64, 101.99) * mm});
            skLineSegment(sketch, "E66.11.273.0", {"start": v(40.2, 99.43) * mm, "end": v(40.73, 100.62) * mm});
            skLineSegment(sketch, "E66.1.274.0", {"start": v(37.03, 100.65) * mm, "end": v(37.43, 101.9) * mm});
            skArc(sketch, "E66.3.274.0", {"start": v(38.42, 102.84) * mm, "mid": v(37.8, 102.5) * mm, "end": v(37.43, 101.9) * mm});
            skArc(sketch, "E66.7.274.0", {"start": v(38.54, 101.48) * mm, "mid": v(38.65, 102.18) * mm, "end": v(38.42, 102.84) * mm});
            skLineSegment(sketch, "E66.11.274.0", {"start": v(38.03, 100.28) * mm, "end": v(38.54, 101.48) * mm});
            skLineSegment(sketch, "E66.1.275.0", {"start": v(34.84, 101.43) * mm, "end": v(35.21, 102.68) * mm});
            skArc(sketch, "E66.3.275.0", {"start": v(36.18, 103.65) * mm, "mid": v(35.57, 103.29) * mm, "end": v(35.21, 102.68) * mm});
            skArc(sketch, "E66.7.275.0", {"start": v(36.33, 102.29) * mm, "mid": v(36.43, 103) * mm, "end": v(36.18, 103.65) * mm});
            skLineSegment(sketch, "E66.11.275.0", {"start": v(35.85, 101.08) * mm, "end": v(36.33, 102.29) * mm});
            skLineSegment(sketch, "E66.1.276.0", {"start": v(32.63, 102.16) * mm, "end": v(32.98, 103.42) * mm});
            skArc(sketch, "E66.3.276.0", {"start": v(33.93, 104.41) * mm, "mid": v(33.33, 104.03) * mm, "end": v(32.98, 103.42) * mm});
            skArc(sketch, "E66.7.276.0", {"start": v(34.1, 103.05) * mm, "mid": v(34.19, 103.76) * mm, "end": v(33.93, 104.41) * mm});
            skLineSegment(sketch, "E66.11.276.0", {"start": v(33.65, 101.83) * mm, "end": v(34.1, 103.05) * mm});
            skLineSegment(sketch, "E66.1.277.0", {"start": v(30.41, 102.85) * mm, "end": v(30.73, 104.1) * mm});
            skArc(sketch, "E66.3.277.0", {"start": v(31.66, 105.12) * mm, "mid": v(31.07, 104.73) * mm, "end": v(30.73, 104.1) * mm});
            skArc(sketch, "E66.7.277.0", {"start": v(31.87, 103.77) * mm, "mid": v(31.93, 104.47) * mm, "end": v(31.66, 105.12) * mm});
            skLineSegment(sketch, "E66.11.277.0", {"start": v(31.44, 102.54) * mm, "end": v(31.87, 103.77) * mm});
            skLineSegment(sketch, "E66.1.278.0", {"start": v(28.18, 103.48) * mm, "end": v(28.47, 104.75) * mm});
            skArc(sketch, "E66.3.278.0", {"start": v(29.37, 105.78) * mm, "mid": v(28.79, 105.38) * mm, "end": v(28.47, 104.75) * mm});
            skArc(sketch, "E66.7.278.0", {"start": v(29.61, 104.43) * mm, "mid": v(29.66, 105.14) * mm, "end": v(29.37, 105.78) * mm});
            skLineSegment(sketch, "E66.11.278.0", {"start": v(29.2, 103.2) * mm, "end": v(29.61, 104.43) * mm});
            skLineSegment(sketch, "E66.1.279.0", {"start": v(25.93, 104.07) * mm, "end": v(26.2, 105.34) * mm});
            skArc(sketch, "E66.3.279.0", {"start": v(27.07, 106.4) * mm, "mid": v(26.5, 105.98) * mm, "end": v(26.2, 105.34) * mm});
            skArc(sketch, "E66.7.279.0", {"start": v(27.34, 105.05) * mm, "mid": v(27.38, 105.76) * mm, "end": v(27.07, 106.4) * mm});
            skLineSegment(sketch, "E66.11.279.0", {"start": v(26.96, 103.8) * mm, "end": v(27.34, 105.05) * mm});
            skLineSegment(sketch, "E66.1.280.0", {"start": v(23.67, 104.6) * mm, "end": v(23.9, 105.89) * mm});
            skArc(sketch, "E66.3.280.0", {"start": v(24.76, 106.96) * mm, "mid": v(24.2, 106.53) * mm, "end": v(23.9, 105.89) * mm});
            skArc(sketch, "E66.7.280.0", {"start": v(25.06, 105.62) * mm, "mid": v(25.08, 106.33) * mm, "end": v(24.76, 106.96) * mm});
            skLineSegment(sketch, "E66.11.280.0", {"start": v(24.7, 104.36) * mm, "end": v(25.06, 105.62) * mm});
            skLineSegment(sketch, "E66.1.281.0", {"start": v(21.4, 105.1) * mm, "end": v(21.6, 106.38) * mm});
            skArc(sketch, "E66.3.281.0", {"start": v(22.44, 107.47) * mm, "mid": v(21.88, 107.03) * mm, "end": v(21.6, 106.38) * mm});
            skArc(sketch, "E66.7.281.0", {"start": v(22.77, 106.14) * mm, "mid": v(22.77, 106.84) * mm, "end": v(22.44, 107.47) * mm});
            skLineSegment(sketch, "E66.11.281.0", {"start": v(22.44, 104.88) * mm, "end": v(22.77, 106.14) * mm});
            skLineSegment(sketch, "E66.1.282.0", {"start": v(19.11, 105.53) * mm, "end": v(19.3, 106.82) * mm});
            skArc(sketch, "E66.3.282.0", {"start": v(20.1, 107.93) * mm, "mid": v(19.56, 107.48) * mm, "end": v(19.3, 106.82) * mm});
            skArc(sketch, "E66.7.282.0", {"start": v(20.46, 106.6) * mm, "mid": v(20.45, 107.31) * mm, "end": v(20.1, 107.93) * mm});
            skLineSegment(sketch, "E66.11.282.0", {"start": v(20.16, 105.34) * mm, "end": v(20.46, 106.6) * mm});
            skLineSegment(sketch, "E66.1.283.0", {"start": v(16.82, 105.92) * mm, "end": v(16.98, 107.22) * mm});
            skArc(sketch, "E66.3.283.0", {"start": v(17.76, 108.34) * mm, "mid": v(17.23, 107.88) * mm, "end": v(16.98, 107.22) * mm});
            skArc(sketch, "E66.7.283.0", {"start": v(18.15, 107.02) * mm, "mid": v(18.12, 107.73) * mm, "end": v(17.76, 108.34) * mm});
            skLineSegment(sketch, "E66.11.283.0", {"start": v(17.88, 105.75) * mm, "end": v(18.15, 107.02) * mm});
            skLineSegment(sketch, "E66.1.284.0", {"start": v(14.53, 106.26) * mm, "end": v(14.65, 107.56) * mm});
            skArc(sketch, "E66.3.284.0", {"start": v(15.4, 108.7) * mm, "mid": v(14.89, 108.22) * mm, "end": v(14.65, 107.56) * mm});
            skArc(sketch, "E66.7.284.0", {"start": v(15.82, 107.4) * mm, "mid": v(15.78, 108.1) * mm, "end": v(15.4, 108.7) * mm});
            skLineSegment(sketch, "E66.11.284.0", {"start": v(15.58, 106.11) * mm, "end": v(15.82, 107.4) * mm});
            skLineSegment(sketch, "E66.1.285.0", {"start": v(12.22, 106.55) * mm, "end": v(12.32, 107.85) * mm});
            skArc(sketch, "E66.3.285.0", {"start": v(13.05, 109) * mm, "mid": v(12.54, 108.52) * mm, "end": v(12.32, 107.85) * mm});
            skArc(sketch, "E66.7.285.0", {"start": v(13.5, 107.7) * mm, "mid": v(13.44, 108.41) * mm, "end": v(13.05, 109) * mm});
            skLineSegment(sketch, "E66.11.285.0", {"start": v(13.28, 106.42) * mm, "end": v(13.5, 107.7) * mm});
            skLineSegment(sketch, "E66.1.286.0", {"start": v(9.9, 106.8) * mm, "end": v(9.98, 108.1) * mm});
            skArc(sketch, "E66.3.286.0", {"start": v(10.69, 109.26) * mm, "mid": v(10.18, 108.77) * mm, "end": v(9.98, 108.1) * mm});
            skArc(sketch, "E66.7.286.0", {"start": v(11.16, 107.98) * mm, "mid": v(11.08, 108.68) * mm, "end": v(10.69, 109.26) * mm});
            skLineSegment(sketch, "E66.11.286.0", {"start": v(10.97, 106.69) * mm, "end": v(11.16, 107.98) * mm});
            skLineSegment(sketch, "E66.1.287.0", {"start": v(7.6, 106.98) * mm, "end": v(7.63, 108.28) * mm});
            skArc(sketch, "E66.3.287.0", {"start": v(8.32, 109.47) * mm, "mid": v(7.83, 108.96) * mm, "end": v(7.63, 108.28) * mm});
            skArc(sketch, "E66.7.287.0", {"start": v(8.82, 108.2) * mm, "mid": v(8.73, 108.9) * mm, "end": v(8.32, 109.47) * mm});
            skLineSegment(sketch, "E66.11.287.0", {"start": v(8.66, 106.9) * mm, "end": v(8.82, 108.2) * mm});
            skLineSegment(sketch, "E66.1.288.0", {"start": v(5.27, 107.12) * mm, "end": v(5.28, 108.42) * mm});
            skArc(sketch, "E66.3.288.0", {"start": v(5.94, 109.62) * mm, "mid": v(5.46, 109.1) * mm, "end": v(5.28, 108.42) * mm});
            skArc(sketch, "E66.7.288.0", {"start": v(6.47, 108.36) * mm, "mid": v(6.37, 109.06) * mm, "end": v(5.94, 109.62) * mm});
            skLineSegment(sketch, "E66.11.288.0", {"start": v(6.34, 107.06) * mm, "end": v(6.47, 108.36) * mm});
            skLineSegment(sketch, "E66.1.289.0", {"start": v(2.95, 107.2) * mm, "end": v(2.93, 108.51) * mm});
            skArc(sketch, "E66.3.289.0", {"start": v(3.57, 109.73) * mm, "mid": v(3.1, 109.2) * mm, "end": v(2.93, 108.51) * mm});
            skArc(sketch, "E66.7.289.0", {"start": v(4.12, 108.47) * mm, "mid": v(4, 109.17) * mm, "end": v(3.57, 109.73) * mm});
            skLineSegment(sketch, "E66.11.289.0", {"start": v(4.02, 107.17) * mm, "end": v(4.12, 108.47) * mm});
            skLineSegment(sketch, "E67", {"start": v(1.7, 107.24) * mm, "end": v(2.95, 107.2) * mm});
            skLineSegment(sketch, "E68.1.0", {"start": v(-0.63, 107.25) * mm, "end": v(0.63, 107.25) * mm});
            skLineSegment(sketch, "E68.2.0", {"start": v(-2.95, 107.2) * mm, "end": v(-1.7, 107.24) * mm});
            skLineSegment(sketch, "E69.1.3.0", {"start": v(-5.27, 107.12) * mm, "end": v(-4.02, 107.17) * mm});
            skLineSegment(sketch, "E69.1.4.0", {"start": v(-7.6, 106.98) * mm, "end": v(-6.34, 107.06) * mm});
            skLineSegment(sketch, "E69.1.5.0", {"start": v(-9.9, 106.8) * mm, "end": v(-8.66, 106.9) * mm});
            skLineSegment(sketch, "E69.1.6.0", {"start": v(-12.22, 106.55) * mm, "end": v(-10.97, 106.69) * mm});
            skLineSegment(sketch, "E69.1.7.0", {"start": v(-14.53, 106.26) * mm, "end": v(-13.28, 106.42) * mm});
            skLineSegment(sketch, "E69.1.8.0", {"start": v(-16.82, 105.92) * mm, "end": v(-15.58, 106.11) * mm});
            skLineSegment(sketch, "E69.1.9.0", {"start": v(-19.11, 105.53) * mm, "end": v(-17.88, 105.75) * mm});
            skLineSegment(sketch, "E69.1.10.0", {"start": v(-21.4, 105.1) * mm, "end": v(-20.16, 105.34) * mm});
            skLineSegment(sketch, "E69.1.11.0", {"start": v(-23.67, 104.6) * mm, "end": v(-22.44, 104.88) * mm});
            skLineSegment(sketch, "E69.1.12.0", {"start": v(-25.93, 104.07) * mm, "end": v(-24.7, 104.36) * mm});
            skLineSegment(sketch, "E69.1.13.0", {"start": v(-28.18, 103.48) * mm, "end": v(-26.96, 103.8) * mm});
            skLineSegment(sketch, "E69.1.14.0", {"start": v(-30.41, 102.85) * mm, "end": v(-29.2, 103.2) * mm});
            skLineSegment(sketch, "E69.1.15.0", {"start": v(-32.63, 102.16) * mm, "end": v(-31.44, 102.54) * mm});
            skLineSegment(sketch, "E69.1.16.0", {"start": v(-34.84, 101.43) * mm, "end": v(-33.65, 101.83) * mm});
            skLineSegment(sketch, "E69.1.17.0", {"start": v(-37.03, 100.65) * mm, "end": v(-35.85, 101.08) * mm});
            skLineSegment(sketch, "E69.1.18.0", {"start": v(-39.2, 99.83) * mm, "end": v(-38.03, 100.28) * mm});
            skLineSegment(sketch, "E69.1.19.0", {"start": v(-41.35, 98.96) * mm, "end": v(-40.2, 99.43) * mm});
            skLineSegment(sketch, "E69.1.20.0", {"start": v(-43.49, 98.04) * mm, "end": v(-42.34, 98.54) * mm});
            skLineSegment(sketch, "E69.1.21.0", {"start": v(-45.6, 97.07) * mm, "end": v(-44.46, 97.6) * mm});
            skLineSegment(sketch, "E69.1.22.0", {"start": v(-47.7, 96.06) * mm, "end": v(-46.57, 96.61) * mm});
            skLineSegment(sketch, "E69.1.23.0", {"start": v(-49.76, 95) * mm, "end": v(-48.65, 95.58) * mm});
            skLineSegment(sketch, "E69.1.24.0", {"start": v(-51.81, 93.9) * mm, "end": v(-50.7, 94.5) * mm});
            skLineSegment(sketch, "E69.1.25.0", {"start": v(-53.83, 92.76) * mm, "end": v(-52.74, 93.38) * mm});
            skLineSegment(sketch, "E69.1.26.0", {"start": v(-55.83, 91.57) * mm, "end": v(-54.75, 92.22) * mm});
            skLineSegment(sketch, "E69.1.27.0", {"start": v(-57.8, 90.34) * mm, "end": v(-56.74, 91.01) * mm});
            skLineSegment(sketch, "E69.1.28.0", {"start": v(-59.74, 89.07) * mm, "end": v(-58.7, 89.76) * mm});
            skLineSegment(sketch, "E69.1.29.0", {"start": v(-61.66, 87.75) * mm, "end": v(-60.63, 88.47) * mm});
            skLineSegment(sketch, "E69.1.30.0", {"start": v(-63.55, 86.4) * mm, "end": v(-62.53, 87.13) * mm});
            skLineSegment(sketch, "E69.1.31.0", {"start": v(-65.4, 85) * mm, "end": v(-64.4, 85.76) * mm});
            skLineSegment(sketch, "E69.1.32.0", {"start": v(-67.23, 83.56) * mm, "end": v(-66.25, 84.34) * mm});
            skLineSegment(sketch, "E69.1.33.0", {"start": v(-69.02, 82.09) * mm, "end": v(-68.06, 82.89) * mm});
            skLineSegment(sketch, "E69.1.34.0", {"start": v(-70.79, 80.57) * mm, "end": v(-69.84, 81.4) * mm});
            skLineSegment(sketch, "E69.1.35.0", {"start": v(-72.52, 79.02) * mm, "end": v(-71.59, 79.86) * mm});
            skLineSegment(sketch, "E69.1.36.0", {"start": v(-74.21, 77.43) * mm, "end": v(-73.3, 78.3) * mm});
            skLineSegment(sketch, "E69.1.37.0", {"start": v(-75.87, 75.8) * mm, "end": v(-74.98, 76.69) * mm});
            skLineSegment(sketch, "E69.1.38.0", {"start": v(-77.5, 74.14) * mm, "end": v(-76.62, 75.04) * mm});
            skLineSegment(sketch, "E69.1.39.0", {"start": v(-79.08, 72.45) * mm, "end": v(-78.23, 73.37) * mm});
            skLineSegment(sketch, "E69.1.40.0", {"start": v(-80.63, 70.72) * mm, "end": v(-79.8, 71.66) * mm});
            skLineSegment(sketch, "E69.1.41.0", {"start": v(-82.15, 68.95) * mm, "end": v(-81.33, 69.9) * mm});
            skLineSegment(sketch, "E69.1.42.0", {"start": v(-83.62, 67.16) * mm, "end": v(-82.83, 68.13) * mm});
            skLineSegment(sketch, "E69.1.43.0", {"start": v(-85.06, 65.33) * mm, "end": v(-84.29, 66.32) * mm});
            skLineSegment(sketch, "E69.1.44.0", {"start": v(-86.45, 63.47) * mm, "end": v(-85.7, 64.48) * mm});
            skLineSegment(sketch, "E69.1.45.0", {"start": v(-87.8, 61.58) * mm, "end": v(-87.08, 62.6) * mm});
            skLineSegment(sketch, "E69.1.46.0", {"start": v(-89.12, 59.67) * mm, "end": v(-88.42, 60.7) * mm});
            skLineSegment(sketch, "E69.1.47.0", {"start": v(-90.4, 57.72) * mm, "end": v(-89.71, 58.78) * mm});
            skLineSegment(sketch, "E69.1.48.0", {"start": v(-91.62, 55.75) * mm, "end": v(-90.96, 56.82) * mm});
            skLineSegment(sketch, "E69.1.49.0", {"start": v(-92.8, 53.75) * mm, "end": v(-92.17, 54.84) * mm});
            skLineSegment(sketch, "E69.1.50.0", {"start": v(-93.95, 51.73) * mm, "end": v(-93.34, 52.83) * mm});
            skLineSegment(sketch, "E69.1.51.0", {"start": v(-95.05, 49.68) * mm, "end": v(-94.46, 50.8) * mm});
            skLineSegment(sketch, "E69.1.52.0", {"start": v(-96.1, 47.61) * mm, "end": v(-95.54, 48.73) * mm});
            skLineSegment(sketch, "E69.1.53.0", {"start": v(-97.11, 45.52) * mm, "end": v(-96.57, 46.65) * mm});
            skLineSegment(sketch, "E69.1.54.0", {"start": v(-98.08, 43.4) * mm, "end": v(-97.56, 44.55) * mm});
            skLineSegment(sketch, "E69.1.55.0", {"start": v(-99, 41.27) * mm, "end": v(-98.5, 42.42) * mm});
            skLineSegment(sketch, "E69.1.56.0", {"start": v(-99.86, 39.11) * mm, "end": v(-99.4, 40.28) * mm});
            skLineSegment(sketch, "E69.1.57.0", {"start": v(-100.69, 36.94) * mm, "end": v(-100.25, 38.12) * mm});
            skLineSegment(sketch, "E69.1.58.0", {"start": v(-101.46, 34.75) * mm, "end": v(-101.05, 35.94) * mm});
            skLineSegment(sketch, "E69.1.59.0", {"start": v(-102.2, 32.54) * mm, "end": v(-101.8, 33.74) * mm});
            skLineSegment(sketch, "E69.1.60.0", {"start": v(-102.87, 30.32) * mm, "end": v(-102.51, 31.53) * mm});
            skLineSegment(sketch, "E69.1.61.0", {"start": v(-103.5, 28.09) * mm, "end": v(-103.17, 29.3) * mm});
            skLineSegment(sketch, "E69.1.62.0", {"start": v(-104.1, 25.84) * mm, "end": v(-103.78, 27.06) * mm});
            skLineSegment(sketch, "E69.1.63.0", {"start": v(-104.63, 23.58) * mm, "end": v(-104.34, 24.8) * mm});
            skLineSegment(sketch, "E69.1.64.0", {"start": v(-105.11, 21.3) * mm, "end": v(-104.86, 22.53) * mm});
            skLineSegment(sketch, "E69.1.65.0", {"start": v(-105.55, 19.02) * mm, "end": v(-105.32, 20.26) * mm});
            skLineSegment(sketch, "E69.1.66.0", {"start": v(-105.94, 16.73) * mm, "end": v(-105.73, 17.97) * mm});
            skLineSegment(sketch, "E69.1.67.0", {"start": v(-106.27, 14.43) * mm, "end": v(-106.1, 15.68) * mm});
            skLineSegment(sketch, "E69.1.68.0", {"start": v(-106.56, 12.13) * mm, "end": v(-106.41, 13.37) * mm});
            skLineSegment(sketch, "E69.1.69.0", {"start": v(-106.8, 9.81) * mm, "end": v(-106.68, 11.06) * mm});
            skLineSegment(sketch, "E69.1.70.0", {"start": v(-106.99, 7.5) * mm, "end": v(-106.9, 8.75) * mm});
            skLineSegment(sketch, "E69.1.71.0", {"start": v(-107.12, 5.18) * mm, "end": v(-107.06, 6.43) * mm});
            skLineSegment(sketch, "E69.1.72.0", {"start": v(-107.21, 2.86) * mm, "end": v(-107.17, 4.11) * mm});
            skLineSegment(sketch, "E69.1.73.0", {"start": v(-107.25, 0.53) * mm, "end": v(-107.24, 1.79) * mm});
            skLineSegment(sketch, "E69.1.74.0", {"start": v(-107.24, -1.79) * mm, "end": v(-107.25, -0.53) * mm});
            skLineSegment(sketch, "E69.1.75.0", {"start": v(-107.17, -4.11) * mm, "end": v(-107.21, -2.86) * mm});
            skLineSegment(sketch, "E69.1.76.0", {"start": v(-107.06, -6.43) * mm, "end": v(-107.12, -5.18) * mm});
            skLineSegment(sketch, "E69.1.77.0", {"start": v(-106.9, -8.75) * mm, "end": v(-106.99, -7.5) * mm});
            skLineSegment(sketch, "E69.1.78.0", {"start": v(-106.68, -11.06) * mm, "end": v(-106.8, -9.81) * mm});
            skLineSegment(sketch, "E69.1.79.0", {"start": v(-106.41, -13.37) * mm, "end": v(-106.56, -12.13) * mm});
            skLineSegment(sketch, "E69.1.80.0", {"start": v(-106.1, -15.68) * mm, "end": v(-106.27, -14.43) * mm});
            skLineSegment(sketch, "E69.1.81.0", {"start": v(-105.73, -17.97) * mm, "end": v(-105.94, -16.73) * mm});
            skLineSegment(sketch, "E69.1.82.0", {"start": v(-105.32, -20.26) * mm, "end": v(-105.55, -19.02) * mm});
            skLineSegment(sketch, "E69.1.83.0", {"start": v(-104.86, -22.53) * mm, "end": v(-105.11, -21.3) * mm});
            skLineSegment(sketch, "E69.1.84.0", {"start": v(-104.34, -24.8) * mm, "end": v(-104.63, -23.58) * mm});
            skLineSegment(sketch, "E69.1.85.0", {"start": v(-103.78, -27.06) * mm, "end": v(-104.1, -25.84) * mm});
            skLineSegment(sketch, "E69.1.86.0", {"start": v(-103.17, -29.3) * mm, "end": v(-103.5, -28.09) * mm});
            skLineSegment(sketch, "E69.1.87.0", {"start": v(-102.51, -31.53) * mm, "end": v(-102.87, -30.32) * mm});
            skLineSegment(sketch, "E69.1.88.0", {"start": v(-101.8, -33.74) * mm, "end": v(-102.2, -32.54) * mm});
            skLineSegment(sketch, "E69.1.89.0", {"start": v(-101.05, -35.94) * mm, "end": v(-101.46, -34.75) * mm});
            skLineSegment(sketch, "E69.1.90.0", {"start": v(-100.25, -38.12) * mm, "end": v(-100.69, -36.94) * mm});
            skLineSegment(sketch, "E69.1.91.0", {"start": v(-99.4, -40.28) * mm, "end": v(-99.86, -39.11) * mm});
            skLineSegment(sketch, "E69.1.92.0", {"start": v(-98.5, -42.42) * mm, "end": v(-99, -41.27) * mm});
            skLineSegment(sketch, "E69.1.93.0", {"start": v(-97.56, -44.55) * mm, "end": v(-98.08, -43.4) * mm});
            skLineSegment(sketch, "E69.1.94.0", {"start": v(-96.57, -46.65) * mm, "end": v(-97.11, -45.52) * mm});
            skLineSegment(sketch, "E69.1.95.0", {"start": v(-95.54, -48.73) * mm, "end": v(-96.1, -47.61) * mm});
            skLineSegment(sketch, "E69.1.96.0", {"start": v(-94.46, -50.8) * mm, "end": v(-95.05, -49.68) * mm});
            skLineSegment(sketch, "E69.1.97.0", {"start": v(-93.34, -52.83) * mm, "end": v(-93.95, -51.73) * mm});
            skLineSegment(sketch, "E69.1.98.0", {"start": v(-92.17, -54.84) * mm, "end": v(-92.8, -53.75) * mm});
            skLineSegment(sketch, "E69.1.99.0", {"start": v(-90.96, -56.82) * mm, "end": v(-91.62, -55.75) * mm});
            skLineSegment(sketch, "E69.1.100.0", {"start": v(-89.71, -58.78) * mm, "end": v(-90.4, -57.72) * mm});
            skLineSegment(sketch, "E69.1.101.0", {"start": v(-88.42, -60.7) * mm, "end": v(-89.12, -59.67) * mm});
            skLineSegment(sketch, "E69.1.102.0", {"start": v(-87.08, -62.6) * mm, "end": v(-87.8, -61.58) * mm});
            skLineSegment(sketch, "E69.1.103.0", {"start": v(-85.7, -64.48) * mm, "end": v(-86.45, -63.47) * mm});
            skLineSegment(sketch, "E69.1.104.0", {"start": v(-84.29, -66.32) * mm, "end": v(-85.06, -65.33) * mm});
            skLineSegment(sketch, "E69.1.105.0", {"start": v(-82.83, -68.13) * mm, "end": v(-83.62, -67.16) * mm});
            skLineSegment(sketch, "E69.1.106.0", {"start": v(-81.33, -69.9) * mm, "end": v(-82.15, -68.95) * mm});
            skLineSegment(sketch, "E69.1.107.0", {"start": v(-79.8, -71.66) * mm, "end": v(-80.63, -70.72) * mm});
            skLineSegment(sketch, "E69.1.108.0", {"start": v(-78.23, -73.37) * mm, "end": v(-79.08, -72.45) * mm});
            skLineSegment(sketch, "E69.1.109.0", {"start": v(-76.62, -75.04) * mm, "end": v(-77.5, -74.14) * mm});
            skLineSegment(sketch, "E69.1.110.0", {"start": v(-74.98, -76.69) * mm, "end": v(-75.87, -75.8) * mm});
            skLineSegment(sketch, "E69.1.111.0", {"start": v(-73.3, -78.3) * mm, "end": v(-74.21, -77.43) * mm});
            skLineSegment(sketch, "E69.1.112.0", {"start": v(-71.59, -79.86) * mm, "end": v(-72.52, -79.02) * mm});
            skLineSegment(sketch, "E69.1.113.0", {"start": v(-69.84, -81.4) * mm, "end": v(-70.79, -80.57) * mm});
            skLineSegment(sketch, "E69.1.114.0", {"start": v(-68.06, -82.89) * mm, "end": v(-69.02, -82.09) * mm});
            skLineSegment(sketch, "E69.1.115.0", {"start": v(-66.25, -84.34) * mm, "end": v(-67.23, -83.56) * mm});
            skLineSegment(sketch, "E69.1.116.0", {"start": v(-64.4, -85.76) * mm, "end": v(-65.4, -85) * mm});
            skLineSegment(sketch, "E69.1.117.0", {"start": v(-62.53, -87.13) * mm, "end": v(-63.55, -86.4) * mm});
            skLineSegment(sketch, "E69.1.118.0", {"start": v(-60.63, -88.47) * mm, "end": v(-61.66, -87.75) * mm});
            skLineSegment(sketch, "E69.1.119.0", {"start": v(-58.7, -89.76) * mm, "end": v(-59.74, -89.07) * mm});
            skLineSegment(sketch, "E69.1.120.0", {"start": v(-56.74, -91.01) * mm, "end": v(-57.8, -90.34) * mm});
            skLineSegment(sketch, "E69.1.121.0", {"start": v(-54.75, -92.22) * mm, "end": v(-55.83, -91.57) * mm});
            skLineSegment(sketch, "E69.1.122.0", {"start": v(-52.74, -93.38) * mm, "end": v(-53.83, -92.76) * mm});
            skLineSegment(sketch, "E69.1.123.0", {"start": v(-50.7, -94.5) * mm, "end": v(-51.81, -93.9) * mm});
            skLineSegment(sketch, "E69.1.124.0", {"start": v(-48.65, -95.58) * mm, "end": v(-49.76, -95) * mm});
            skLineSegment(sketch, "E69.1.125.0", {"start": v(-46.57, -96.61) * mm, "end": v(-47.7, -96.06) * mm});
            skLineSegment(sketch, "E69.1.126.0", {"start": v(-44.46, -97.6) * mm, "end": v(-45.6, -97.07) * mm});
            skLineSegment(sketch, "E69.1.127.0", {"start": v(-42.34, -98.54) * mm, "end": v(-43.49, -98.04) * mm});
            skLineSegment(sketch, "E69.1.128.0", {"start": v(-40.2, -99.43) * mm, "end": v(-41.35, -98.96) * mm});
            skLineSegment(sketch, "E69.1.129.0", {"start": v(-38.03, -100.28) * mm, "end": v(-39.2, -99.83) * mm});
            skLineSegment(sketch, "E69.1.130.0", {"start": v(-35.85, -101.08) * mm, "end": v(-37.03, -100.65) * mm});
            skLineSegment(sketch, "E69.1.131.0", {"start": v(-33.65, -101.83) * mm, "end": v(-34.84, -101.43) * mm});
            skLineSegment(sketch, "E69.1.132.0", {"start": v(-31.44, -102.54) * mm, "end": v(-32.63, -102.16) * mm});
            skLineSegment(sketch, "E69.1.133.0", {"start": v(-29.2, -103.2) * mm, "end": v(-30.41, -102.85) * mm});
            skLineSegment(sketch, "E69.1.134.0", {"start": v(-26.96, -103.8) * mm, "end": v(-28.18, -103.48) * mm});
            skLineSegment(sketch, "E69.1.135.0", {"start": v(-24.7, -104.36) * mm, "end": v(-25.93, -104.07) * mm});
            skLineSegment(sketch, "E69.1.136.0", {"start": v(-22.44, -104.88) * mm, "end": v(-23.67, -104.6) * mm});
            skLineSegment(sketch, "E69.1.137.0", {"start": v(-20.16, -105.34) * mm, "end": v(-21.4, -105.1) * mm});
            skLineSegment(sketch, "E69.1.138.0", {"start": v(-17.88, -105.75) * mm, "end": v(-19.11, -105.53) * mm});
            skLineSegment(sketch, "E69.1.139.0", {"start": v(-15.58, -106.11) * mm, "end": v(-16.82, -105.92) * mm});
            skLineSegment(sketch, "E69.1.140.0", {"start": v(-13.28, -106.42) * mm, "end": v(-14.53, -106.26) * mm});
            skLineSegment(sketch, "E69.1.141.0", {"start": v(-10.97, -106.69) * mm, "end": v(-12.22, -106.55) * mm});
            skLineSegment(sketch, "E69.1.142.0", {"start": v(-8.66, -106.9) * mm, "end": v(-9.9, -106.8) * mm});
            skLineSegment(sketch, "E69.1.143.0", {"start": v(-6.34, -107.06) * mm, "end": v(-7.6, -106.98) * mm});
            skLineSegment(sketch, "E69.1.144.0", {"start": v(-4.02, -107.17) * mm, "end": v(-5.27, -107.12) * mm});
            skLineSegment(sketch, "E69.1.145.0", {"start": v(-1.7, -107.24) * mm, "end": v(-2.95, -107.2) * mm});
            skLineSegment(sketch, "E69.1.146.0", {"start": v(0.63, -107.25) * mm, "end": v(-0.63, -107.25) * mm});
            skLineSegment(sketch, "E69.1.147.0", {"start": v(2.95, -107.2) * mm, "end": v(1.7, -107.24) * mm});
            skLineSegment(sketch, "E69.1.148.0", {"start": v(5.27, -107.12) * mm, "end": v(4.02, -107.17) * mm});
            skLineSegment(sketch, "E69.1.149.0", {"start": v(7.6, -106.98) * mm, "end": v(6.34, -107.06) * mm});
            skLineSegment(sketch, "E69.1.150.0", {"start": v(9.9, -106.8) * mm, "end": v(8.66, -106.9) * mm});
            skLineSegment(sketch, "E69.1.151.0", {"start": v(12.22, -106.55) * mm, "end": v(10.97, -106.69) * mm});
            skLineSegment(sketch, "E69.1.152.0", {"start": v(14.53, -106.26) * mm, "end": v(13.28, -106.42) * mm});
            skLineSegment(sketch, "E69.1.153.0", {"start": v(16.82, -105.92) * mm, "end": v(15.58, -106.11) * mm});
            skLineSegment(sketch, "E69.1.154.0", {"start": v(19.11, -105.53) * mm, "end": v(17.88, -105.75) * mm});
            skLineSegment(sketch, "E69.1.155.0", {"start": v(21.4, -105.1) * mm, "end": v(20.16, -105.34) * mm});
            skLineSegment(sketch, "E69.1.156.0", {"start": v(23.67, -104.6) * mm, "end": v(22.44, -104.88) * mm});
            skLineSegment(sketch, "E69.1.157.0", {"start": v(25.93, -104.07) * mm, "end": v(24.7, -104.36) * mm});
            skLineSegment(sketch, "E69.1.158.0", {"start": v(28.18, -103.48) * mm, "end": v(26.96, -103.8) * mm});
            skLineSegment(sketch, "E69.1.159.0", {"start": v(30.41, -102.85) * mm, "end": v(29.2, -103.2) * mm});
            skLineSegment(sketch, "E69.1.160.0", {"start": v(32.63, -102.16) * mm, "end": v(31.44, -102.54) * mm});
            skLineSegment(sketch, "E69.1.161.0", {"start": v(34.84, -101.43) * mm, "end": v(33.65, -101.83) * mm});
            skLineSegment(sketch, "E69.1.162.0", {"start": v(37.03, -100.65) * mm, "end": v(35.85, -101.08) * mm});
            skLineSegment(sketch, "E69.1.163.0", {"start": v(39.2, -99.83) * mm, "end": v(38.03, -100.28) * mm});
            skLineSegment(sketch, "E69.1.164.0", {"start": v(41.35, -98.96) * mm, "end": v(40.2, -99.43) * mm});
            skLineSegment(sketch, "E69.1.165.0", {"start": v(43.49, -98.04) * mm, "end": v(42.34, -98.54) * mm});
            skLineSegment(sketch, "E69.1.166.0", {"start": v(45.6, -97.07) * mm, "end": v(44.46, -97.6) * mm});
            skLineSegment(sketch, "E69.1.167.0", {"start": v(47.7, -96.06) * mm, "end": v(46.57, -96.61) * mm});
            skLineSegment(sketch, "E69.1.168.0", {"start": v(49.76, -95) * mm, "end": v(48.65, -95.58) * mm});
            skLineSegment(sketch, "E69.1.169.0", {"start": v(51.81, -93.9) * mm, "end": v(50.7, -94.5) * mm});
            skLineSegment(sketch, "E69.1.170.0", {"start": v(53.83, -92.76) * mm, "end": v(52.74, -93.38) * mm});
            skLineSegment(sketch, "E69.1.171.0", {"start": v(55.83, -91.57) * mm, "end": v(54.75, -92.22) * mm});
            skLineSegment(sketch, "E69.1.172.0", {"start": v(57.8, -90.34) * mm, "end": v(56.74, -91.01) * mm});
            skLineSegment(sketch, "E69.1.173.0", {"start": v(59.74, -89.07) * mm, "end": v(58.7, -89.76) * mm});
            skLineSegment(sketch, "E69.1.174.0", {"start": v(61.66, -87.75) * mm, "end": v(60.63, -88.47) * mm});
            skLineSegment(sketch, "E69.1.175.0", {"start": v(63.55, -86.4) * mm, "end": v(62.53, -87.13) * mm});
            skLineSegment(sketch, "E69.1.176.0", {"start": v(65.4, -85) * mm, "end": v(64.4, -85.76) * mm});
            skLineSegment(sketch, "E69.1.177.0", {"start": v(67.23, -83.56) * mm, "end": v(66.25, -84.34) * mm});
            skLineSegment(sketch, "E69.1.178.0", {"start": v(69.02, -82.09) * mm, "end": v(68.06, -82.89) * mm});
            skLineSegment(sketch, "E69.1.179.0", {"start": v(70.79, -80.57) * mm, "end": v(69.84, -81.4) * mm});
            skLineSegment(sketch, "E69.1.180.0", {"start": v(72.52, -79.02) * mm, "end": v(71.59, -79.86) * mm});
            skLineSegment(sketch, "E69.1.181.0", {"start": v(74.21, -77.43) * mm, "end": v(73.3, -78.3) * mm});
            skLineSegment(sketch, "E69.1.182.0", {"start": v(75.87, -75.8) * mm, "end": v(74.98, -76.69) * mm});
            skLineSegment(sketch, "E69.1.183.0", {"start": v(77.5, -74.14) * mm, "end": v(76.62, -75.04) * mm});
            skLineSegment(sketch, "E69.1.184.0", {"start": v(79.08, -72.45) * mm, "end": v(78.23, -73.37) * mm});
            skLineSegment(sketch, "E69.1.185.0", {"start": v(80.63, -70.72) * mm, "end": v(79.8, -71.66) * mm});
            skLineSegment(sketch, "E69.1.186.0", {"start": v(82.15, -68.95) * mm, "end": v(81.33, -69.9) * mm});
            skLineSegment(sketch, "E69.1.187.0", {"start": v(83.62, -67.16) * mm, "end": v(82.83, -68.13) * mm});
            skLineSegment(sketch, "E69.1.188.0", {"start": v(85.06, -65.33) * mm, "end": v(84.29, -66.32) * mm});
            skLineSegment(sketch, "E69.1.189.0", {"start": v(86.45, -63.47) * mm, "end": v(85.7, -64.48) * mm});
            skLineSegment(sketch, "E69.1.190.0", {"start": v(87.8, -61.58) * mm, "end": v(87.08, -62.6) * mm});
            skLineSegment(sketch, "E69.1.191.0", {"start": v(89.12, -59.67) * mm, "end": v(88.42, -60.7) * mm});
            skLineSegment(sketch, "E69.1.192.0", {"start": v(90.4, -57.72) * mm, "end": v(89.71, -58.78) * mm});
            skLineSegment(sketch, "E69.1.193.0", {"start": v(91.62, -55.75) * mm, "end": v(90.96, -56.82) * mm});
            skLineSegment(sketch, "E69.1.194.0", {"start": v(92.8, -53.75) * mm, "end": v(92.17, -54.84) * mm});
            skLineSegment(sketch, "E69.1.195.0", {"start": v(93.95, -51.73) * mm, "end": v(93.34, -52.83) * mm});
            skLineSegment(sketch, "E69.1.196.0", {"start": v(95.05, -49.68) * mm, "end": v(94.46, -50.8) * mm});
            skLineSegment(sketch, "E69.1.197.0", {"start": v(96.1, -47.61) * mm, "end": v(95.54, -48.73) * mm});
            skLineSegment(sketch, "E69.1.198.0", {"start": v(97.11, -45.52) * mm, "end": v(96.57, -46.65) * mm});
            skLineSegment(sketch, "E69.1.199.0", {"start": v(98.08, -43.4) * mm, "end": v(97.56, -44.55) * mm});
            skLineSegment(sketch, "E69.1.200.0", {"start": v(99, -41.27) * mm, "end": v(98.5, -42.42) * mm});
            skLineSegment(sketch, "E69.1.201.0", {"start": v(99.86, -39.11) * mm, "end": v(99.4, -40.28) * mm});
            skLineSegment(sketch, "E69.1.202.0", {"start": v(100.69, -36.94) * mm, "end": v(100.25, -38.12) * mm});
            skLineSegment(sketch, "E69.1.203.0", {"start": v(101.46, -34.75) * mm, "end": v(101.05, -35.94) * mm});
            skLineSegment(sketch, "E69.1.204.0", {"start": v(102.2, -32.54) * mm, "end": v(101.8, -33.74) * mm});
            skLineSegment(sketch, "E69.1.205.0", {"start": v(102.87, -30.32) * mm, "end": v(102.51, -31.53) * mm});
            skLineSegment(sketch, "E69.1.206.0", {"start": v(103.5, -28.09) * mm, "end": v(103.17, -29.3) * mm});
            skLineSegment(sketch, "E69.1.207.0", {"start": v(104.1, -25.84) * mm, "end": v(103.78, -27.06) * mm});
            skLineSegment(sketch, "E69.1.208.0", {"start": v(104.63, -23.58) * mm, "end": v(104.34, -24.8) * mm});
            skLineSegment(sketch, "E69.1.209.0", {"start": v(105.11, -21.3) * mm, "end": v(104.86, -22.53) * mm});
            skLineSegment(sketch, "E69.1.210.0", {"start": v(105.55, -19.02) * mm, "end": v(105.32, -20.26) * mm});
            skLineSegment(sketch, "E69.1.211.0", {"start": v(105.94, -16.73) * mm, "end": v(105.73, -17.97) * mm});
            skLineSegment(sketch, "E69.1.212.0", {"start": v(106.27, -14.43) * mm, "end": v(106.1, -15.68) * mm});
            skLineSegment(sketch, "E69.1.213.0", {"start": v(106.56, -12.13) * mm, "end": v(106.41, -13.37) * mm});
            skLineSegment(sketch, "E69.1.214.0", {"start": v(106.8, -9.81) * mm, "end": v(106.68, -11.06) * mm});
            skLineSegment(sketch, "E69.1.215.0", {"start": v(106.99, -7.5) * mm, "end": v(106.9, -8.75) * mm});
            skLineSegment(sketch, "E69.1.216.0", {"start": v(107.12, -5.18) * mm, "end": v(107.06, -6.43) * mm});
            skLineSegment(sketch, "E69.1.217.0", {"start": v(107.21, -2.86) * mm, "end": v(107.17, -4.11) * mm});
            skLineSegment(sketch, "E69.1.218.0", {"start": v(107.25, -0.53) * mm, "end": v(107.24, -1.79) * mm});
            skLineSegment(sketch, "E69.1.219.0", {"start": v(107.24, 1.79) * mm, "end": v(107.25, 0.53) * mm});
            skLineSegment(sketch, "E69.1.220.0", {"start": v(107.17, 4.11) * mm, "end": v(107.21, 2.86) * mm});
            skLineSegment(sketch, "E69.1.221.0", {"start": v(107.06, 6.43) * mm, "end": v(107.12, 5.18) * mm});
            skLineSegment(sketch, "E69.1.222.0", {"start": v(106.9, 8.75) * mm, "end": v(106.99, 7.5) * mm});
            skLineSegment(sketch, "E69.1.223.0", {"start": v(106.68, 11.06) * mm, "end": v(106.8, 9.81) * mm});
            skLineSegment(sketch, "E69.1.224.0", {"start": v(106.41, 13.37) * mm, "end": v(106.56, 12.13) * mm});
            skLineSegment(sketch, "E69.1.225.0", {"start": v(106.1, 15.68) * mm, "end": v(106.27, 14.43) * mm});
            skLineSegment(sketch, "E69.1.226.0", {"start": v(105.73, 17.97) * mm, "end": v(105.94, 16.73) * mm});
            skLineSegment(sketch, "E69.1.227.0", {"start": v(105.32, 20.26) * mm, "end": v(105.55, 19.02) * mm});
            skLineSegment(sketch, "E69.1.228.0", {"start": v(104.86, 22.53) * mm, "end": v(105.11, 21.3) * mm});
            skLineSegment(sketch, "E69.1.229.0", {"start": v(104.34, 24.8) * mm, "end": v(104.63, 23.58) * mm});
            skLineSegment(sketch, "E69.1.230.0", {"start": v(103.78, 27.06) * mm, "end": v(104.1, 25.84) * mm});
            skLineSegment(sketch, "E69.1.231.0", {"start": v(103.17, 29.3) * mm, "end": v(103.5, 28.09) * mm});
            skLineSegment(sketch, "E69.1.232.0", {"start": v(102.51, 31.53) * mm, "end": v(102.87, 30.32) * mm});
            skLineSegment(sketch, "E69.1.233.0", {"start": v(101.8, 33.74) * mm, "end": v(102.2, 32.54) * mm});
            skLineSegment(sketch, "E69.1.234.0", {"start": v(101.05, 35.94) * mm, "end": v(101.46, 34.75) * mm});
            skLineSegment(sketch, "E69.1.235.0", {"start": v(100.25, 38.12) * mm, "end": v(100.69, 36.94) * mm});
            skLineSegment(sketch, "E69.1.236.0", {"start": v(99.4, 40.28) * mm, "end": v(99.86, 39.11) * mm});
            skLineSegment(sketch, "E69.1.237.0", {"start": v(98.5, 42.42) * mm, "end": v(99, 41.27) * mm});
            skLineSegment(sketch, "E69.1.238.0", {"start": v(97.56, 44.55) * mm, "end": v(98.08, 43.4) * mm});
            skLineSegment(sketch, "E69.1.239.0", {"start": v(96.57, 46.65) * mm, "end": v(97.11, 45.52) * mm});
            skLineSegment(sketch, "E69.1.240.0", {"start": v(95.54, 48.73) * mm, "end": v(96.1, 47.61) * mm});
            skLineSegment(sketch, "E69.1.241.0", {"start": v(94.46, 50.8) * mm, "end": v(95.05, 49.68) * mm});
            skLineSegment(sketch, "E69.1.242.0", {"start": v(93.34, 52.83) * mm, "end": v(93.95, 51.73) * mm});
            skLineSegment(sketch, "E69.1.243.0", {"start": v(92.17, 54.84) * mm, "end": v(92.8, 53.75) * mm});
            skLineSegment(sketch, "E69.1.244.0", {"start": v(90.96, 56.82) * mm, "end": v(91.62, 55.75) * mm});
            skLineSegment(sketch, "E69.1.245.0", {"start": v(89.71, 58.78) * mm, "end": v(90.4, 57.72) * mm});
            skLineSegment(sketch, "E69.1.246.0", {"start": v(88.42, 60.7) * mm, "end": v(89.12, 59.67) * mm});
            skLineSegment(sketch, "E69.1.247.0", {"start": v(87.08, 62.6) * mm, "end": v(87.8, 61.58) * mm});
            skLineSegment(sketch, "E69.1.248.0", {"start": v(85.7, 64.48) * mm, "end": v(86.45, 63.47) * mm});
            skLineSegment(sketch, "E69.1.249.0", {"start": v(84.29, 66.32) * mm, "end": v(85.06, 65.33) * mm});
            skLineSegment(sketch, "E69.1.250.0", {"start": v(82.83, 68.13) * mm, "end": v(83.62, 67.16) * mm});
            skLineSegment(sketch, "E69.1.251.0", {"start": v(81.33, 69.9) * mm, "end": v(82.15, 68.95) * mm});
            skLineSegment(sketch, "E69.1.252.0", {"start": v(79.8, 71.66) * mm, "end": v(80.63, 70.72) * mm});
            skLineSegment(sketch, "E69.1.253.0", {"start": v(78.23, 73.37) * mm, "end": v(79.08, 72.45) * mm});
            skLineSegment(sketch, "E69.1.254.0", {"start": v(76.62, 75.04) * mm, "end": v(77.5, 74.14) * mm});
            skLineSegment(sketch, "E69.1.255.0", {"start": v(74.98, 76.69) * mm, "end": v(75.87, 75.8) * mm});
            skLineSegment(sketch, "E69.1.256.0", {"start": v(73.3, 78.3) * mm, "end": v(74.21, 77.43) * mm});
            skLineSegment(sketch, "E69.1.257.0", {"start": v(71.59, 79.86) * mm, "end": v(72.52, 79.02) * mm});
            skLineSegment(sketch, "E69.1.258.0", {"start": v(69.84, 81.4) * mm, "end": v(70.79, 80.57) * mm});
            skLineSegment(sketch, "E69.1.259.0", {"start": v(68.06, 82.89) * mm, "end": v(69.02, 82.09) * mm});
            skLineSegment(sketch, "E69.1.260.0", {"start": v(66.25, 84.34) * mm, "end": v(67.23, 83.56) * mm});
            skLineSegment(sketch, "E69.1.261.0", {"start": v(64.4, 85.76) * mm, "end": v(65.4, 85) * mm});
            skLineSegment(sketch, "E69.1.262.0", {"start": v(62.53, 87.13) * mm, "end": v(63.55, 86.4) * mm});
            skLineSegment(sketch, "E69.1.263.0", {"start": v(60.63, 88.47) * mm, "end": v(61.66, 87.75) * mm});
            skLineSegment(sketch, "E69.1.264.0", {"start": v(58.7, 89.76) * mm, "end": v(59.74, 89.07) * mm});
            skLineSegment(sketch, "E69.1.265.0", {"start": v(56.74, 91.01) * mm, "end": v(57.8, 90.34) * mm});
            skLineSegment(sketch, "E69.1.266.0", {"start": v(54.75, 92.22) * mm, "end": v(55.83, 91.57) * mm});
            skLineSegment(sketch, "E69.1.267.0", {"start": v(52.74, 93.38) * mm, "end": v(53.83, 92.76) * mm});
            skLineSegment(sketch, "E69.1.268.0", {"start": v(50.7, 94.5) * mm, "end": v(51.81, 93.9) * mm});
            skLineSegment(sketch, "E69.1.269.0", {"start": v(48.65, 95.58) * mm, "end": v(49.76, 95) * mm});
            skLineSegment(sketch, "E69.1.270.0", {"start": v(46.57, 96.61) * mm, "end": v(47.7, 96.06) * mm});
            skLineSegment(sketch, "E69.1.271.0", {"start": v(44.46, 97.6) * mm, "end": v(45.6, 97.07) * mm});
            skLineSegment(sketch, "E69.1.272.0", {"start": v(42.34, 98.54) * mm, "end": v(43.49, 98.04) * mm});
            skLineSegment(sketch, "E69.1.273.0", {"start": v(40.2, 99.43) * mm, "end": v(41.35, 98.96) * mm});
            skLineSegment(sketch, "E69.1.274.0", {"start": v(38.03, 100.28) * mm, "end": v(39.2, 99.83) * mm});
            skLineSegment(sketch, "E69.1.275.0", {"start": v(35.85, 101.08) * mm, "end": v(37.03, 100.65) * mm});
            skLineSegment(sketch, "E69.1.276.0", {"start": v(33.65, 101.83) * mm, "end": v(34.84, 101.43) * mm});
            skLineSegment(sketch, "E69.1.277.0", {"start": v(31.44, 102.54) * mm, "end": v(32.63, 102.16) * mm});
            skLineSegment(sketch, "E69.1.278.0", {"start": v(29.2, 103.2) * mm, "end": v(30.41, 102.85) * mm});
            skLineSegment(sketch, "E69.1.279.0", {"start": v(26.96, 103.8) * mm, "end": v(28.18, 103.48) * mm});
            skLineSegment(sketch, "E69.1.280.0", {"start": v(24.7, 104.36) * mm, "end": v(25.93, 104.07) * mm});
            skLineSegment(sketch, "E69.1.281.0", {"start": v(22.44, 104.88) * mm, "end": v(23.67, 104.6) * mm});
            skLineSegment(sketch, "E69.1.282.0", {"start": v(20.16, 105.34) * mm, "end": v(21.4, 105.1) * mm});
            skLineSegment(sketch, "E69.1.283.0", {"start": v(17.88, 105.75) * mm, "end": v(19.11, 105.53) * mm});
            skLineSegment(sketch, "E69.1.284.0", {"start": v(15.58, 106.11) * mm, "end": v(16.82, 105.92) * mm});
            skLineSegment(sketch, "E69.1.285.0", {"start": v(13.28, 106.42) * mm, "end": v(14.53, 106.26) * mm});
            skLineSegment(sketch, "E69.1.286.0", {"start": v(10.97, 106.69) * mm, "end": v(12.22, 106.55) * mm});
            skLineSegment(sketch, "E69.1.287.0", {"start": v(8.66, 106.9) * mm, "end": v(9.9, 106.8) * mm});
            skLineSegment(sketch, "E69.1.288.0", {"start": v(6.34, 107.06) * mm, "end": v(7.6, 106.98) * mm});
            skLineSegment(sketch, "E69.1.289.0", {"start": v(4.02, 107.17) * mm, "end": v(5.27, 107.12) * mm});
            skCircle(sketch, "E70", {"center": v(-22.23, 0) * mm, "radius": 0.66 * mm});
            skCircle(sketch, "E71", {"center": v(15.88, 0) * mm, "radius": 0.66 * mm});
            skSolve(sketch);
        }
        {
            var Q0;
            Q0=makeQuery(id+"F0.imprint","IMPRINT",FACE,{"disambiguationData":[TD([[makeQuery(id+"F0.imprint","IMPRINT",EDGE,{"derivedFrom":sQuery(id+"F0.wireOp",EDGE,"E1")}),-1.0]])]});
            extrude(context, id + "F1", {"entities" : qUnion([Q0]), "depth" : 3.17 * mm});
        }
    });
